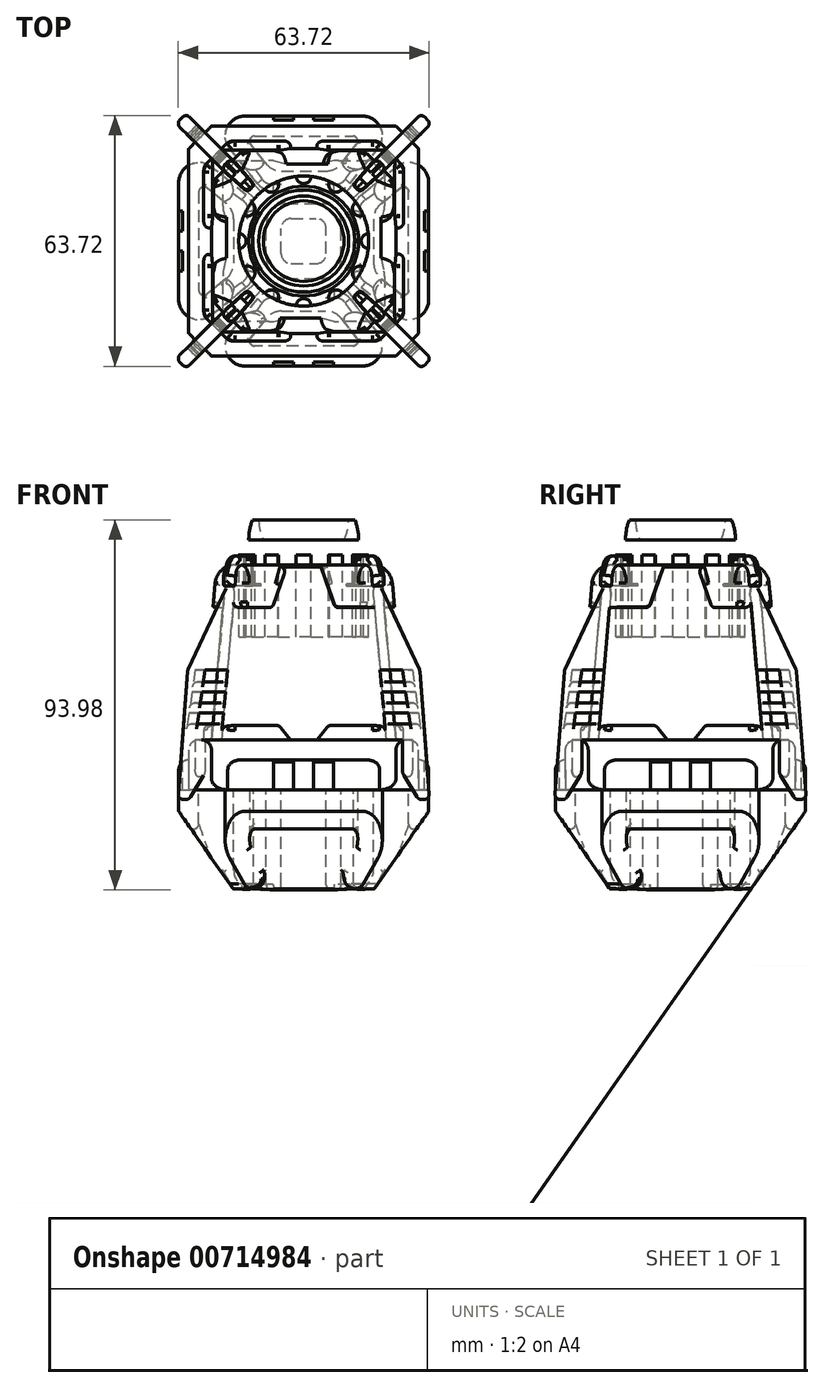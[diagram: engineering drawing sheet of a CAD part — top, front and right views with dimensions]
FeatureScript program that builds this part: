
annotation { "Feature Type Name" : "Feature", "Feature Type Description" : "" }
export const myFeature = defineFeature(function(context is Context, id is Id, definition is map)
    precondition{}
    {
        {
            var Q0;
            Q0=qCreatedBy(makeId("Top.planeOp"),FACE);
            cPlane(context, id + "F0", {"entities" : qUnion([Q0]), "cplaneType" : CPlaneType.OFFSET, "offset" : 44.45 * mm, "width" : 152.4 * mm, "height" : 152.4 * mm});
        }
        {
            var Q0;
            Q0=qCreatedBy(id+"F0.planeOp",FACE);
            var sketch = newSketch(context, id + "F1", { "sketchPlane" : qUnion([Q0])});
            skLineSegment(sketch, "E0.bottom", {"start": v(22.23, -22.22) * mm, "end": v(-22.23, -22.23) * mm});
            skLineSegment(sketch, "E0.top", {"start": v(22.23, 22.23) * mm, "end": v(-22.23, 22.22) * mm});
            skLineSegment(sketch, "E0.left", {"start": v(22.23, -22.22) * mm, "end": v(22.23, 22.23) * mm});
            skLineSegment(sketch, "E0.right", {"start": v(-22.23, -22.23) * mm, "end": v(-22.23, 22.22) * mm});
            skPoint(sketch, "E0.middle", {"position": v(0, 0) * mm});
            skSolve(sketch);
        }
        {
            var Q0;
            Q0=qCreatedBy(makeId("Top.planeOp"),FACE);
            var sketch = newSketch(context, id + "F2", { "sketchPlane" : qUnion([Q0])});
            skLineSegment(sketch, "E1.bottom", {"start": v(-25.4, 25.4) * mm, "end": v(25.4, 25.4) * mm});
            skLineSegment(sketch, "E1.top", {"start": v(-25.4, -25.4) * mm, "end": v(25.4, -25.4) * mm});
            skLineSegment(sketch, "E1.left", {"start": v(-25.4, 25.4) * mm, "end": v(-25.4, -25.4) * mm});
            skLineSegment(sketch, "E1.right", {"start": v(25.4, 25.4) * mm, "end": v(25.4, -25.4) * mm});
            skPoint(sketch, "E1.middle", {"position": v(0, 0) * mm});
            skSolve(sketch);
        }
        {
            var Q0;
            Q0=makeQuery(id+"F2.imprint","IMPRINT",FACE,{"disambiguationData":[TD([[makeQuery(id+"F2.imprint","IMPRINT",EDGE,{"derivedFrom":sQuery(id+"F2.wireOp",EDGE,"E1.bottom")}),-1.0]])]});
            extrude(context, id + "F3", {"entities" : qUnion([Q0]), "depth" : 44.45 * mm, "offsetDistance" : 25.4 * mm});
        }
        {
            var Q0;
            Q0=makeQuery(id+"F3.opExtrude","CAP_EDGE",EDGE,{"disambiguationData":[OSD([sQuery(id+"F2.wireOp",EDGE,"E1.top")])],"isStart":false});
            var Q1;
            Q1=makeQuery(id+"F3.opExtrude","CAP_EDGE",EDGE,{"disambiguationData":[OSD([sQuery(id+"F2.wireOp",EDGE,"E1.left")])],"isStart":false});
            var Q2;
            Q2=makeQuery(id+"F3.opExtrude","CAP_EDGE",EDGE,{"disambiguationData":[OSD([sQuery(id+"F2.wireOp",EDGE,"E1.bottom")])],"isStart":false});
            var Q3;
            Q3=makeQuery(id+"F3.opExtrude","CAP_EDGE",EDGE,{"disambiguationData":[OSD([sQuery(id+"F2.wireOp",EDGE,"E1.right")])],"isStart":false});
            chamfer(context, id + "F4", {"entities" : qUnion([Q0, Q1, Q2, Q3]), "chamferType" : ChamferType.OFFSET_ANGLE, "width" : 3.3 * mm, "oppositeDirection" : false, "angle" : 85 * degree, "tangentPropagation" : true});
        }
        {
            var Q0;
            Q0=makeQuery(id+"F4.opChamfer","BLEND_EDGE",EDGE,{"blendedFrom":[makeQuery(id+"F3.opExtrude","CAP_EDGE",EDGE,{"disambiguationData":[OSD([sQuery(id+"F2.wireOp",EDGE,"E1.bottom")])],"isStart":false}),makeQuery(id+"F3.opExtrude","CAP_EDGE",EDGE,{"disambiguationData":[OSD([sQuery(id+"F2.wireOp",EDGE,"E1.right")])],"isStart":false})],"blendedInto":[]});
            var Q1;
            Q1=makeQuery(id+"F4.opChamfer","BLEND_EDGE",EDGE,{"blendedFrom":[makeQuery(id+"F3.opExtrude","CAP_EDGE",EDGE,{"disambiguationData":[OSD([sQuery(id+"F2.wireOp",EDGE,"E1.bottom")])],"isStart":false}),makeQuery(id+"F3.opExtrude","CAP_EDGE",EDGE,{"disambiguationData":[OSD([sQuery(id+"F2.wireOp",EDGE,"E1.left")])],"isStart":false})],"blendedInto":[]});
            var Q2;
            Q2=makeQuery(id+"F4.opChamfer","BLEND_EDGE",EDGE,{"blendedFrom":[makeQuery(id+"F3.opExtrude","CAP_EDGE",EDGE,{"disambiguationData":[OSD([sQuery(id+"F2.wireOp",EDGE,"E1.top")])],"isStart":false}),makeQuery(id+"F3.opExtrude","CAP_EDGE",EDGE,{"disambiguationData":[OSD([sQuery(id+"F2.wireOp",EDGE,"E1.left")])],"isStart":false})],"blendedInto":[]});
            var Q3;
            Q3=makeQuery(id+"F4.opChamfer","BLEND_EDGE",EDGE,{"blendedFrom":[makeQuery(id+"F3.opExtrude","CAP_EDGE",EDGE,{"disambiguationData":[OSD([sQuery(id+"F2.wireOp",EDGE,"E1.top")])],"isStart":false}),makeQuery(id+"F3.opExtrude","CAP_EDGE",EDGE,{"disambiguationData":[OSD([sQuery(id+"F2.wireOp",EDGE,"E1.right")])],"isStart":false})],"blendedInto":[]});
            chamfer(context, id + "F5", {"entities" : qUnion([Q0, Q1, Q2, Q3]), "width" : 7.62 * mm, "tangentPropagation" : true});
        }
        {
            var Q0;
            Q0=makeQuery(id+"F4.opChamfer","BLEND_FACE",FACE,{"disambiguationData":[OSD([sQuery(id+"F2.wireOp",EDGE,"E1.bottom")])]});
            var sketch = newSketch(context, id + "F6", { "sketchPlane" : qUnion([Q0])});
            skLineSegment(sketch, "E2", {"start": v(23.42, 31.68) * mm, "end": v(-23.11, 31.68) * mm});
            skLineSegment(sketch, "E3.top", {"start": v(7.98, 20.9) * mm, "end": v(-7.96, 20.9) * mm});
            skLineSegment(sketch, "E3.left", {"start": v(7.98, 42.46) * mm, "end": v(7.98, 20.9) * mm});
            skLineSegment(sketch, "E3.right", {"start": v(-7.96, 42.46) * mm, "end": v(-7.96, 20.9) * mm});
            skPoint(sketch, "E3.middle", {"position": v(0.01, 31.68) * mm});
            skLineSegment(sketch, "E4.top", {"start": v(4.3, 20.9) * mm, "end": v(-4.28, 20.9) * mm});
            skLineSegment(sketch, "E4.left", {"start": v(4.3, 42.46) * mm, "end": v(4.3, 20.9) * mm});
            skLineSegment(sketch, "E4.right", {"start": v(-4.28, 42.46) * mm, "end": v(-4.28, 20.9) * mm});
            skLineSegment(sketch, "E5", {"start": v(4.3, 42.46) * mm, "end": v(7.98, 31.68) * mm});
            skLineSegment(sketch, "E6", {"start": v(-4.28, 42.46) * mm, "end": v(-7.96, 31.68) * mm});
            skLineSegment(sketch, "E7", {"start": v(27.08, 1.49) * mm, "end": v(-26.68, 1.49) * mm});
            skLineSegment(sketch, "E8.bottom", {"start": v(3.25, 1.49) * mm, "end": v(-3.23, 1.49) * mm});
            skLineSegment(sketch, "E8.top", {"start": v(3.25, -5.96) * mm, "end": v(-3.23, -5.96) * mm});
            skLineSegment(sketch, "E8.left", {"start": v(3.25, 1.49) * mm, "end": v(3.25, -5.96) * mm});
            skLineSegment(sketch, "E8.right", {"start": v(-3.23, 1.49) * mm, "end": v(-3.23, -5.96) * mm});
            skPoint(sketch, "E8.middle", {"position": v(0.01, -2.24) * mm});
            skLineSegment(sketch, "E9.bottom", {"start": v(6.26, 1.49) * mm, "end": v(-6.23, 1.49) * mm});
            skLineSegment(sketch, "E9.top", {"start": v(6.26, -5.96) * mm, "end": v(-6.23, -5.96) * mm});
            skLineSegment(sketch, "E9.left", {"start": v(6.26, 1.49) * mm, "end": v(6.26, -5.96) * mm});
            skLineSegment(sketch, "E9.right", {"start": v(-6.23, 1.49) * mm, "end": v(-6.23, -5.96) * mm});
            skLineSegment(sketch, "E10", {"start": v(3.25, -2.24) * mm, "end": v(6.26, 1.49) * mm});
            skLineSegment(sketch, "E11", {"start": v(-3.23, -2.24) * mm, "end": v(-6.23, 1.49) * mm});
            skLineSegment(sketch, "E12", {"start": v(0, 42.46) * mm, "end": v(0, -5.44) * mm});
            skPoint(sketch, "E12.startSnap0", {"position": v(0.01, 42.46) * mm});
            skLineSegment(sketch, "E13", {"start": v(-23.11, 31.68) * mm, "end": v(-25.73, 31.68) * mm});
            skLineSegment(sketch, "E14", {"start": v(-26.68, 1.49) * mm, "end": v(-25.73, 31.68) * mm});
            skLineSegment(sketch, "E15", {"start": v(23.42, 31.68) * mm, "end": v(26, 31.68) * mm});
            skLineSegment(sketch, "E16", {"start": v(27.08, 1.49) * mm, "end": v(26, 31.68) * mm});
            skLineSegment(sketch, "E17", {"start": v(-7.96, 31.68) * mm, "end": v(-2.3, 48.28) * mm});
            skLineSegment(sketch, "E18", {"start": v(7.98, 31.68) * mm, "end": v(2.41, 48.03) * mm});
            skLineSegment(sketch, "E19", {"start": v(-2.3, 48.28) * mm, "end": v(2.41, 48.03) * mm});
            skSolve(sketch);
        }
        {
            var Q0;
            {var subQ4=sQuery(id+"F6.wireOp",EDGE,"E19");Q0=makeQuery(id+"F6.imprint","IMPRINT",FACE,{"disambiguationData":[TD([[makeQuery(id+"F6.imprint","IMPRINT",EDGE,{"derivedFrom":subQ4}),-1.0]])]});}
            var Q1;
            {var subQ0=sQuery(id+"F6.wireOp",EDGE,"E12");var subQ1=sQuery(id+"F6.wireOp",EDGE,"E2");var subQ2=makeQuery(id+"F6.imprint","INTERSECT",VERTEX,{"derivedFrom":[subQ1,subQ0]});Q1=makeQuery(id+"F6.imprint","IMPRINT",FACE,{"disambiguationData":[TD([[makeQuery(id+"F6.imprint","IMPRINT",EDGE,{"disambiguationData":[TD([[subQ2,-1.0]])],"derivedFrom":subQ1}),-1.0]])]});}
            var Q2;
            {var subQ0=sQuery(id+"F6.wireOp",EDGE,"E4.left");var subQ1=sQuery(id+"F6.wireOp",EDGE,"E2");var subQ2=makeQuery(id+"F6.imprint","INTERSECT",VERTEX,{"derivedFrom":[subQ1,subQ0]});Q2=makeQuery(id+"F6.imprint","IMPRINT",FACE,{"disambiguationData":[TD([[makeQuery(id+"F6.imprint","IMPRINT",EDGE,{"disambiguationData":[TD([[subQ2,-1.0]])],"derivedFrom":subQ1}),-1.0]])]});}
            var Q3;
            {var subQ1=sQuery(id+"F6.wireOp",EDGE,"E2");var subQ3=sQuery(id+"F6.wireOp",EDGE,"E4.left");var subQ4=makeQuery(id+"F6.imprint","INTERSECT",VERTEX,{"derivedFrom":[subQ1,subQ3]});Q3=makeQuery(id+"F6.imprint","IMPRINT",FACE,{"disambiguationData":[TD([[makeQuery(id+"F6.imprint","IMPRINT",EDGE,{"disambiguationData":[TD([[subQ4,1.0]])],"derivedFrom":subQ1}),-1.0]])]});}
            var Q4;
            {var subQ1=sQuery(id+"F6.wireOp",EDGE,"E2");var subQ3=sQuery(id+"F6.wireOp",EDGE,"E4.right");var subQ4=makeQuery(id+"F6.imprint","INTERSECT",VERTEX,{"derivedFrom":[subQ1,subQ3]});Q4=makeQuery(id+"F6.imprint","IMPRINT",FACE,{"disambiguationData":[TD([[makeQuery(id+"F6.imprint","IMPRINT",EDGE,{"disambiguationData":[TD([[subQ4,-1.0]])],"derivedFrom":subQ1}),-1.0]])]});}
            var Q5;
            {var subQ0=sQuery(id+"F6.wireOp",EDGE,"E3.right");var subQ1=sQuery(id+"F6.wireOp",EDGE,"E3.top");var subQ2=makeQuery(id+"F6.imprint","INTERSECT",VERTEX,{"derivedFrom":[subQ1,subQ0]});Q5=makeQuery(id+"F6.imprint","IMPRINT",FACE,{"disambiguationData":[TD([[makeQuery(id+"F6.imprint","IMPRINT",EDGE,{"disambiguationData":[TD([[subQ2,1.0]])],"derivedFrom":subQ1}),1.0]])]});}
            var Q6;
            {var subQ1=sQuery(id+"F6.wireOp",EDGE,"E2");var subQ3=sQuery(id+"F6.wireOp",EDGE,"E4.right");var subQ4=makeQuery(id+"F6.imprint","INTERSECT",VERTEX,{"derivedFrom":[subQ1,subQ3]});Q6=makeQuery(id+"F6.imprint","IMPRINT",FACE,{"disambiguationData":[TD([[makeQuery(id+"F6.imprint","IMPRINT",EDGE,{"disambiguationData":[TD([[subQ4,-1.0]])],"derivedFrom":subQ1}),1.0]])]});}
            var Q7;
            {var subQ0=sQuery(id+"F6.wireOp",EDGE,"E12");var subQ1=sQuery(id+"F6.wireOp",EDGE,"E2");var subQ2=makeQuery(id+"F6.imprint","INTERSECT",VERTEX,{"derivedFrom":[subQ1,subQ0]});Q7=makeQuery(id+"F6.imprint","IMPRINT",FACE,{"disambiguationData":[TD([[makeQuery(id+"F6.imprint","IMPRINT",EDGE,{"disambiguationData":[TD([[subQ2,-1.0]])],"derivedFrom":subQ1}),1.0]])]});}
            var Q8;
            {var subQ0=sQuery(id+"F6.wireOp",EDGE,"E4.left");var subQ1=sQuery(id+"F6.wireOp",EDGE,"E2");var subQ2=makeQuery(id+"F6.imprint","INTERSECT",VERTEX,{"derivedFrom":[subQ1,subQ0]});Q8=makeQuery(id+"F6.imprint","IMPRINT",FACE,{"disambiguationData":[TD([[makeQuery(id+"F6.imprint","IMPRINT",EDGE,{"disambiguationData":[TD([[subQ2,-1.0]])],"derivedFrom":subQ1}),1.0]])]});}
            var Q9;
            {var subQ1=sQuery(id+"F6.wireOp",EDGE,"E2");var subQ3=sQuery(id+"F6.wireOp",EDGE,"E4.left");var subQ4=makeQuery(id+"F6.imprint","INTERSECT",VERTEX,{"derivedFrom":[subQ1,subQ3]});Q9=makeQuery(id+"F6.imprint","IMPRINT",FACE,{"disambiguationData":[TD([[makeQuery(id+"F6.imprint","IMPRINT",EDGE,{"disambiguationData":[TD([[subQ4,1.0]])],"derivedFrom":subQ1}),1.0]])]});}
            var Q10;
            {var subQ0=sQuery(id+"F6.wireOp",EDGE,"E3.left");var subQ1=sQuery(id+"F6.wireOp",EDGE,"E3.top");var subQ2=makeQuery(id+"F6.imprint","INTERSECT",VERTEX,{"derivedFrom":[subQ1,subQ0]});Q10=makeQuery(id+"F6.imprint","IMPRINT",FACE,{"disambiguationData":[TD([[makeQuery(id+"F6.imprint","IMPRINT",EDGE,{"disambiguationData":[TD([[subQ2,-1.0]])],"derivedFrom":subQ1}),1.0]])]});}
            var Q11;
            {var subQ3=sQuery(id+"F6.wireOp",EDGE,"E11");Q11=makeQuery(id+"F6.imprint","IMPRINT",FACE,{"disambiguationData":[TD([[makeQuery(id+"F6.imprint","IMPRINT",EDGE,{"derivedFrom":subQ3}),-1.0]])]});}
            var Q12;
            {var subQ4=sQuery(id+"F6.wireOp",EDGE,"E9.bottom");var subQ6=sQuery(id+"F6.wireOp",EDGE,"E8.left");var subQ9=makeQuery(id+"F6.imprint","INTERSECT",VERTEX,{"derivedFrom":[subQ6,subQ4]});Q12=makeQuery(id+"F6.imprint","IMPRINT",FACE,{"disambiguationData":[TD([[makeQuery(id+"F6.imprint","IMPRINT",EDGE,{"disambiguationData":[TD([[subQ9,-1.0]])],"derivedFrom":subQ6}),-1.0]])]});}
            var Q13;
            {var subQ3=sQuery(id+"F6.wireOp",EDGE,"E10");Q13=makeQuery(id+"F6.imprint","IMPRINT",FACE,{"disambiguationData":[TD([[makeQuery(id+"F6.imprint","IMPRINT",EDGE,{"derivedFrom":subQ3}),1.0]])]});}
            var Q14;
            {var subQ7=sQuery(id+"F6.wireOp",EDGE,"E15");Q14=makeQuery(id+"F6.imprint","IMPRINT",FACE,{"disambiguationData":[TD([[makeQuery(id+"F6.imprint","IMPRINT",EDGE,{"derivedFrom":subQ7}),-1.0]])]});}
            var Q15;
            {var subQ7=sQuery(id+"F6.wireOp",EDGE,"E13");Q15=makeQuery(id+"F6.imprint","IMPRINT",FACE,{"disambiguationData":[TD([[makeQuery(id+"F6.imprint","IMPRINT",EDGE,{"derivedFrom":subQ7}),1.0]])]});}
            var Q16;
            {var subQ0=sQuery(id+"F6.wireOp",EDGE,"E17");var subQ1=sQuery(id+"F6.wireOp",EDGE,"E4.right");var subQ2=makeQuery(id+"F6.imprint","INTERSECT",VERTEX,{"derivedFrom":[subQ1,subQ0]});Q16=makeQuery(id+"F6.imprint","IMPRINT",FACE,{"disambiguationData":[TD([[makeQuery(id+"F6.imprint","IMPRINT",EDGE,{"disambiguationData":[TD([[subQ2,-1.0]])],"derivedFrom":subQ1}),-1.0]])]});}
            var Q17;
            {var subQ0=sQuery(id+"F6.wireOp",EDGE,"E18");var subQ1=sQuery(id+"F6.wireOp",EDGE,"E4.left");var subQ2=makeQuery(id+"F6.imprint","INTERSECT",VERTEX,{"derivedFrom":[subQ1,subQ0]});Q17=makeQuery(id+"F6.imprint","IMPRINT",FACE,{"disambiguationData":[TD([[makeQuery(id+"F6.imprint","IMPRINT",EDGE,{"disambiguationData":[TD([[subQ2,-1.0]])],"derivedFrom":subQ1}),1.0]])]});}
            extrude(context, id + "F7", {"entities" : qUnion([Q0, Q1, Q2, Q3, Q4, Q5, Q6, Q7, Q8, Q9, Q10, Q11, Q12, Q13, Q14, Q15, Q16, Q17]), "operationType" : NewBodyOperationType.REMOVE, "oppositeDirection" : true, "depth" : 2.54 * mm, "offsetDistance" : 25.4 * mm});
        }
        {
            var Q0;
            Q0=makeQuery(id+"F4.opChamfer","BLEND_FACE",FACE,{"disambiguationData":[OSD([sQuery(id+"F2.wireOp",EDGE,"E1.left")])]});
            var sketch = newSketch(context, id + "F8", { "sketchPlane" : qUnion([Q0])});
            skLineSegment(sketch, "E20", {"start": v(23.38, 31.67) * mm, "end": v(-23.15, 31.67) * mm});
            skLineSegment(sketch, "E21.top", {"start": v(7.98, 20.88) * mm, "end": v(-7.96, 20.88) * mm});
            skLineSegment(sketch, "E21.left", {"start": v(7.98, 42.45) * mm, "end": v(7.98, 20.88) * mm});
            skLineSegment(sketch, "E21.right", {"start": v(-7.96, 42.45) * mm, "end": v(-7.96, 20.88) * mm});
            skPoint(sketch, "E21.middle", {"position": v(0.01, 31.67) * mm});
            skLineSegment(sketch, "E22.top", {"start": v(4.2, 20.88) * mm, "end": v(-4.18, 20.88) * mm});
            skLineSegment(sketch, "E22.left", {"start": v(4.2, 42.45) * mm, "end": v(4.2, 20.88) * mm});
            skLineSegment(sketch, "E22.right", {"start": v(-4.18, 42.45) * mm, "end": v(-4.18, 20.88) * mm});
            skLineSegment(sketch, "E23", {"start": v(4.2, 42.45) * mm, "end": v(7.98, 31.67) * mm});
            skLineSegment(sketch, "E24", {"start": v(-4.18, 42.45) * mm, "end": v(-7.96, 31.67) * mm});
            skLineSegment(sketch, "E25", {"start": v(27.08, 1.52) * mm, "end": v(-26.68, 1.52) * mm});
            skLineSegment(sketch, "E26.bottom", {"start": v(3.25, 1.52) * mm, "end": v(-3.23, 1.52) * mm});
            skLineSegment(sketch, "E26.top", {"start": v(3.25, -6.02) * mm, "end": v(-3.23, -6.02) * mm});
            skLineSegment(sketch, "E26.left", {"start": v(3.25, 1.52) * mm, "end": v(3.25, -6.02) * mm});
            skLineSegment(sketch, "E26.right", {"start": v(-3.23, 1.52) * mm, "end": v(-3.23, -6.02) * mm});
            skPoint(sketch, "E26.middle", {"position": v(0.01, -2.25) * mm});
            skLineSegment(sketch, "E27.bottom", {"start": v(6.28, 1.52) * mm, "end": v(-6.26, 1.52) * mm});
            skLineSegment(sketch, "E27.top", {"start": v(6.28, -6.02) * mm, "end": v(-6.26, -6.02) * mm});
            skLineSegment(sketch, "E27.left", {"start": v(6.28, 1.52) * mm, "end": v(6.28, -6.02) * mm});
            skLineSegment(sketch, "E27.right", {"start": v(-6.26, 1.52) * mm, "end": v(-6.26, -6.02) * mm});
            skLineSegment(sketch, "E28", {"start": v(3.25, -2.25) * mm, "end": v(6.28, 1.52) * mm});
            skLineSegment(sketch, "E29", {"start": v(-3.23, -2.25) * mm, "end": v(-6.26, 1.52) * mm});
            skLineSegment(sketch, "E30", {"start": v(0, 42.45) * mm, "end": v(0, -2.29) * mm});
            skPoint(sketch, "E30.startSnap0", {"position": v(0.01, 42.45) * mm});
            skLineSegment(sketch, "E31", {"start": v(-23.15, 31.67) * mm, "end": v(-25.73, 31.67) * mm});
            skLineSegment(sketch, "E32", {"start": v(-26.68, 1.52) * mm, "end": v(-25.73, 31.67) * mm});
            skLineSegment(sketch, "E33", {"start": v(23.38, 31.67) * mm, "end": v(26.01, 31.67) * mm});
            skLineSegment(sketch, "E34", {"start": v(27.08, 1.52) * mm, "end": v(26.01, 31.67) * mm});
            skLineSegment(sketch, "E35", {"start": v(-7.96, 31.67) * mm, "end": v(-2.14, 48.27) * mm});
            skLineSegment(sketch, "E36", {"start": v(7.98, 31.67) * mm, "end": v(2.25, 48.02) * mm});
            skLineSegment(sketch, "E37", {"start": v(-2.14, 48.27) * mm, "end": v(2.25, 48.02) * mm});
            skSolve(sketch);
        }
        {
            var Q0;
            {var subQ4=sQuery(id+"F8.wireOp",EDGE,"E37");Q0=makeQuery(id+"F8.imprint","IMPRINT",FACE,{"disambiguationData":[TD([[makeQuery(id+"F8.imprint","IMPRINT",EDGE,{"derivedFrom":subQ4}),-1.0]])]});}
            var Q1;
            {var subQ0=sQuery(id+"F8.wireOp",EDGE,"E30");var subQ1=sQuery(id+"F8.wireOp",EDGE,"E20");var subQ2=makeQuery(id+"F8.imprint","INTERSECT",VERTEX,{"derivedFrom":[subQ1,subQ0]});Q1=makeQuery(id+"F8.imprint","IMPRINT",FACE,{"disambiguationData":[TD([[makeQuery(id+"F8.imprint","IMPRINT",EDGE,{"disambiguationData":[TD([[subQ2,-1.0]])],"derivedFrom":subQ1}),-1.0]])]});}
            var Q2;
            {var subQ0=sQuery(id+"F8.wireOp",EDGE,"E22.left");var subQ1=sQuery(id+"F8.wireOp",EDGE,"E20");var subQ2=makeQuery(id+"F8.imprint","INTERSECT",VERTEX,{"derivedFrom":[subQ1,subQ0]});Q2=makeQuery(id+"F8.imprint","IMPRINT",FACE,{"disambiguationData":[TD([[makeQuery(id+"F8.imprint","IMPRINT",EDGE,{"disambiguationData":[TD([[subQ2,-1.0]])],"derivedFrom":subQ1}),-1.0]])]});}
            var Q3;
            {var subQ1=sQuery(id+"F8.wireOp",EDGE,"E20");var subQ3=sQuery(id+"F8.wireOp",EDGE,"E22.left");var subQ4=makeQuery(id+"F8.imprint","INTERSECT",VERTEX,{"derivedFrom":[subQ1,subQ3]});Q3=makeQuery(id+"F8.imprint","IMPRINT",FACE,{"disambiguationData":[TD([[makeQuery(id+"F8.imprint","IMPRINT",EDGE,{"disambiguationData":[TD([[subQ4,1.0]])],"derivedFrom":subQ1}),-1.0]])]});}
            var Q4;
            {var subQ1=sQuery(id+"F8.wireOp",EDGE,"E20");var subQ3=sQuery(id+"F8.wireOp",EDGE,"E22.right");var subQ4=makeQuery(id+"F8.imprint","INTERSECT",VERTEX,{"derivedFrom":[subQ1,subQ3]});Q4=makeQuery(id+"F8.imprint","IMPRINT",FACE,{"disambiguationData":[TD([[makeQuery(id+"F8.imprint","IMPRINT",EDGE,{"disambiguationData":[TD([[subQ4,-1.0]])],"derivedFrom":subQ1}),-1.0]])]});}
            var Q5;
            {var subQ1=sQuery(id+"F8.wireOp",EDGE,"E20");var subQ3=sQuery(id+"F8.wireOp",EDGE,"E22.right");var subQ4=makeQuery(id+"F8.imprint","INTERSECT",VERTEX,{"derivedFrom":[subQ1,subQ3]});Q5=makeQuery(id+"F8.imprint","IMPRINT",FACE,{"disambiguationData":[TD([[makeQuery(id+"F8.imprint","IMPRINT",EDGE,{"disambiguationData":[TD([[subQ4,-1.0]])],"derivedFrom":subQ1}),1.0]])]});}
            var Q6;
            {var subQ0=sQuery(id+"F8.wireOp",EDGE,"E30");var subQ1=sQuery(id+"F8.wireOp",EDGE,"E20");var subQ2=makeQuery(id+"F8.imprint","INTERSECT",VERTEX,{"derivedFrom":[subQ1,subQ0]});Q6=makeQuery(id+"F8.imprint","IMPRINT",FACE,{"disambiguationData":[TD([[makeQuery(id+"F8.imprint","IMPRINT",EDGE,{"disambiguationData":[TD([[subQ2,-1.0]])],"derivedFrom":subQ1}),1.0]])]});}
            var Q7;
            {var subQ0=sQuery(id+"F8.wireOp",EDGE,"E22.left");var subQ1=sQuery(id+"F8.wireOp",EDGE,"E20");var subQ2=makeQuery(id+"F8.imprint","INTERSECT",VERTEX,{"derivedFrom":[subQ1,subQ0]});Q7=makeQuery(id+"F8.imprint","IMPRINT",FACE,{"disambiguationData":[TD([[makeQuery(id+"F8.imprint","IMPRINT",EDGE,{"disambiguationData":[TD([[subQ2,-1.0]])],"derivedFrom":subQ1}),1.0]])]});}
            var Q8;
            {var subQ1=sQuery(id+"F8.wireOp",EDGE,"E20");var subQ3=sQuery(id+"F8.wireOp",EDGE,"E22.left");var subQ4=makeQuery(id+"F8.imprint","INTERSECT",VERTEX,{"derivedFrom":[subQ1,subQ3]});Q8=makeQuery(id+"F8.imprint","IMPRINT",FACE,{"disambiguationData":[TD([[makeQuery(id+"F8.imprint","IMPRINT",EDGE,{"disambiguationData":[TD([[subQ4,1.0]])],"derivedFrom":subQ1}),1.0]])]});}
            var Q9;
            {var subQ7=sQuery(id+"F8.wireOp",EDGE,"E31");Q9=makeQuery(id+"F8.imprint","IMPRINT",FACE,{"disambiguationData":[TD([[makeQuery(id+"F8.imprint","IMPRINT",EDGE,{"derivedFrom":subQ7}),1.0]])]});}
            var Q10;
            {var subQ0=sQuery(id+"F8.wireOp",EDGE,"E21.right");var subQ1=sQuery(id+"F8.wireOp",EDGE,"E21.top");var subQ2=makeQuery(id+"F8.imprint","INTERSECT",VERTEX,{"derivedFrom":[subQ1,subQ0]});Q10=makeQuery(id+"F8.imprint","IMPRINT",FACE,{"disambiguationData":[TD([[makeQuery(id+"F8.imprint","IMPRINT",EDGE,{"disambiguationData":[TD([[subQ2,1.0]])],"derivedFrom":subQ1}),1.0]])]});}
            var Q11;
            {var subQ0=sQuery(id+"F8.wireOp",EDGE,"E21.left");var subQ1=sQuery(id+"F8.wireOp",EDGE,"E21.top");var subQ2=makeQuery(id+"F8.imprint","INTERSECT",VERTEX,{"derivedFrom":[subQ1,subQ0]});Q11=makeQuery(id+"F8.imprint","IMPRINT",FACE,{"disambiguationData":[TD([[makeQuery(id+"F8.imprint","IMPRINT",EDGE,{"disambiguationData":[TD([[subQ2,-1.0]])],"derivedFrom":subQ1}),1.0]])]});}
            var Q12;
            {var subQ13=sQuery(id+"F8.wireOp",EDGE,"E33");Q12=makeQuery(id+"F8.imprint","IMPRINT",FACE,{"disambiguationData":[TD([[makeQuery(id+"F8.imprint","IMPRINT",EDGE,{"derivedFrom":subQ13}),-1.0]])]});}
            var Q13;
            {var subQ4=sQuery(id+"F8.wireOp",EDGE,"E27.bottom");var subQ6=sQuery(id+"F8.wireOp",EDGE,"E26.left");var subQ9=makeQuery(id+"F8.imprint","INTERSECT",VERTEX,{"derivedFrom":[subQ6,subQ4]});Q13=makeQuery(id+"F8.imprint","IMPRINT",FACE,{"disambiguationData":[TD([[makeQuery(id+"F8.imprint","IMPRINT",EDGE,{"disambiguationData":[TD([[subQ9,-1.0]])],"derivedFrom":subQ6}),-1.0]])]});}
            var Q14;
            {var subQ3=sQuery(id+"F8.wireOp",EDGE,"E29");Q14=makeQuery(id+"F8.imprint","IMPRINT",FACE,{"disambiguationData":[TD([[makeQuery(id+"F8.imprint","IMPRINT",EDGE,{"derivedFrom":subQ3}),-1.0]])]});}
            var Q15;
            {var subQ3=sQuery(id+"F8.wireOp",EDGE,"E28");Q15=makeQuery(id+"F8.imprint","IMPRINT",FACE,{"disambiguationData":[TD([[makeQuery(id+"F8.imprint","IMPRINT",EDGE,{"derivedFrom":subQ3}),1.0]])]});}
            var Q16;
            {var subQ0=sQuery(id+"F8.wireOp",EDGE,"E36");var subQ1=sQuery(id+"F8.wireOp",EDGE,"E22.left");var subQ2=makeQuery(id+"F8.imprint","INTERSECT",VERTEX,{"derivedFrom":[subQ1,subQ0]});Q16=makeQuery(id+"F8.imprint","IMPRINT",FACE,{"disambiguationData":[TD([[makeQuery(id+"F8.imprint","IMPRINT",EDGE,{"disambiguationData":[TD([[subQ2,-1.0]])],"derivedFrom":subQ1}),1.0]])]});}
            var Q17;
            {var subQ0=sQuery(id+"F8.wireOp",EDGE,"E35");var subQ1=sQuery(id+"F8.wireOp",EDGE,"E22.right");var subQ2=makeQuery(id+"F8.imprint","INTERSECT",VERTEX,{"derivedFrom":[subQ1,subQ0]});Q17=makeQuery(id+"F8.imprint","IMPRINT",FACE,{"disambiguationData":[TD([[makeQuery(id+"F8.imprint","IMPRINT",EDGE,{"disambiguationData":[TD([[subQ2,-1.0]])],"derivedFrom":subQ1}),-1.0]])]});}
            extrude(context, id + "F9", {"entities" : qUnion([Q0, Q1, Q2, Q3, Q4, Q5, Q6, Q7, Q8, Q9, Q10, Q11, Q12, Q13, Q14, Q15, Q16, Q17]), "operationType" : NewBodyOperationType.REMOVE, "oppositeDirection" : true, "depth" : 2.54 * mm, "offsetDistance" : 25.4 * mm});
        }
        {
            var Q0;
            Q0=makeQuery(id+"F4.opChamfer","BLEND_FACE",FACE,{"disambiguationData":[OSD([sQuery(id+"F2.wireOp",EDGE,"E1.top")])]});
            var sketch = newSketch(context, id + "F10", { "sketchPlane" : qUnion([Q0])});
            skLineSegment(sketch, "E38", {"start": v(23.34, 31.68) * mm, "end": v(-23.2, 31.68) * mm});
            skLineSegment(sketch, "E39.top", {"start": v(7.99, 20.9) * mm, "end": v(-7.95, 20.9) * mm});
            skLineSegment(sketch, "E39.left", {"start": v(7.99, 42.47) * mm, "end": v(7.99, 20.9) * mm});
            skLineSegment(sketch, "E39.right", {"start": v(-7.95, 42.47) * mm, "end": v(-7.95, 20.9) * mm});
            skPoint(sketch, "E39.middle", {"position": v(0.02, 31.68) * mm});
            skLineSegment(sketch, "E40.top", {"start": v(4.2, 20.9) * mm, "end": v(-4.17, 20.9) * mm});
            skLineSegment(sketch, "E40.left", {"start": v(4.2, 42.47) * mm, "end": v(4.2, 20.9) * mm});
            skLineSegment(sketch, "E40.right", {"start": v(-4.17, 42.47) * mm, "end": v(-4.17, 20.9) * mm});
            skLineSegment(sketch, "E41", {"start": v(4.2, 42.47) * mm, "end": v(7.99, 31.68) * mm});
            skLineSegment(sketch, "E42", {"start": v(-4.17, 42.47) * mm, "end": v(-7.95, 31.68) * mm});
            skLineSegment(sketch, "E43", {"start": v(27.08, 1.54) * mm, "end": v(-26.67, 1.54) * mm});
            skLineSegment(sketch, "E44.bottom", {"start": v(3.26, 1.54) * mm, "end": v(-3.22, 1.54) * mm});
            skLineSegment(sketch, "E44.top", {"start": v(3.26, -6) * mm, "end": v(-3.22, -6) * mm});
            skLineSegment(sketch, "E44.left", {"start": v(3.26, 1.54) * mm, "end": v(3.26, -6) * mm});
            skLineSegment(sketch, "E44.right", {"start": v(-3.22, 1.54) * mm, "end": v(-3.22, -6) * mm});
            skPoint(sketch, "E44.middle", {"position": v(0.02, -2.23) * mm});
            skLineSegment(sketch, "E45.bottom", {"start": v(6.29, 1.54) * mm, "end": v(-6.25, 1.54) * mm});
            skLineSegment(sketch, "E45.top", {"start": v(6.29, -6) * mm, "end": v(-6.25, -6) * mm});
            skLineSegment(sketch, "E45.left", {"start": v(6.29, 1.54) * mm, "end": v(6.29, -6) * mm});
            skLineSegment(sketch, "E45.right", {"start": v(-6.25, 1.54) * mm, "end": v(-6.25, -6) * mm});
            skLineSegment(sketch, "E46", {"start": v(3.26, -2.23) * mm, "end": v(6.29, 1.54) * mm});
            skLineSegment(sketch, "E47", {"start": v(-3.22, -2.23) * mm, "end": v(-6.25, 1.54) * mm});
            skLineSegment(sketch, "E48", {"start": v(0, 42.47) * mm, "end": v(0, 2.2) * mm});
            skPoint(sketch, "E48.startSnap0", {"position": v(0.02, 42.47) * mm});
            skLineSegment(sketch, "E49", {"start": v(-23.2, 31.68) * mm, "end": v(-25.72, 31.68) * mm});
            skLineSegment(sketch, "E50", {"start": v(-26.67, 1.54) * mm, "end": v(-25.72, 31.68) * mm});
            skLineSegment(sketch, "E51", {"start": v(23.34, 31.68) * mm, "end": v(26.02, 31.68) * mm});
            skLineSegment(sketch, "E52", {"start": v(27.08, 1.54) * mm, "end": v(26.02, 31.68) * mm});
            skLineSegment(sketch, "E53", {"start": v(-7.95, 31.68) * mm, "end": v(-2.13, 48.28) * mm});
            skLineSegment(sketch, "E54", {"start": v(7.99, 31.68) * mm, "end": v(2.26, 48.04) * mm});
            skLineSegment(sketch, "E55", {"start": v(-2.13, 48.28) * mm, "end": v(2.26, 48.04) * mm});
            skSolve(sketch);
        }
        {
            var Q0;
            {var subQ3=sQuery(id+"F10.wireOp",EDGE,"E55");Q0=makeQuery(id+"F10.imprint","IMPRINT",FACE,{"disambiguationData":[TD([[makeQuery(id+"F10.imprint","IMPRINT",EDGE,{"derivedFrom":subQ3}),-1.0]])]});}
            var Q1;
            {var subQ0=sQuery(id+"F10.wireOp",EDGE,"E48");var subQ1=sQuery(id+"F10.wireOp",EDGE,"E38");var subQ2=makeQuery(id+"F10.imprint","INTERSECT",VERTEX,{"derivedFrom":[subQ1,subQ0]});Q1=makeQuery(id+"F10.imprint","IMPRINT",FACE,{"disambiguationData":[TD([[makeQuery(id+"F10.imprint","IMPRINT",EDGE,{"disambiguationData":[TD([[subQ2,-1.0]])],"derivedFrom":subQ1}),-1.0]])]});}
            var Q2;
            {var subQ0=sQuery(id+"F10.wireOp",EDGE,"E40.left");var subQ1=sQuery(id+"F10.wireOp",EDGE,"E38");var subQ2=makeQuery(id+"F10.imprint","INTERSECT",VERTEX,{"derivedFrom":[subQ1,subQ0]});Q2=makeQuery(id+"F10.imprint","IMPRINT",FACE,{"disambiguationData":[TD([[makeQuery(id+"F10.imprint","IMPRINT",EDGE,{"disambiguationData":[TD([[subQ2,-1.0]])],"derivedFrom":subQ1}),-1.0]])]});}
            var Q3;
            {var subQ1=sQuery(id+"F10.wireOp",EDGE,"E38");var subQ3=sQuery(id+"F10.wireOp",EDGE,"E40.right");var subQ4=makeQuery(id+"F10.imprint","INTERSECT",VERTEX,{"derivedFrom":[subQ1,subQ3]});Q3=makeQuery(id+"F10.imprint","IMPRINT",FACE,{"disambiguationData":[TD([[makeQuery(id+"F10.imprint","IMPRINT",EDGE,{"disambiguationData":[TD([[subQ4,-1.0]])],"derivedFrom":subQ1}),-1.0]])]});}
            var Q4;
            {var subQ1=sQuery(id+"F10.wireOp",EDGE,"E38");var subQ3=sQuery(id+"F10.wireOp",EDGE,"E40.left");var subQ4=makeQuery(id+"F10.imprint","INTERSECT",VERTEX,{"derivedFrom":[subQ1,subQ3]});Q4=makeQuery(id+"F10.imprint","IMPRINT",FACE,{"disambiguationData":[TD([[makeQuery(id+"F10.imprint","IMPRINT",EDGE,{"disambiguationData":[TD([[subQ4,1.0]])],"derivedFrom":subQ1}),-1.0]])]});}
            var Q5;
            {var subQ0=sQuery(id+"F10.wireOp",EDGE,"E53");var subQ1=sQuery(id+"F10.wireOp",EDGE,"E40.right");var subQ2=makeQuery(id+"F10.imprint","INTERSECT",VERTEX,{"derivedFrom":[subQ1,subQ0]});Q5=makeQuery(id+"F10.imprint","IMPRINT",FACE,{"disambiguationData":[TD([[makeQuery(id+"F10.imprint","IMPRINT",EDGE,{"disambiguationData":[TD([[subQ2,-1.0]])],"derivedFrom":subQ1}),-1.0]])]});}
            var Q6;
            {var subQ0=sQuery(id+"F10.wireOp",EDGE,"E54");var subQ1=sQuery(id+"F10.wireOp",EDGE,"E40.left");var subQ2=makeQuery(id+"F10.imprint","INTERSECT",VERTEX,{"derivedFrom":[subQ1,subQ0]});Q6=makeQuery(id+"F10.imprint","IMPRINT",FACE,{"disambiguationData":[TD([[makeQuery(id+"F10.imprint","IMPRINT",EDGE,{"disambiguationData":[TD([[subQ2,-1.0]])],"derivedFrom":subQ1}),1.0]])]});}
            var Q7;
            {var subQ0=sQuery(id+"F10.wireOp",EDGE,"E39.right");var subQ1=sQuery(id+"F10.wireOp",EDGE,"E39.top");var subQ2=makeQuery(id+"F10.imprint","INTERSECT",VERTEX,{"derivedFrom":[subQ1,subQ0]});Q7=makeQuery(id+"F10.imprint","IMPRINT",FACE,{"disambiguationData":[TD([[makeQuery(id+"F10.imprint","IMPRINT",EDGE,{"disambiguationData":[TD([[subQ2,1.0]])],"derivedFrom":subQ1}),-1.0]])]});}
            var Q8;
            {var subQ0=sQuery(id+"F10.wireOp",EDGE,"E48");var subQ1=sQuery(id+"F10.wireOp",EDGE,"E38");var subQ2=makeQuery(id+"F10.imprint","INTERSECT",VERTEX,{"derivedFrom":[subQ1,subQ0]});Q8=makeQuery(id+"F10.imprint","IMPRINT",FACE,{"disambiguationData":[TD([[makeQuery(id+"F10.imprint","IMPRINT",EDGE,{"disambiguationData":[TD([[subQ2,-1.0]])],"derivedFrom":subQ1}),1.0]])]});}
            var Q9;
            {var subQ0=sQuery(id+"F10.wireOp",EDGE,"E40.left");var subQ1=sQuery(id+"F10.wireOp",EDGE,"E38");var subQ2=makeQuery(id+"F10.imprint","INTERSECT",VERTEX,{"derivedFrom":[subQ1,subQ0]});Q9=makeQuery(id+"F10.imprint","IMPRINT",FACE,{"disambiguationData":[TD([[makeQuery(id+"F10.imprint","IMPRINT",EDGE,{"disambiguationData":[TD([[subQ2,-1.0]])],"derivedFrom":subQ1}),1.0]])]});}
            var Q10;
            {var subQ5=sQuery(id+"F10.wireOp",EDGE,"E39.left");var subQ6=sQuery(id+"F10.wireOp",EDGE,"E39.top");var subQ7=makeQuery(id+"F10.imprint","INTERSECT",VERTEX,{"derivedFrom":[subQ6,subQ5]});Q10=makeQuery(id+"F10.imprint","IMPRINT",FACE,{"disambiguationData":[TD([[makeQuery(id+"F10.imprint","IMPRINT",EDGE,{"disambiguationData":[TD([[subQ7,-1.0]])],"derivedFrom":subQ6}),-1.0]])]});}
            var Q11;
            {var subQ0=sQuery(id+"F10.wireOp",EDGE,"E39.left");var subQ1=sQuery(id+"F10.wireOp",EDGE,"E39.top");var subQ2=makeQuery(id+"F10.imprint","INTERSECT",VERTEX,{"derivedFrom":[subQ1,subQ0]});Q11=makeQuery(id+"F10.imprint","IMPRINT",FACE,{"disambiguationData":[TD([[makeQuery(id+"F10.imprint","IMPRINT",EDGE,{"disambiguationData":[TD([[subQ2,-1.0]])],"derivedFrom":subQ1}),1.0]])]});}
            var Q12;
            {var subQ1=sQuery(id+"F10.wireOp",EDGE,"E49");Q12=makeQuery(id+"F10.imprint","IMPRINT",FACE,{"disambiguationData":[TD([[makeQuery(id+"F10.imprint","IMPRINT",EDGE,{"derivedFrom":subQ1}),1.0]])]});}
            var Q13;
            {var subQ0=sQuery(id+"F10.wireOp",EDGE,"E39.right");var subQ1=sQuery(id+"F10.wireOp",EDGE,"E39.top");var subQ2=makeQuery(id+"F10.imprint","INTERSECT",VERTEX,{"derivedFrom":[subQ1,subQ0]});Q13=makeQuery(id+"F10.imprint","IMPRINT",FACE,{"disambiguationData":[TD([[makeQuery(id+"F10.imprint","IMPRINT",EDGE,{"disambiguationData":[TD([[subQ2,1.0]])],"derivedFrom":subQ1}),1.0]])]});}
            var Q14;
            {var subQ3=sQuery(id+"F10.wireOp",EDGE,"E47");Q14=makeQuery(id+"F10.imprint","IMPRINT",FACE,{"disambiguationData":[TD([[makeQuery(id+"F10.imprint","IMPRINT",EDGE,{"derivedFrom":subQ3}),-1.0]])]});}
            var Q15;
            {var subQ4=sQuery(id+"F10.wireOp",EDGE,"E45.bottom");var subQ6=sQuery(id+"F10.wireOp",EDGE,"E44.left");var subQ9=makeQuery(id+"F10.imprint","INTERSECT",VERTEX,{"derivedFrom":[subQ6,subQ4]});Q15=makeQuery(id+"F10.imprint","IMPRINT",FACE,{"disambiguationData":[TD([[makeQuery(id+"F10.imprint","IMPRINT",EDGE,{"disambiguationData":[TD([[subQ9,-1.0]])],"derivedFrom":subQ6}),-1.0]])]});}
            var Q16;
            {var subQ3=sQuery(id+"F10.wireOp",EDGE,"E46");Q16=makeQuery(id+"F10.imprint","IMPRINT",FACE,{"disambiguationData":[TD([[makeQuery(id+"F10.imprint","IMPRINT",EDGE,{"derivedFrom":subQ3}),1.0]])]});}
            extrude(context, id + "F11", {"entities" : qUnion([Q0, Q1, Q2, Q3, Q4, Q5, Q6, Q7, Q8, Q9, Q10, Q11, Q12, Q13, Q14, Q15, Q16]), "operationType" : NewBodyOperationType.REMOVE, "oppositeDirection" : true, "depth" : 2.54 * mm, "offsetDistance" : 25.4 * mm});
        }
        {
            var Q0;
            Q0=makeQuery(id+"F4.opChamfer","BLEND_FACE",FACE,{"disambiguationData":[OSD([sQuery(id+"F2.wireOp",EDGE,"E1.right")])]});
            var sketch = newSketch(context, id + "F12", { "sketchPlane" : qUnion([Q0])});
            skLineSegment(sketch, "E56", {"start": v(23.34, 31.68) * mm, "end": v(-23.2, 31.68) * mm});
            skLineSegment(sketch, "E57.top", {"start": v(7.98, 25.04) * mm, "end": v(-7.96, 25.04) * mm});
            skLineSegment(sketch, "E57.left", {"start": v(7.98, 38.32) * mm, "end": v(7.98, 25.04) * mm});
            skLineSegment(sketch, "E57.right", {"start": v(-7.96, 38.32) * mm, "end": v(-7.96, 25.04) * mm});
            skPoint(sketch, "E57.middle", {"position": v(0, 31.68) * mm});
            skLineSegment(sketch, "E58.top", {"start": v(6.23, 26.7) * mm, "end": v(-6.21, 26.7) * mm});
            skLineSegment(sketch, "E58.left", {"start": v(6.23, 36.67) * mm, "end": v(6.23, 26.7) * mm});
            skLineSegment(sketch, "E58.right", {"start": v(-6.21, 36.67) * mm, "end": v(-6.21, 26.7) * mm});
            skLineSegment(sketch, "E59", {"start": v(6.23, 36.67) * mm, "end": v(7.98, 31.68) * mm});
            skLineSegment(sketch, "E60", {"start": v(-6.21, 36.67) * mm, "end": v(-7.96, 31.68) * mm});
            skLineSegment(sketch, "E61", {"start": v(27.07, 1.54) * mm, "end": v(-26.68, 1.54) * mm});
            skLineSegment(sketch, "E62.bottom", {"start": v(3.25, 1.54) * mm, "end": v(-3.23, 1.54) * mm});
            skLineSegment(sketch, "E62.top", {"start": v(3.25, -6) * mm, "end": v(-3.23, -6) * mm});
            skLineSegment(sketch, "E62.left", {"start": v(3.25, 1.54) * mm, "end": v(3.25, -6) * mm});
            skLineSegment(sketch, "E62.right", {"start": v(-3.23, 1.54) * mm, "end": v(-3.23, -6) * mm});
            skPoint(sketch, "E62.middle", {"position": v(0, -2.23) * mm});
            skLineSegment(sketch, "E63.bottom", {"start": v(6.28, 1.54) * mm, "end": v(-6.26, 1.54) * mm});
            skLineSegment(sketch, "E63.top", {"start": v(6.28, -6) * mm, "end": v(-6.26, -6) * mm});
            skLineSegment(sketch, "E63.left", {"start": v(6.28, 1.54) * mm, "end": v(6.28, -6) * mm});
            skLineSegment(sketch, "E63.right", {"start": v(-6.26, 1.54) * mm, "end": v(-6.26, -6) * mm});
            skLineSegment(sketch, "E64", {"start": v(3.25, -2.23) * mm, "end": v(6.28, 1.54) * mm});
            skLineSegment(sketch, "E65", {"start": v(-3.23, -2.23) * mm, "end": v(-6.26, 1.54) * mm});
            skLineSegment(sketch, "E66", {"start": v(0, 42.47) * mm, "end": v(0, 2.2) * mm});
            skPoint(sketch, "E66.startSnap0", {"position": v(0, 42.47) * mm});
            skLineSegment(sketch, "E67", {"start": v(-23.2, 31.68) * mm, "end": v(-25.73, 31.68) * mm});
            skLineSegment(sketch, "E68", {"start": v(-26.68, 1.54) * mm, "end": v(-25.73, 31.68) * mm});
            skLineSegment(sketch, "E69", {"start": v(23.34, 31.68) * mm, "end": v(26, 31.68) * mm});
            skLineSegment(sketch, "E70", {"start": v(27.07, 1.54) * mm, "end": v(26, 31.68) * mm});
            skLineSegment(sketch, "E71", {"start": v(-7.96, 31.68) * mm, "end": v(-2.14, 48.28) * mm});
            skLineSegment(sketch, "E72", {"start": v(7.98, 31.68) * mm, "end": v(2.25, 48.04) * mm});
            skLineSegment(sketch, "E73", {"start": v(-2.14, 48.28) * mm, "end": v(2.25, 48.04) * mm});
            skSolve(sketch);
        }
        {
            var Q0;
            {var subQ0=sQuery(id+"F12.wireOp",EDGE,"E72");var subQ3=sQuery(id+"F12.wireOp",EDGE,"E58.left");var subQ5=makeQuery(id+"F12.imprint","INTERSECT",VERTEX,{"derivedFrom":[subQ3,subQ0]});Q0=makeQuery(id+"F12.imprint","IMPRINT",FACE,{"disambiguationData":[TD([[makeQuery(id+"F12.imprint","IMPRINT",EDGE,{"disambiguationData":[TD([[subQ5,-1.0]])],"derivedFrom":subQ3}),1.0]])]});}
            var Q1;
            {var subQ0=sQuery(id+"F12.wireOp",EDGE,"E71");var subQ3=sQuery(id+"F12.wireOp",EDGE,"E58.right");var subQ5=makeQuery(id+"F12.imprint","INTERSECT",VERTEX,{"derivedFrom":[subQ3,subQ0]});Q1=makeQuery(id+"F12.imprint","IMPRINT",FACE,{"disambiguationData":[TD([[makeQuery(id+"F12.imprint","IMPRINT",EDGE,{"disambiguationData":[TD([[subQ5,-1.0]])],"derivedFrom":subQ3}),-1.0]])]});}
            var Q2;
            {var subQ3=sQuery(id+"F12.wireOp",EDGE,"E64");Q2=makeQuery(id+"F12.imprint","IMPRINT",FACE,{"disambiguationData":[TD([[makeQuery(id+"F12.imprint","IMPRINT",EDGE,{"derivedFrom":subQ3}),1.0]])]});}
            var Q3;
            {var subQ3=sQuery(id+"F12.wireOp",EDGE,"E65");Q3=makeQuery(id+"F12.imprint","IMPRINT",FACE,{"disambiguationData":[TD([[makeQuery(id+"F12.imprint","IMPRINT",EDGE,{"derivedFrom":subQ3}),-1.0]])]});}
            var Q4;
            {var subQ0=sQuery(id+"F12.wireOp",EDGE,"E57.left");var subQ1=sQuery(id+"F12.wireOp",EDGE,"E57.top");var subQ2=makeQuery(id+"F12.imprint","INTERSECT",VERTEX,{"derivedFrom":[subQ1,subQ0]});Q4=makeQuery(id+"F12.imprint","IMPRINT",FACE,{"disambiguationData":[TD([[makeQuery(id+"F12.imprint","IMPRINT",EDGE,{"disambiguationData":[TD([[subQ2,-1.0]])],"derivedFrom":subQ1}),-1.0]])]});}
            var Q5;
            {var subQ5=sQuery(id+"F12.wireOp",EDGE,"E57.right");var subQ6=sQuery(id+"F12.wireOp",EDGE,"E57.top");var subQ7=makeQuery(id+"F12.imprint","INTERSECT",VERTEX,{"derivedFrom":[subQ6,subQ5]});Q5=makeQuery(id+"F12.imprint","IMPRINT",FACE,{"disambiguationData":[TD([[makeQuery(id+"F12.imprint","IMPRINT",EDGE,{"disambiguationData":[TD([[subQ7,1.0]])],"derivedFrom":subQ6}),-1.0]])]});}
            var Q6;
            {var subQ4=sQuery(id+"F12.wireOp",EDGE,"E63.bottom");var subQ6=sQuery(id+"F12.wireOp",EDGE,"E62.left");var subQ9=makeQuery(id+"F12.imprint","INTERSECT",VERTEX,{"derivedFrom":[subQ6,subQ4]});Q6=makeQuery(id+"F12.imprint","IMPRINT",FACE,{"disambiguationData":[TD([[makeQuery(id+"F12.imprint","IMPRINT",EDGE,{"disambiguationData":[TD([[subQ9,-1.0]])],"derivedFrom":subQ6}),-1.0]])]});}
            var Q7;
            {var subQ1=sQuery(id+"F12.wireOp",EDGE,"E58.left");var subQ7=sQuery(id+"F12.wireOp",EDGE,"E56");var subQ10=makeQuery(id+"F12.imprint","INTERSECT",VERTEX,{"derivedFrom":[subQ7,subQ1]});Q7=makeQuery(id+"F12.imprint","IMPRINT",FACE,{"disambiguationData":[TD([[makeQuery(id+"F12.imprint","IMPRINT",EDGE,{"disambiguationData":[TD([[subQ10,-1.0]])],"derivedFrom":subQ7}),-1.0]])]});}
            var Q8;
            {var subQ6=sQuery(id+"F12.wireOp",EDGE,"E56");var subQ8=sQuery(id+"F12.wireOp",EDGE,"E66");var subQ9=makeQuery(id+"F12.imprint","INTERSECT",VERTEX,{"derivedFrom":[subQ6,subQ8]});Q8=makeQuery(id+"F12.imprint","IMPRINT",FACE,{"disambiguationData":[TD([[makeQuery(id+"F12.imprint","IMPRINT",EDGE,{"disambiguationData":[TD([[subQ9,-1.0]])],"derivedFrom":subQ6}),-1.0]])]});}
            var Q9;
            {var subQ0=sQuery(id+"F12.wireOp",EDGE,"E73");Q9=makeQuery(id+"F12.imprint","IMPRINT",FACE,{"disambiguationData":[TD([[makeQuery(id+"F12.imprint","IMPRINT",EDGE,{"derivedFrom":subQ0}),-1.0]])]});}
            var Q10;
            {var subQ1=sQuery(id+"F12.wireOp",EDGE,"E57.top");var subQ7=sQuery(id+"F12.wireOp",EDGE,"E57.left");var subQ8=makeQuery(id+"F12.imprint","INTERSECT",VERTEX,{"derivedFrom":[subQ1,subQ7]});Q10=makeQuery(id+"F12.imprint","IMPRINT",FACE,{"disambiguationData":[TD([[makeQuery(id+"F12.imprint","IMPRINT",EDGE,{"disambiguationData":[TD([[subQ8,-1.0]])],"derivedFrom":subQ1}),1.0]])]});}
            var Q11;
            {var subQ1=sQuery(id+"F12.wireOp",EDGE,"E57.top");var subQ7=sQuery(id+"F12.wireOp",EDGE,"E57.right");var subQ8=makeQuery(id+"F12.imprint","INTERSECT",VERTEX,{"derivedFrom":[subQ1,subQ7]});Q11=makeQuery(id+"F12.imprint","IMPRINT",FACE,{"disambiguationData":[TD([[makeQuery(id+"F12.imprint","IMPRINT",EDGE,{"disambiguationData":[TD([[subQ8,1.0]])],"derivedFrom":subQ1}),1.0]])]});}
            var Q12;
            {var subQ1=sQuery(id+"F12.wireOp",EDGE,"E67");Q12=makeQuery(id+"F12.imprint","IMPRINT",FACE,{"disambiguationData":[TD([[makeQuery(id+"F12.imprint","IMPRINT",EDGE,{"derivedFrom":subQ1}),1.0]])]});}
            var Q13;
            {var subQ0=sQuery(id+"F12.wireOp",EDGE,"E66");var subQ1=sQuery(id+"F12.wireOp",EDGE,"E56");var subQ2=makeQuery(id+"F12.imprint","INTERSECT",VERTEX,{"derivedFrom":[subQ1,subQ0]});Q13=makeQuery(id+"F12.imprint","IMPRINT",FACE,{"disambiguationData":[TD([[makeQuery(id+"F12.imprint","IMPRINT",EDGE,{"disambiguationData":[TD([[subQ2,-1.0]])],"derivedFrom":subQ1}),1.0]])]});}
            var Q14;
            {var subQ0=sQuery(id+"F12.wireOp",EDGE,"E58.left");var subQ1=sQuery(id+"F12.wireOp",EDGE,"E56");var subQ2=makeQuery(id+"F12.imprint","INTERSECT",VERTEX,{"derivedFrom":[subQ1,subQ0]});Q14=makeQuery(id+"F12.imprint","IMPRINT",FACE,{"disambiguationData":[TD([[makeQuery(id+"F12.imprint","IMPRINT",EDGE,{"disambiguationData":[TD([[subQ2,-1.0]])],"derivedFrom":subQ1}),1.0]])]});}
            extrude(context, id + "F13", {"entities" : qUnion([Q0, Q1, Q2, Q3, Q4, Q5, Q6, Q7, Q8, Q9, Q10, Q11, Q12, Q13, Q14]), "operationType" : NewBodyOperationType.REMOVE, "oppositeDirection" : true, "depth" : 2.54 * mm, "offsetDistance" : 25.4 * mm});
        }
        {
            var Q0;
            Q0=makeQuery(id+"F3.opExtrude","CAP_FACE",FACE,{"disambiguationData":[OSD([sQuery(id+"F2.wireOp",EDGE,"E1.bottom"),sQuery(id+"F2.wireOp",EDGE,"E1.top"),sQuery(id+"F2.wireOp",EDGE,"E1.left"),sQuery(id+"F2.wireOp",EDGE,"E1.right")])],"isStart":true});
            var sketch = newSketch(context, id + "F14", { "sketchPlane" : qUnion([Q0])});
            skLineSegment(sketch, "E74.bottom", {"start": v(-9.52, 9.53) * mm, "end": v(9.53, 9.53) * mm});
            skLineSegment(sketch, "E74.top", {"start": v(-9.53, -9.53) * mm, "end": v(9.52, -9.53) * mm});
            skLineSegment(sketch, "E74.left", {"start": v(-9.52, 9.53) * mm, "end": v(-9.53, -9.53) * mm});
            skLineSegment(sketch, "E74.right", {"start": v(9.53, 9.53) * mm, "end": v(9.52, -9.53) * mm});
            skPoint(sketch, "E74.middle", {"position": v(0, 0) * mm});
            skLineSegment(sketch, "E75.bottom", {"start": v(-25.4, 22.16) * mm, "end": v(25.4, 22.16) * mm});
            skLineSegment(sketch, "E75.top", {"start": v(-25.4, -22.16) * mm, "end": v(25.4, -22.16) * mm});
            skLineSegment(sketch, "E75.left", {"start": v(-25.4, 22.16) * mm, "end": v(-25.4, -22.16) * mm});
            skLineSegment(sketch, "E75.right", {"start": v(25.4, 22.16) * mm, "end": v(25.4, -22.16) * mm});
            skPoint(sketch, "E75.cornerSnap0", {"position": v(-22.16, 22.16) * mm});
            skLineSegment(sketch, "E76.bottom", {"start": v(-22.16, 25.4) * mm, "end": v(22.16, 25.4) * mm});
            skLineSegment(sketch, "E76.top", {"start": v(-22.16, -25.4) * mm, "end": v(22.16, -25.4) * mm});
            skLineSegment(sketch, "E76.left", {"start": v(-22.16, 25.4) * mm, "end": v(-22.16, -25.4) * mm});
            skLineSegment(sketch, "E76.right", {"start": v(22.16, 25.4) * mm, "end": v(22.16, -25.4) * mm});
            skLineSegment(sketch, "E77", {"start": v(0, 0) * mm, "end": v(-25.4, 22.16) * mm});
            skLineSegment(sketch, "E78", {"start": v(0, 0) * mm, "end": v(-22.16, 25.4) * mm});
            skLineSegment(sketch, "E79", {"start": v(0, 0) * mm, "end": v(-25.4, -22.16) * mm});
            skLineSegment(sketch, "E80", {"start": v(0, 0) * mm, "end": v(-22.16, -25.4) * mm});
            skLineSegment(sketch, "E81", {"start": v(0, 0) * mm, "end": v(22.16, 25.4) * mm});
            skLineSegment(sketch, "E82", {"start": v(0, 0) * mm, "end": v(25.4, 22.16) * mm});
            skLineSegment(sketch, "E83", {"start": v(0, 0) * mm, "end": v(25.4, -22.16) * mm});
            skLineSegment(sketch, "E84", {"start": v(0, 0) * mm, "end": v(22.16, -25.4) * mm});
            skSolve(sketch);
        }
        {
            var Q0;
            {var subQ0=sQuery(id+"F14.wireOp",EDGE,"E80");var subQ1=sQuery(id+"F14.wireOp",EDGE,"E74.top");var subQ2=makeQuery(id+"F14.imprint","INTERSECT",VERTEX,{"derivedFrom":[subQ1,subQ0]});Q0=makeQuery(id+"F14.imprint","IMPRINT",FACE,{"disambiguationData":[TD([[makeQuery(id+"F14.imprint","IMPRINT",EDGE,{"disambiguationData":[TD([[subQ2,-1.0]])],"derivedFrom":subQ1}),-1.0]])]});}
            var sketch = newSketch(context, id + "F15", { "sketchPlane" : qUnion([Q0])});
            skLineSegment(sketch, "E85.bottom", {"start": v(-31.75, 31.75) * mm, "end": v(31.75, 31.75) * mm});
            skLineSegment(sketch, "E85.top", {"start": v(-31.75, -31.75) * mm, "end": v(31.75, -31.75) * mm});
            skLineSegment(sketch, "E85.left", {"start": v(-31.75, 31.75) * mm, "end": v(-31.75, -31.75) * mm});
            skLineSegment(sketch, "E85.right", {"start": v(31.75, 31.75) * mm, "end": v(31.75, -31.75) * mm});
            skPoint(sketch, "E85.middle", {"position": v(0, 0) * mm});
            skSolve(sketch);
        }
        {
            var Q0;
            Q0 = qSketchRegion(id + "F15", true);
            extrude(context, id + "F16", {"entities" : qUnion([Q0]), "operationType" : NewBodyOperationType.ADD, "depth" : 12.7 * mm, "offsetDistance" : 25.4 * mm});
        }
        {
            var Q0;
            Q0=makeQuery(id+"F16.opExtrude","CAP_FACE",FACE,{"disambiguationData":[OSD([sQuery(id+"F15.wireOp",EDGE,"E85.bottom"),sQuery(id+"F15.wireOp",EDGE,"E85.top"),sQuery(id+"F15.wireOp",EDGE,"E85.left"),sQuery(id+"F15.wireOp",EDGE,"E85.right")])],"isStart":false});
            var sketch = newSketch(context, id + "F17", { "sketchPlane" : qUnion([Q0])});
            skLineSegment(sketch, "E86.bottom", {"start": v(-12.7, 12.7) * mm, "end": v(12.7, 12.7) * mm});
            skLineSegment(sketch, "E86.top", {"start": v(-12.7, -12.7) * mm, "end": v(12.7, -12.7) * mm});
            skLineSegment(sketch, "E86.left", {"start": v(-12.7, 12.7) * mm, "end": v(-12.7, -12.7) * mm});
            skLineSegment(sketch, "E86.right", {"start": v(12.7, 12.7) * mm, "end": v(12.7, -12.7) * mm});
            skPoint(sketch, "E86.middle", {"position": v(0, 0) * mm});
            skLineSegment(sketch, "E87.bottom", {"start": v(-25.48, 31.75) * mm, "end": v(25.48, 31.75) * mm});
            skLineSegment(sketch, "E87.top", {"start": v(-25.48, -31.75) * mm, "end": v(25.48, -31.75) * mm});
            skLineSegment(sketch, "E87.left", {"start": v(-25.48, 31.75) * mm, "end": v(-25.48, -31.75) * mm});
            skLineSegment(sketch, "E87.right", {"start": v(25.48, 31.75) * mm, "end": v(25.48, -31.75) * mm});
            skPoint(sketch, "E87.cornerSnap0", {"position": v(-31.75, 31.75) * mm});
            skLineSegment(sketch, "E88.bottom", {"start": v(-31.75, 25.48) * mm, "end": v(31.75, 25.48) * mm});
            skLineSegment(sketch, "E88.top", {"start": v(-31.75, -25.48) * mm, "end": v(31.75, -25.48) * mm});
            skLineSegment(sketch, "E88.left", {"start": v(-31.75, 25.48) * mm, "end": v(-31.75, -25.48) * mm});
            skLineSegment(sketch, "E88.right", {"start": v(31.75, 25.48) * mm, "end": v(31.75, -25.48) * mm});
            skLineSegment(sketch, "E89", {"start": v(0, 0) * mm, "end": v(-25.48, 31.75) * mm});
            skLineSegment(sketch, "E90", {"start": v(0, 0) * mm, "end": v(-31.75, 25.48) * mm});
            skLineSegment(sketch, "E91", {"start": v(0, 0) * mm, "end": v(-25.48, -31.75) * mm});
            skLineSegment(sketch, "E92", {"start": v(0, 0) * mm, "end": v(-31.75, -25.48) * mm});
            skLineSegment(sketch, "E93", {"start": v(0, 0) * mm, "end": v(31.75, 25.48) * mm});
            skLineSegment(sketch, "E94", {"start": v(0, 0) * mm, "end": v(25.48, 31.75) * mm});
            skLineSegment(sketch, "E95", {"start": v(0, 0) * mm, "end": v(25.48, -31.75) * mm});
            skLineSegment(sketch, "E96", {"start": v(0, 0) * mm, "end": v(31.75, -25.48) * mm});
            skLineSegment(sketch, "E97.bottom", {"start": v(-17.78, -17.78) * mm, "end": v(17.78, -17.78) * mm});
            skLineSegment(sketch, "E97.top", {"start": v(-17.78, 17.78) * mm, "end": v(17.78, 17.78) * mm});
            skLineSegment(sketch, "E97.left", {"start": v(-17.78, -17.78) * mm, "end": v(-17.78, 17.78) * mm});
            skLineSegment(sketch, "E97.right", {"start": v(17.78, -17.78) * mm, "end": v(17.78, 17.78) * mm});
            skLineSegment(sketch, "E98.bottom", {"start": v(-26.67, -26.67) * mm, "end": v(26.67, -26.67) * mm});
            skLineSegment(sketch, "E98.top", {"start": v(-26.67, 26.67) * mm, "end": v(26.67, 26.67) * mm});
            skLineSegment(sketch, "E98.left", {"start": v(-26.67, -26.67) * mm, "end": v(-26.67, 26.67) * mm});
            skLineSegment(sketch, "E98.right", {"start": v(26.67, -26.67) * mm, "end": v(26.67, 26.67) * mm});
            skLineSegment(sketch, "E99", {"start": v(0, 0) * mm, "end": v(-7.62, 0) * mm});
            skLineSegment(sketch, "E100", {"start": v(-31.75, 25.48) * mm, "end": v(-31.75, 19.13) * mm});
            skLineSegment(sketch, "E101", {"start": v(-7.62, 0) * mm, "end": v(-31.75, 19.13) * mm});
            skLineSegment(sketch, "E102", {"start": v(-31.75, -25.48) * mm, "end": v(-31.75, -19.13) * mm});
            skLineSegment(sketch, "E103", {"start": v(-25.48, -31.75) * mm, "end": v(-19.13, -31.75) * mm});
            skLineSegment(sketch, "E104", {"start": v(25.48, -31.75) * mm, "end": v(19.13, -31.75) * mm});
            skLineSegment(sketch, "E105", {"start": v(31.75, -25.48) * mm, "end": v(31.75, -19.13) * mm});
            skLineSegment(sketch, "E106", {"start": v(31.75, 25.48) * mm, "end": v(31.75, 19.13) * mm});
            skLineSegment(sketch, "E107", {"start": v(25.48, 31.75) * mm, "end": v(19.13, 31.75) * mm});
            skLineSegment(sketch, "E108", {"start": v(-25.48, 31.75) * mm, "end": v(-19.13, 31.75) * mm});
            skLineSegment(sketch, "E109", {"start": v(0, 0) * mm, "end": v(0, 7.62) * mm});
            skLineSegment(sketch, "E110", {"start": v(0, 0) * mm, "end": v(7.62, 0) * mm});
            skLineSegment(sketch, "E111", {"start": v(0, 0) * mm, "end": v(0, -7.62) * mm});
            skLineSegment(sketch, "E112", {"start": v(-7.62, 0) * mm, "end": v(-31.75, -19.13) * mm});
            skLineSegment(sketch, "E113", {"start": v(0, 7.62) * mm, "end": v(-19.13, 31.75) * mm});
            skLineSegment(sketch, "E114", {"start": v(0, 7.62) * mm, "end": v(19.13, 31.75) * mm});
            skLineSegment(sketch, "E115", {"start": v(0, -7.62) * mm, "end": v(-19.13, -31.75) * mm});
            skLineSegment(sketch, "E116", {"start": v(0, -7.62) * mm, "end": v(19.13, -31.75) * mm});
            skLineSegment(sketch, "E117", {"start": v(7.62, 0) * mm, "end": v(31.75, 19.13) * mm});
            skLineSegment(sketch, "E118", {"start": v(7.62, 0) * mm, "end": v(31.75, -19.13) * mm});
            skSolve(sketch);
        }
        {
            var Q0;
            {var subQ0=sQuery(id+"F17.wireOp",EDGE,"E87.bottom");Q0=makeQuery(id+"F17.imprint","IMPRINT",FACE,{"disambiguationData":[TD([[makeQuery(id+"F17.imprint","IMPRINT",EDGE,{"derivedFrom":subQ0}),-1.0]])]});}
            var Q1;
            {var subQ0=sQuery(id+"F17.wireOp",EDGE,"E108");Q1=makeQuery(id+"F17.imprint","IMPRINT",FACE,{"disambiguationData":[TD([[makeQuery(id+"F17.imprint","IMPRINT",EDGE,{"derivedFrom":subQ0}),-1.0]])]});}
            var Q2;
            {var subQ0=sQuery(id+"F17.wireOp",EDGE,"E89");var subQ1=sQuery(id+"F17.wireOp",EDGE,"E88.bottom");var subQ2=makeQuery(id+"F17.imprint","INTERSECT",VERTEX,{"derivedFrom":[subQ1,subQ0]});Q2=makeQuery(id+"F17.imprint","IMPRINT",FACE,{"disambiguationData":[TD([[makeQuery(id+"F17.imprint","IMPRINT",EDGE,{"disambiguationData":[TD([[subQ2,-1.0]])],"derivedFrom":subQ1}),1.0]])]});}
            var Q3;
            {var subQ0=sQuery(id+"F17.wireOp",EDGE,"E89");var subQ1=sQuery(id+"F17.wireOp",EDGE,"E88.bottom");var subQ2=makeQuery(id+"F17.imprint","INTERSECT",VERTEX,{"derivedFrom":[subQ1,subQ0]});Q3=makeQuery(id+"F17.imprint","IMPRINT",FACE,{"disambiguationData":[TD([[makeQuery(id+"F17.imprint","IMPRINT",EDGE,{"disambiguationData":[TD([[subQ2,-1.0]])],"derivedFrom":subQ1}),-1.0]])]});}
            var Q4;
            {var subQ0=sQuery(id+"F17.wireOp",EDGE,"E89");var subQ1=sQuery(id+"F17.wireOp",EDGE,"E86.bottom");var subQ2=makeQuery(id+"F17.imprint","INTERSECT",VERTEX,{"derivedFrom":[subQ1,subQ0]});Q4=makeQuery(id+"F17.imprint","IMPRINT",FACE,{"disambiguationData":[TD([[makeQuery(id+"F17.imprint","IMPRINT",EDGE,{"disambiguationData":[TD([[subQ2,-1.0]])],"derivedFrom":subQ1}),1.0]])]});}
            var Q5;
            {var subQ0=sQuery(id+"F17.wireOp",EDGE,"E113");var subQ1=sQuery(id+"F17.wireOp",EDGE,"E86.bottom");var subQ2=makeQuery(id+"F17.imprint","INTERSECT",VERTEX,{"derivedFrom":[subQ1,subQ0]});Q5=makeQuery(id+"F17.imprint","IMPRINT",FACE,{"disambiguationData":[TD([[makeQuery(id+"F17.imprint","IMPRINT",EDGE,{"disambiguationData":[TD([[subQ2,-1.0]])],"derivedFrom":subQ1}),1.0]])]});}
            var Q6;
            {var subQ0=sQuery(id+"F17.wireOp",EDGE,"E114");var subQ1=sQuery(id+"F17.wireOp",EDGE,"E86.bottom");var subQ2=makeQuery(id+"F17.imprint","INTERSECT",VERTEX,{"derivedFrom":[subQ1,subQ0]});Q6=makeQuery(id+"F17.imprint","IMPRINT",FACE,{"disambiguationData":[TD([[makeQuery(id+"F17.imprint","IMPRINT",EDGE,{"disambiguationData":[TD([[subQ2,-1.0]])],"derivedFrom":subQ1}),1.0]])]});}
            var Q7;
            {var subQ0=sQuery(id+"F17.wireOp",EDGE,"E114");var subQ1=sQuery(id+"F17.wireOp",EDGE,"E88.bottom");var subQ2=makeQuery(id+"F17.imprint","INTERSECT",VERTEX,{"derivedFrom":[subQ1,subQ0]});Q7=makeQuery(id+"F17.imprint","IMPRINT",FACE,{"disambiguationData":[TD([[makeQuery(id+"F17.imprint","IMPRINT",EDGE,{"disambiguationData":[TD([[subQ2,-1.0]])],"derivedFrom":subQ1}),-1.0]])]});}
            var Q8;
            {var subQ0=sQuery(id+"F17.wireOp",EDGE,"E114");var subQ1=sQuery(id+"F17.wireOp",EDGE,"E88.bottom");var subQ2=makeQuery(id+"F17.imprint","INTERSECT",VERTEX,{"derivedFrom":[subQ1,subQ0]});Q8=makeQuery(id+"F17.imprint","IMPRINT",FACE,{"disambiguationData":[TD([[makeQuery(id+"F17.imprint","IMPRINT",EDGE,{"disambiguationData":[TD([[subQ2,-1.0]])],"derivedFrom":subQ1}),1.0]])]});}
            var Q9;
            {var subQ0=sQuery(id+"F17.wireOp",EDGE,"E107");Q9=makeQuery(id+"F17.imprint","IMPRINT",FACE,{"disambiguationData":[TD([[makeQuery(id+"F17.imprint","IMPRINT",EDGE,{"derivedFrom":subQ0}),-1.0]])]});}
            var Q10;
            {var subQ0=sQuery(id+"F17.wireOp",EDGE,"E90");var subQ1=sQuery(id+"F17.wireOp",EDGE,"E86.left");var subQ2=makeQuery(id+"F17.imprint","INTERSECT",VERTEX,{"derivedFrom":[subQ1,subQ0]});Q10=makeQuery(id+"F17.imprint","IMPRINT",FACE,{"disambiguationData":[TD([[makeQuery(id+"F17.imprint","IMPRINT",EDGE,{"disambiguationData":[TD([[subQ2,-1.0]])],"derivedFrom":subQ1}),-1.0]])]});}
            var Q11;
            {var subQ0=sQuery(id+"F17.wireOp",EDGE,"E90");var subQ1=sQuery(id+"F17.wireOp",EDGE,"E87.left");var subQ2=makeQuery(id+"F17.imprint","INTERSECT",VERTEX,{"derivedFrom":[subQ1,subQ0]});Q11=makeQuery(id+"F17.imprint","IMPRINT",FACE,{"disambiguationData":[TD([[makeQuery(id+"F17.imprint","IMPRINT",EDGE,{"disambiguationData":[TD([[subQ2,-1.0]])],"derivedFrom":subQ1}),1.0]])]});}
            var Q12;
            {var subQ0=sQuery(id+"F17.wireOp",EDGE,"E90");var subQ1=sQuery(id+"F17.wireOp",EDGE,"E87.left");var subQ2=makeQuery(id+"F17.imprint","INTERSECT",VERTEX,{"derivedFrom":[subQ1,subQ0]});Q12=makeQuery(id+"F17.imprint","IMPRINT",FACE,{"disambiguationData":[TD([[makeQuery(id+"F17.imprint","IMPRINT",EDGE,{"disambiguationData":[TD([[subQ2,-1.0]])],"derivedFrom":subQ1}),-1.0]])]});}
            var Q13;
            {var subQ0=sQuery(id+"F17.wireOp",EDGE,"E100");Q13=makeQuery(id+"F17.imprint","IMPRINT",FACE,{"disambiguationData":[TD([[makeQuery(id+"F17.imprint","IMPRINT",EDGE,{"derivedFrom":subQ0}),1.0]])]});}
            var Q14;
            {var subQ0=sQuery(id+"F17.wireOp",EDGE,"E88.left");Q14=makeQuery(id+"F17.imprint","IMPRINT",FACE,{"disambiguationData":[TD([[makeQuery(id+"F17.imprint","IMPRINT",EDGE,{"derivedFrom":subQ0}),1.0]])]});}
            var Q15;
            {var subQ0=sQuery(id+"F17.wireOp",EDGE,"E101");var subQ1=sQuery(id+"F17.wireOp",EDGE,"E86.left");var subQ2=makeQuery(id+"F17.imprint","INTERSECT",VERTEX,{"derivedFrom":[subQ1,subQ0]});Q15=makeQuery(id+"F17.imprint","IMPRINT",FACE,{"disambiguationData":[TD([[makeQuery(id+"F17.imprint","IMPRINT",EDGE,{"disambiguationData":[TD([[subQ2,-1.0]])],"derivedFrom":subQ1}),-1.0]])]});}
            var Q16;
            {var subQ0=sQuery(id+"F17.wireOp",EDGE,"E112");var subQ1=sQuery(id+"F17.wireOp",EDGE,"E87.left");var subQ2=makeQuery(id+"F17.imprint","INTERSECT",VERTEX,{"derivedFrom":[subQ1,subQ0]});Q16=makeQuery(id+"F17.imprint","IMPRINT",FACE,{"disambiguationData":[TD([[makeQuery(id+"F17.imprint","IMPRINT",EDGE,{"disambiguationData":[TD([[subQ2,-1.0]])],"derivedFrom":subQ1}),1.0]])]});}
            var Q17;
            {var subQ0=sQuery(id+"F17.wireOp",EDGE,"E112");var subQ1=sQuery(id+"F17.wireOp",EDGE,"E86.left");var subQ2=makeQuery(id+"F17.imprint","INTERSECT",VERTEX,{"derivedFrom":[subQ1,subQ0]});Q17=makeQuery(id+"F17.imprint","IMPRINT",FACE,{"disambiguationData":[TD([[makeQuery(id+"F17.imprint","IMPRINT",EDGE,{"disambiguationData":[TD([[subQ2,-1.0]])],"derivedFrom":subQ1}),-1.0]])]});}
            var Q18;
            {var subQ0=sQuery(id+"F17.wireOp",EDGE,"E102");Q18=makeQuery(id+"F17.imprint","IMPRINT",FACE,{"disambiguationData":[TD([[makeQuery(id+"F17.imprint","IMPRINT",EDGE,{"derivedFrom":subQ0}),1.0]])]});}
            var Q19;
            {var subQ0=sQuery(id+"F17.wireOp",EDGE,"E112");var subQ1=sQuery(id+"F17.wireOp",EDGE,"E87.left");var subQ2=makeQuery(id+"F17.imprint","INTERSECT",VERTEX,{"derivedFrom":[subQ1,subQ0]});Q19=makeQuery(id+"F17.imprint","IMPRINT",FACE,{"disambiguationData":[TD([[makeQuery(id+"F17.imprint","IMPRINT",EDGE,{"disambiguationData":[TD([[subQ2,-1.0]])],"derivedFrom":subQ1}),-1.0]])]});}
            var Q20;
            {var subQ0=sQuery(id+"F17.wireOp",EDGE,"E103");Q20=makeQuery(id+"F17.imprint","IMPRINT",FACE,{"disambiguationData":[TD([[makeQuery(id+"F17.imprint","IMPRINT",EDGE,{"derivedFrom":subQ0}),1.0]])]});}
            var Q21;
            {var subQ0=sQuery(id+"F17.wireOp",EDGE,"E91");var subQ1=sQuery(id+"F17.wireOp",EDGE,"E88.top");var subQ2=makeQuery(id+"F17.imprint","INTERSECT",VERTEX,{"derivedFrom":[subQ1,subQ0]});Q21=makeQuery(id+"F17.imprint","IMPRINT",FACE,{"disambiguationData":[TD([[makeQuery(id+"F17.imprint","IMPRINT",EDGE,{"disambiguationData":[TD([[subQ2,-1.0]])],"derivedFrom":subQ1}),-1.0]])]});}
            var Q22;
            {var subQ0=sQuery(id+"F17.wireOp",EDGE,"E91");var subQ1=sQuery(id+"F17.wireOp",EDGE,"E88.top");var subQ2=makeQuery(id+"F17.imprint","INTERSECT",VERTEX,{"derivedFrom":[subQ1,subQ0]});Q22=makeQuery(id+"F17.imprint","IMPRINT",FACE,{"disambiguationData":[TD([[makeQuery(id+"F17.imprint","IMPRINT",EDGE,{"disambiguationData":[TD([[subQ2,-1.0]])],"derivedFrom":subQ1}),1.0]])]});}
            var Q23;
            {var subQ0=sQuery(id+"F17.wireOp",EDGE,"E91");var subQ1=sQuery(id+"F17.wireOp",EDGE,"E86.top");var subQ2=makeQuery(id+"F17.imprint","INTERSECT",VERTEX,{"derivedFrom":[subQ1,subQ0]});Q23=makeQuery(id+"F17.imprint","IMPRINT",FACE,{"disambiguationData":[TD([[makeQuery(id+"F17.imprint","IMPRINT",EDGE,{"disambiguationData":[TD([[subQ2,-1.0]])],"derivedFrom":subQ1}),-1.0]])]});}
            var Q24;
            {var subQ0=sQuery(id+"F17.wireOp",EDGE,"E115");var subQ1=sQuery(id+"F17.wireOp",EDGE,"E86.top");var subQ2=makeQuery(id+"F17.imprint","INTERSECT",VERTEX,{"derivedFrom":[subQ1,subQ0]});Q24=makeQuery(id+"F17.imprint","IMPRINT",FACE,{"disambiguationData":[TD([[makeQuery(id+"F17.imprint","IMPRINT",EDGE,{"disambiguationData":[TD([[subQ2,-1.0]])],"derivedFrom":subQ1}),-1.0]])]});}
            var Q25;
            {var subQ0=sQuery(id+"F17.wireOp",EDGE,"E116");var subQ1=sQuery(id+"F17.wireOp",EDGE,"E86.top");var subQ2=makeQuery(id+"F17.imprint","INTERSECT",VERTEX,{"derivedFrom":[subQ1,subQ0]});Q25=makeQuery(id+"F17.imprint","IMPRINT",FACE,{"disambiguationData":[TD([[makeQuery(id+"F17.imprint","IMPRINT",EDGE,{"disambiguationData":[TD([[subQ2,-1.0]])],"derivedFrom":subQ1}),-1.0]])]});}
            var Q26;
            {var subQ0=sQuery(id+"F17.wireOp",EDGE,"E116");var subQ1=sQuery(id+"F17.wireOp",EDGE,"E88.top");var subQ2=makeQuery(id+"F17.imprint","INTERSECT",VERTEX,{"derivedFrom":[subQ1,subQ0]});Q26=makeQuery(id+"F17.imprint","IMPRINT",FACE,{"disambiguationData":[TD([[makeQuery(id+"F17.imprint","IMPRINT",EDGE,{"disambiguationData":[TD([[subQ2,-1.0]])],"derivedFrom":subQ1}),1.0]])]});}
            var Q27;
            {var subQ0=sQuery(id+"F17.wireOp",EDGE,"E116");var subQ1=sQuery(id+"F17.wireOp",EDGE,"E88.top");var subQ2=makeQuery(id+"F17.imprint","INTERSECT",VERTEX,{"derivedFrom":[subQ1,subQ0]});Q27=makeQuery(id+"F17.imprint","IMPRINT",FACE,{"disambiguationData":[TD([[makeQuery(id+"F17.imprint","IMPRINT",EDGE,{"disambiguationData":[TD([[subQ2,-1.0]])],"derivedFrom":subQ1}),-1.0]])]});}
            var Q28;
            {var subQ0=sQuery(id+"F17.wireOp",EDGE,"E104");Q28=makeQuery(id+"F17.imprint","IMPRINT",FACE,{"disambiguationData":[TD([[makeQuery(id+"F17.imprint","IMPRINT",EDGE,{"derivedFrom":subQ0}),1.0]])]});}
            var Q29;
            {var subQ0=sQuery(id+"F17.wireOp",EDGE,"E87.top");Q29=makeQuery(id+"F17.imprint","IMPRINT",FACE,{"disambiguationData":[TD([[makeQuery(id+"F17.imprint","IMPRINT",EDGE,{"derivedFrom":subQ0}),1.0]])]});}
            var Q30;
            {var subQ0=sQuery(id+"F17.wireOp",EDGE,"E105");Q30=makeQuery(id+"F17.imprint","IMPRINT",FACE,{"disambiguationData":[TD([[makeQuery(id+"F17.imprint","IMPRINT",EDGE,{"derivedFrom":subQ0}),-1.0]])]});}
            var Q31;
            {var subQ0=sQuery(id+"F17.wireOp",EDGE,"E118");var subQ1=sQuery(id+"F17.wireOp",EDGE,"E87.right");var subQ2=makeQuery(id+"F17.imprint","INTERSECT",VERTEX,{"derivedFrom":[subQ1,subQ0]});Q31=makeQuery(id+"F17.imprint","IMPRINT",FACE,{"disambiguationData":[TD([[makeQuery(id+"F17.imprint","IMPRINT",EDGE,{"disambiguationData":[TD([[subQ2,-1.0]])],"derivedFrom":subQ1}),1.0]])]});}
            var Q32;
            {var subQ0=sQuery(id+"F17.wireOp",EDGE,"E118");var subQ1=sQuery(id+"F17.wireOp",EDGE,"E87.right");var subQ2=makeQuery(id+"F17.imprint","INTERSECT",VERTEX,{"derivedFrom":[subQ1,subQ0]});Q32=makeQuery(id+"F17.imprint","IMPRINT",FACE,{"disambiguationData":[TD([[makeQuery(id+"F17.imprint","IMPRINT",EDGE,{"disambiguationData":[TD([[subQ2,-1.0]])],"derivedFrom":subQ1}),-1.0]])]});}
            var Q33;
            {var subQ0=sQuery(id+"F17.wireOp",EDGE,"E118");var subQ1=sQuery(id+"F17.wireOp",EDGE,"E86.right");var subQ2=makeQuery(id+"F17.imprint","INTERSECT",VERTEX,{"derivedFrom":[subQ1,subQ0]});Q33=makeQuery(id+"F17.imprint","IMPRINT",FACE,{"disambiguationData":[TD([[makeQuery(id+"F17.imprint","IMPRINT",EDGE,{"disambiguationData":[TD([[subQ2,-1.0]])],"derivedFrom":subQ1}),1.0]])]});}
            var Q34;
            {var subQ0=sQuery(id+"F17.wireOp",EDGE,"E117");var subQ1=sQuery(id+"F17.wireOp",EDGE,"E86.right");var subQ2=makeQuery(id+"F17.imprint","INTERSECT",VERTEX,{"derivedFrom":[subQ1,subQ0]});Q34=makeQuery(id+"F17.imprint","IMPRINT",FACE,{"disambiguationData":[TD([[makeQuery(id+"F17.imprint","IMPRINT",EDGE,{"disambiguationData":[TD([[subQ2,-1.0]])],"derivedFrom":subQ1}),1.0]])]});}
            var Q35;
            {var subQ0=sQuery(id+"F17.wireOp",EDGE,"E93");var subQ1=sQuery(id+"F17.wireOp",EDGE,"E86.right");var subQ2=makeQuery(id+"F17.imprint","INTERSECT",VERTEX,{"derivedFrom":[subQ1,subQ0]});Q35=makeQuery(id+"F17.imprint","IMPRINT",FACE,{"disambiguationData":[TD([[makeQuery(id+"F17.imprint","IMPRINT",EDGE,{"disambiguationData":[TD([[subQ2,-1.0]])],"derivedFrom":subQ1}),1.0]])]});}
            var Q36;
            {var subQ0=sQuery(id+"F17.wireOp",EDGE,"E93");var subQ1=sQuery(id+"F17.wireOp",EDGE,"E87.right");var subQ2=makeQuery(id+"F17.imprint","INTERSECT",VERTEX,{"derivedFrom":[subQ1,subQ0]});Q36=makeQuery(id+"F17.imprint","IMPRINT",FACE,{"disambiguationData":[TD([[makeQuery(id+"F17.imprint","IMPRINT",EDGE,{"disambiguationData":[TD([[subQ2,-1.0]])],"derivedFrom":subQ1}),-1.0]])]});}
            var Q37;
            {var subQ0=sQuery(id+"F17.wireOp",EDGE,"E106");Q37=makeQuery(id+"F17.imprint","IMPRINT",FACE,{"disambiguationData":[TD([[makeQuery(id+"F17.imprint","IMPRINT",EDGE,{"derivedFrom":subQ0}),-1.0]])]});}
            var Q38;
            {var subQ0=sQuery(id+"F17.wireOp",EDGE,"E93");var subQ1=sQuery(id+"F17.wireOp",EDGE,"E87.right");var subQ2=makeQuery(id+"F17.imprint","INTERSECT",VERTEX,{"derivedFrom":[subQ1,subQ0]});Q38=makeQuery(id+"F17.imprint","IMPRINT",FACE,{"disambiguationData":[TD([[makeQuery(id+"F17.imprint","IMPRINT",EDGE,{"disambiguationData":[TD([[subQ2,-1.0]])],"derivedFrom":subQ1}),1.0]])]});}
            var Q39;
            {var subQ0=sQuery(id+"F17.wireOp",EDGE,"E88.right");Q39=makeQuery(id+"F17.imprint","IMPRINT",FACE,{"disambiguationData":[TD([[makeQuery(id+"F17.imprint","IMPRINT",EDGE,{"derivedFrom":subQ0}),-1.0]])]});}
            extrude(context, id + "F18", {"entities" : qUnion([Q0, Q1, Q2, Q3, Q4, Q5, Q6, Q7, Q8, Q9, Q10, Q11, Q12, Q13, Q14, Q15, Q16, Q17, Q18, Q19, Q20, Q21, Q22, Q23, Q24, Q25, Q26, Q27, Q28, Q29, Q30, Q31, Q32, Q33, Q34, Q35, Q36, Q37, Q38, Q39]), "depth" : 25.4 * mm, "offsetDistance" : 25.4 * mm});
        }
        {
            var Q0;
            Q0=makeQuery(id+"F18.opExtrude","CAP_EDGE",EDGE,{"disambiguationData":[OSD([sQuery(id+"F17.wireOp",EDGE,"E88.left"),sQuery(id+"F17.wireOp",EDGE,"E100"),sQuery(id+"F17.wireOp",EDGE,"E102")])],"isStart":false});
            chamfer(context, id + "F19", {"entities" : qUnion([Q0]), "chamferType" : ChamferType.OFFSET_ANGLE, "width" : 13.97 * mm, "oppositeDirection" : false, "angle" : 55 * degree, "tangentPropagation" : true});
        }
        {
            var Q0;
            Q0=makeQuery(id+"F18.opExtrude","CAP_EDGE",EDGE,{"disambiguationData":[OSD([sQuery(id+"F17.wireOp",EDGE,"E87.top"),sQuery(id+"F17.wireOp",EDGE,"E103"),sQuery(id+"F17.wireOp",EDGE,"E104")])],"isStart":false});
            chamfer(context, id + "F20", {"entities" : qUnion([Q0]), "chamferType" : ChamferType.OFFSET_ANGLE, "width" : 13.97 * mm, "oppositeDirection" : false, "angle" : 55 * degree, "tangentPropagation" : true});
        }
        {
            var Q0;
            Q0=makeQuery(id+"F18.opExtrude","CAP_EDGE",EDGE,{"disambiguationData":[OSD([sQuery(id+"F17.wireOp",EDGE,"E87.bottom"),sQuery(id+"F17.wireOp",EDGE,"E107"),sQuery(id+"F17.wireOp",EDGE,"E108")])],"isStart":false});
            chamfer(context, id + "F21", {"entities" : qUnion([Q0]), "chamferType" : ChamferType.OFFSET_ANGLE, "width" : 13.97 * mm, "oppositeDirection" : true, "angle" : 55 * degree, "tangentPropagation" : true});
        }
        {
            var Q0;
            Q0=makeQuery(id+"F18.opExtrude","CAP_EDGE",EDGE,{"disambiguationData":[OSD([sQuery(id+"F17.wireOp",EDGE,"E88.right"),sQuery(id+"F17.wireOp",EDGE,"E105"),sQuery(id+"F17.wireOp",EDGE,"E106")])],"isStart":false});
            chamfer(context, id + "F22", {"entities" : qUnion([Q0]), "chamferType" : ChamferType.OFFSET_ANGLE, "width" : 13.97 * mm, "oppositeDirection" : true, "angle" : 55 * degree, "tangentPropagation" : true});
        }
        {
            var Q0;
            {var subQ0=sQuery(id+"F15.wireOp",EDGE,"E85.top");var subQ1=sQuery(id+"F15.wireOp",EDGE,"E85.bottom");var subQ2=sQuery(id+"F15.wireOp",EDGE,"E85.right");var subQ3=sQuery(id+"F15.wireOp",EDGE,"E85.left");Q0=makeQuery(id+"F18.boolean.opBoolean","SPLIT",FACE,{"disambiguationData":[TD([makeQuery(id+"F16.opExtrude","SWEPT_FACE",FACE,{"disambiguationData":[OSD([subQ1])]})])],"derivedFrom":makeQuery(id+"F16.opExtrude","CAP_FACE",FACE,{"disambiguationData":[OSD([subQ1,subQ0,subQ3,subQ2])],"isStart":false})});}
            var sketch = newSketch(context, id + "F23", { "sketchPlane" : qUnion([Q0])});
            skLineSegment(sketch, "E119.bottom", {"start": v(-31.75, 31.75) * mm, "end": v(31.75, 31.75) * mm});
            skLineSegment(sketch, "E119.top", {"start": v(-31.75, -31.75) * mm, "end": v(31.75, -31.75) * mm});
            skLineSegment(sketch, "E119.left", {"start": v(-31.75, 31.75) * mm, "end": v(-31.75, -31.75) * mm});
            skLineSegment(sketch, "E119.right", {"start": v(31.75, 31.75) * mm, "end": v(31.75, -31.75) * mm});
            skPoint(sketch, "E119.middle", {"position": v(0, 0) * mm});
            skLineSegment(sketch, "E120.bottom", {"start": v(-29.2, 29.21) * mm, "end": v(29.21, 29.21) * mm});
            skLineSegment(sketch, "E120.top", {"start": v(-29.21, -29.21) * mm, "end": v(29.2, -29.21) * mm});
            skLineSegment(sketch, "E120.left", {"start": v(-29.2, 29.21) * mm, "end": v(-29.21, -29.21) * mm});
            skLineSegment(sketch, "E120.right", {"start": v(29.21, 29.21) * mm, "end": v(29.2, -29.21) * mm});
            skSolve(sketch);
        }
        {
            var Q0;
            Q0 = qSketchRegion(id + "F23", true);
            extrude(context, id + "F24", {"entities" : qUnion([Q0]), "operationType" : NewBodyOperationType.REMOVE, "oppositeDirection" : true, "depth" : 25.4 * mm, "offsetDistance" : 25.4 * mm});
        }
        {
            var Q0;
            Q0=makeQuery(id+"F24.boolean.opBoolean","COPY",EDGE,{"derivedFrom":makeQuery(id+"F24.opExtrude","SWEPT_EDGE",EDGE,{"disambiguationData":[OSD([sQuery(id+"F23.wireOp",EDGE,"E120.bottom"),sQuery(id+"F23.wireOp",EDGE,"E120.left")])]})});
            var Q1;
            Q1=makeQuery(id+"F24.boolean.opBoolean","COPY",EDGE,{"derivedFrom":makeQuery(id+"F24.opExtrude","SWEPT_EDGE",EDGE,{"disambiguationData":[OSD([sQuery(id+"F23.wireOp",EDGE,"E120.bottom"),sQuery(id+"F23.wireOp",EDGE,"E120.right")])]})});
            var Q2;
            Q2=makeQuery(id+"F24.boolean.opBoolean","COPY",EDGE,{"derivedFrom":makeQuery(id+"F24.opExtrude","SWEPT_EDGE",EDGE,{"disambiguationData":[OSD([sQuery(id+"F23.wireOp",EDGE,"E120.top"),sQuery(id+"F23.wireOp",EDGE,"E120.left")])]})});
            var Q3;
            Q3=makeQuery(id+"F24.boolean.opBoolean","COPY",EDGE,{"derivedFrom":makeQuery(id+"F24.opExtrude","SWEPT_EDGE",EDGE,{"disambiguationData":[OSD([sQuery(id+"F23.wireOp",EDGE,"E120.top"),sQuery(id+"F23.wireOp",EDGE,"E120.right")])]})});
            chamfer(context, id + "F25", {"entities" : qUnion([Q0, Q1, Q2, Q3]), "width" : 5.77 * mm, "tangentPropagation" : true});
        }
        {
            var Q0;
            Q0=makeQuery(id+"F24.boolean.opBoolean","COPY",EDGE,{"derivedFrom":makeQuery(id+"F24.opExtrude","CAP_EDGE",EDGE,{"disambiguationData":[OSD([sQuery(id+"F23.wireOp",EDGE,"E119.left")])],"isStart":true})});
            var Q1;
            Q1=makeQuery(id+"F18.opExtrude","SWEPT_EDGE",EDGE,{"disambiguationData":[OSD([sQuery(id+"F15.wireOp",EDGE,"E85.left"),sQuery(id+"F17.wireOp",EDGE,"E88.bottom"),sQuery(id+"F17.wireOp",EDGE,"E90"),sQuery(id+"F17.wireOp",EDGE,"E100")])]});
            var Q2;
            Q2=makeQuery(id+"F18.opExtrude","SWEPT_EDGE",EDGE,{"disambiguationData":[OSD([sQuery(id+"F15.wireOp",EDGE,"E85.left"),sQuery(id+"F17.wireOp",EDGE,"E88.top"),sQuery(id+"F17.wireOp",EDGE,"E92"),sQuery(id+"F17.wireOp",EDGE,"E102")])]});
            var Q3;
            Q3=makeQuery(id+"F18.opExtrude","SWEPT_EDGE",EDGE,{"disambiguationData":[OSD([sQuery(id+"F15.wireOp",EDGE,"E85.bottom"),sQuery(id+"F17.wireOp",EDGE,"E87.left"),sQuery(id+"F17.wireOp",EDGE,"E89"),sQuery(id+"F17.wireOp",EDGE,"E108")])]});
            var Q4;
            Q4=makeQuery(id+"F24.boolean.opBoolean","COPY",EDGE,{"derivedFrom":makeQuery(id+"F24.opExtrude","CAP_EDGE",EDGE,{"disambiguationData":[OSD([sQuery(id+"F23.wireOp",EDGE,"E119.bottom")])],"isStart":true})});
            var Q5;
            Q5=makeQuery(id+"F18.opExtrude","SWEPT_EDGE",EDGE,{"disambiguationData":[OSD([sQuery(id+"F15.wireOp",EDGE,"E85.bottom"),sQuery(id+"F17.wireOp",EDGE,"E87.right"),sQuery(id+"F17.wireOp",EDGE,"E94"),sQuery(id+"F17.wireOp",EDGE,"E107")])]});
            var Q6;
            Q6=makeQuery(id+"F18.opExtrude","SWEPT_EDGE",EDGE,{"disambiguationData":[OSD([sQuery(id+"F15.wireOp",EDGE,"E85.right"),sQuery(id+"F17.wireOp",EDGE,"E88.bottom"),sQuery(id+"F17.wireOp",EDGE,"E93"),sQuery(id+"F17.wireOp",EDGE,"E106")])]});
            var Q7;
            Q7=makeQuery(id+"F24.boolean.opBoolean","COPY",EDGE,{"derivedFrom":makeQuery(id+"F24.opExtrude","CAP_EDGE",EDGE,{"disambiguationData":[OSD([sQuery(id+"F23.wireOp",EDGE,"E119.right")])],"isStart":true})});
            var Q8;
            Q8=makeQuery(id+"F18.opExtrude","SWEPT_EDGE",EDGE,{"disambiguationData":[OSD([sQuery(id+"F15.wireOp",EDGE,"E85.right"),sQuery(id+"F17.wireOp",EDGE,"E88.top"),sQuery(id+"F17.wireOp",EDGE,"E96"),sQuery(id+"F17.wireOp",EDGE,"E105")])]});
            var Q9;
            Q9=makeQuery(id+"F18.opExtrude","SWEPT_EDGE",EDGE,{"disambiguationData":[OSD([sQuery(id+"F15.wireOp",EDGE,"E85.top"),sQuery(id+"F17.wireOp",EDGE,"E87.right"),sQuery(id+"F17.wireOp",EDGE,"E95"),sQuery(id+"F17.wireOp",EDGE,"E104")])]});
            var Q10;
            Q10=makeQuery(id+"F24.boolean.opBoolean","COPY",EDGE,{"derivedFrom":makeQuery(id+"F24.opExtrude","CAP_EDGE",EDGE,{"disambiguationData":[OSD([sQuery(id+"F23.wireOp",EDGE,"E119.top")])],"isStart":true})});
            var Q11;
            Q11=makeQuery(id+"F18.opExtrude","SWEPT_EDGE",EDGE,{"disambiguationData":[OSD([sQuery(id+"F15.wireOp",EDGE,"E85.top"),sQuery(id+"F17.wireOp",EDGE,"E87.left"),sQuery(id+"F17.wireOp",EDGE,"E91"),sQuery(id+"F17.wireOp",EDGE,"E103")])]});
            fillet(context, id + "F26", {"entities" : qUnion([Q0, Q1, Q2, Q3, Q4, Q5, Q6, Q7, Q8, Q9, Q10, Q11]), "radius" : 5.08 * mm, "tangentPropagation" : true, "allowEdgeOverflow" : false});
        }
        {
            var Q0;
            Q0=makeQuery(id+"F18.opExtrude","SWEPT_EDGE",EDGE,{"disambiguationData":[OSD([sQuery(id+"F17.wireOp",EDGE,"E86.top"),sQuery(id+"F17.wireOp",EDGE,"E95")])]});
            var Q1;
            Q1=makeQuery(id+"F18.opExtrude","SWEPT_EDGE",EDGE,{"disambiguationData":[OSD([sQuery(id+"F17.wireOp",EDGE,"E86.top"),sQuery(id+"F17.wireOp",EDGE,"E91")])]});
            var Q2;
            Q2=makeQuery(id+"F18.opExtrude","SWEPT_EDGE",EDGE,{"disambiguationData":[OSD([sQuery(id+"F17.wireOp",EDGE,"E86.left"),sQuery(id+"F17.wireOp",EDGE,"E92")])]});
            var Q3;
            Q3=makeQuery(id+"F18.opExtrude","SWEPT_EDGE",EDGE,{"disambiguationData":[OSD([sQuery(id+"F17.wireOp",EDGE,"E97.bottom"),sQuery(id+"F17.wireOp",EDGE,"E115")])]});
            var Q4;
            Q4=makeQuery(id+"F18.opExtrude","SWEPT_EDGE",EDGE,{"disambiguationData":[OSD([sQuery(id+"F17.wireOp",EDGE,"E97.bottom"),sQuery(id+"F17.wireOp",EDGE,"E116")])]});
            var Q5;
            Q5=makeQuery(id+"F18.opExtrude","SWEPT_EDGE",EDGE,{"disambiguationData":[OSD([sQuery(id+"F17.wireOp",EDGE,"E97.left"),sQuery(id+"F17.wireOp",EDGE,"E112")])]});
            var Q6;
            Q6=makeQuery(id+"F18.opExtrude","SWEPT_EDGE",EDGE,{"disambiguationData":[OSD([sQuery(id+"F17.wireOp",EDGE,"E86.left"),sQuery(id+"F17.wireOp",EDGE,"E90")])]});
            var Q7;
            Q7=makeQuery(id+"F18.opExtrude","SWEPT_EDGE",EDGE,{"disambiguationData":[OSD([sQuery(id+"F17.wireOp",EDGE,"E97.top"),sQuery(id+"F17.wireOp",EDGE,"E113")])]});
            var Q8;
            Q8=makeQuery(id+"F18.opExtrude","SWEPT_EDGE",EDGE,{"disambiguationData":[OSD([sQuery(id+"F17.wireOp",EDGE,"E97.top"),sQuery(id+"F17.wireOp",EDGE,"E114")])]});
            var Q9;
            Q9=makeQuery(id+"F18.opExtrude","SWEPT_EDGE",EDGE,{"disambiguationData":[OSD([sQuery(id+"F17.wireOp",EDGE,"E86.right"),sQuery(id+"F17.wireOp",EDGE,"E93")])]});
            var Q10;
            Q10=makeQuery(id+"F18.opExtrude","SWEPT_EDGE",EDGE,{"disambiguationData":[OSD([sQuery(id+"F17.wireOp",EDGE,"E86.bottom"),sQuery(id+"F17.wireOp",EDGE,"E94")])]});
            var Q11;
            Q11=makeQuery(id+"F18.opExtrude","SWEPT_EDGE",EDGE,{"disambiguationData":[OSD([sQuery(id+"F17.wireOp",EDGE,"E97.right"),sQuery(id+"F17.wireOp",EDGE,"E117")])]});
            var Q12;
            Q12=makeQuery(id+"F18.opExtrude","SWEPT_EDGE",EDGE,{"disambiguationData":[OSD([sQuery(id+"F17.wireOp",EDGE,"E97.right"),sQuery(id+"F17.wireOp",EDGE,"E118")])]});
            var Q13;
            Q13=makeQuery(id+"F18.opExtrude","SWEPT_EDGE",EDGE,{"disambiguationData":[OSD([sQuery(id+"F17.wireOp",EDGE,"E86.right"),sQuery(id+"F17.wireOp",EDGE,"E96")])]});
            var Q14;
            Q14=makeQuery(id+"F18.opExtrude","SWEPT_EDGE",EDGE,{"disambiguationData":[OSD([sQuery(id+"F17.wireOp",EDGE,"E97.left"),sQuery(id+"F17.wireOp",EDGE,"E101")])]});
            var Q15;
            Q15=makeQuery(id+"F18.opExtrude","SWEPT_EDGE",EDGE,{"disambiguationData":[OSD([sQuery(id+"F17.wireOp",EDGE,"E86.bottom"),sQuery(id+"F17.wireOp",EDGE,"E89")])]});
            fillet(context, id + "F27", {"entities" : qUnion([Q0, Q1, Q2, Q3, Q4, Q5, Q6, Q7, Q8, Q9, Q10, Q11, Q12, Q13, Q14, Q15]), "radius" : 5.08 * mm, "tangentPropagation" : true, "allowEdgeOverflow" : false});
        }
        {
            var Q0;
            Q0=makeQuery(id+"F18.opExtrude","SWEPT_EDGE",EDGE,{"disambiguationData":[OSD([sQuery(id+"F17.wireOp",EDGE,"E98.bottom"),sQuery(id+"F17.wireOp",EDGE,"E116")])]});
            var Q1;
            Q1=makeQuery(id+"F18.opExtrude","SWEPT_EDGE",EDGE,{"disambiguationData":[OSD([sQuery(id+"F17.wireOp",EDGE,"E98.bottom"),sQuery(id+"F17.wireOp",EDGE,"E115")])]});
            var Q2;
            Q2=makeQuery(id+"F18.opExtrude","SWEPT_EDGE",EDGE,{"disambiguationData":[OSD([sQuery(id+"F17.wireOp",EDGE,"E98.left"),sQuery(id+"F17.wireOp",EDGE,"E112")])]});
            var Q3;
            Q3=makeQuery(id+"F18.opExtrude","SWEPT_EDGE",EDGE,{"disambiguationData":[OSD([sQuery(id+"F17.wireOp",EDGE,"E98.right"),sQuery(id+"F17.wireOp",EDGE,"E118")])]});
            var Q4;
            Q4=makeQuery(id+"F18.opExtrude","SWEPT_EDGE",EDGE,{"disambiguationData":[OSD([sQuery(id+"F17.wireOp",EDGE,"E98.left"),sQuery(id+"F17.wireOp",EDGE,"E101")])]});
            var Q5;
            Q5=makeQuery(id+"F18.opExtrude","SWEPT_EDGE",EDGE,{"disambiguationData":[OSD([sQuery(id+"F17.wireOp",EDGE,"E98.right"),sQuery(id+"F17.wireOp",EDGE,"E117")])]});
            var Q6;
            Q6=makeQuery(id+"F18.opExtrude","SWEPT_EDGE",EDGE,{"disambiguationData":[OSD([sQuery(id+"F17.wireOp",EDGE,"E98.top"),sQuery(id+"F17.wireOp",EDGE,"E114")])]});
            var Q7;
            Q7=makeQuery(id+"F18.opExtrude","SWEPT_EDGE",EDGE,{"disambiguationData":[OSD([sQuery(id+"F17.wireOp",EDGE,"E98.top"),sQuery(id+"F17.wireOp",EDGE,"E113")])]});
            fillet(context, id + "F28", {"entities" : qUnion([Q0, Q1, Q2, Q3, Q4, Q5, Q6, Q7]), "radius" : 1.27 * mm, "tangentPropagation" : true, "allowEdgeOverflow" : false});
        }
        {
            var Q0;
            {var subQ0=sQuery(id+"F17.wireOp",EDGE,"E104");var subQ1=sQuery(id+"F17.wireOp",EDGE,"E103");var subQ2=sQuery(id+"F17.wireOp",EDGE,"E87.top");Q0=makeQuery(id+"F20.opChamfer","BLEND_EDGE",EDGE,{"disambiguationData":[OD(1.0)],"blendedFrom":[makeQuery(id+"F18.opExtrude","CAP_EDGE",EDGE,{"disambiguationData":[OSD([subQ2,subQ1,subQ0])],"isStart":false}),makeQuery(id+"F18.opExtrude","CAP_FACE",FACE,{"disambiguationData":[OSD([sQuery(id+"F17.wireOp",EDGE,"E86.top"),subQ2,sQuery(id+"F17.wireOp",EDGE,"E91"),sQuery(id+"F17.wireOp",EDGE,"E95"),sQuery(id+"F17.wireOp",EDGE,"E97.bottom"),sQuery(id+"F17.wireOp",EDGE,"E98.bottom"),subQ1,subQ0,sQuery(id+"F17.wireOp",EDGE,"E115"),sQuery(id+"F17.wireOp",EDGE,"E116")])],"isStart":false})],"blendedInto":[makeQuery(id+"F18.opExtrude","CAP_FACE",FACE,{"disambiguationData":[OSD([sQuery(id+"F17.wireOp",EDGE,"E86.top"),subQ2,sQuery(id+"F17.wireOp",EDGE,"E91"),sQuery(id+"F17.wireOp",EDGE,"E95"),sQuery(id+"F17.wireOp",EDGE,"E97.bottom"),sQuery(id+"F17.wireOp",EDGE,"E98.bottom"),subQ1,subQ0,sQuery(id+"F17.wireOp",EDGE,"E115"),sQuery(id+"F17.wireOp",EDGE,"E116")])],"isStart":false})]});}
            var Q1;
            {var subQ0=sQuery(id+"F17.wireOp",EDGE,"E106");var subQ1=sQuery(id+"F17.wireOp",EDGE,"E105");var subQ2=sQuery(id+"F17.wireOp",EDGE,"E88.right");Q1=makeQuery(id+"F22.opChamfer","BLEND_EDGE",EDGE,{"disambiguationData":[OD(0.0)],"blendedFrom":[makeQuery(id+"F18.opExtrude","CAP_EDGE",EDGE,{"disambiguationData":[OSD([subQ2,subQ1,subQ0])],"isStart":false}),makeQuery(id+"F18.opExtrude","CAP_FACE",FACE,{"disambiguationData":[OSD([sQuery(id+"F17.wireOp",EDGE,"E86.right"),subQ2,sQuery(id+"F17.wireOp",EDGE,"E93"),sQuery(id+"F17.wireOp",EDGE,"E96"),sQuery(id+"F17.wireOp",EDGE,"E97.right"),sQuery(id+"F17.wireOp",EDGE,"E98.right"),subQ1,subQ0,sQuery(id+"F17.wireOp",EDGE,"E117"),sQuery(id+"F17.wireOp",EDGE,"E118")])],"isStart":false})],"blendedInto":[makeQuery(id+"F18.opExtrude","CAP_FACE",FACE,{"disambiguationData":[OSD([sQuery(id+"F17.wireOp",EDGE,"E86.right"),subQ2,sQuery(id+"F17.wireOp",EDGE,"E93"),sQuery(id+"F17.wireOp",EDGE,"E96"),sQuery(id+"F17.wireOp",EDGE,"E97.right"),sQuery(id+"F17.wireOp",EDGE,"E98.right"),subQ1,subQ0,sQuery(id+"F17.wireOp",EDGE,"E117"),sQuery(id+"F17.wireOp",EDGE,"E118")])],"isStart":false})]});}
            var Q2;
            {var subQ0=sQuery(id+"F17.wireOp",EDGE,"E108");var subQ1=sQuery(id+"F17.wireOp",EDGE,"E107");var subQ2=sQuery(id+"F17.wireOp",EDGE,"E87.bottom");Q2=makeQuery(id+"F21.opChamfer","BLEND_EDGE",EDGE,{"disambiguationData":[OD(0.0)],"blendedFrom":[makeQuery(id+"F18.opExtrude","CAP_EDGE",EDGE,{"disambiguationData":[OSD([subQ2,subQ1,subQ0])],"isStart":false}),makeQuery(id+"F18.opExtrude","CAP_FACE",FACE,{"disambiguationData":[OSD([sQuery(id+"F17.wireOp",EDGE,"E86.bottom"),subQ2,sQuery(id+"F17.wireOp",EDGE,"E89"),sQuery(id+"F17.wireOp",EDGE,"E94"),sQuery(id+"F17.wireOp",EDGE,"E97.top"),sQuery(id+"F17.wireOp",EDGE,"E98.top"),subQ1,subQ0,sQuery(id+"F17.wireOp",EDGE,"E113"),sQuery(id+"F17.wireOp",EDGE,"E114")])],"isStart":false})],"blendedInto":[makeQuery(id+"F18.opExtrude","CAP_FACE",FACE,{"disambiguationData":[OSD([sQuery(id+"F17.wireOp",EDGE,"E86.bottom"),subQ2,sQuery(id+"F17.wireOp",EDGE,"E89"),sQuery(id+"F17.wireOp",EDGE,"E94"),sQuery(id+"F17.wireOp",EDGE,"E97.top"),sQuery(id+"F17.wireOp",EDGE,"E98.top"),subQ1,subQ0,sQuery(id+"F17.wireOp",EDGE,"E113"),sQuery(id+"F17.wireOp",EDGE,"E114")])],"isStart":false})]});}
            var Q3;
            {var subQ0=sQuery(id+"F17.wireOp",EDGE,"E102");var subQ1=sQuery(id+"F17.wireOp",EDGE,"E100");var subQ2=sQuery(id+"F17.wireOp",EDGE,"E88.left");Q3=makeQuery(id+"F19.opChamfer","BLEND_EDGE",EDGE,{"disambiguationData":[OD(0.0)],"blendedFrom":[makeQuery(id+"F18.opExtrude","CAP_EDGE",EDGE,{"disambiguationData":[OSD([subQ2,subQ1,subQ0])],"isStart":false}),makeQuery(id+"F18.opExtrude","CAP_FACE",FACE,{"disambiguationData":[OSD([sQuery(id+"F17.wireOp",EDGE,"E86.left"),subQ2,sQuery(id+"F17.wireOp",EDGE,"E90"),sQuery(id+"F17.wireOp",EDGE,"E92"),sQuery(id+"F17.wireOp",EDGE,"E97.left"),sQuery(id+"F17.wireOp",EDGE,"E98.left"),subQ1,sQuery(id+"F17.wireOp",EDGE,"E101"),subQ0,sQuery(id+"F17.wireOp",EDGE,"E112")])],"isStart":false})],"blendedInto":[makeQuery(id+"F18.opExtrude","CAP_FACE",FACE,{"disambiguationData":[OSD([sQuery(id+"F17.wireOp",EDGE,"E86.left"),subQ2,sQuery(id+"F17.wireOp",EDGE,"E90"),sQuery(id+"F17.wireOp",EDGE,"E92"),sQuery(id+"F17.wireOp",EDGE,"E97.left"),sQuery(id+"F17.wireOp",EDGE,"E98.left"),subQ1,sQuery(id+"F17.wireOp",EDGE,"E101"),subQ0,sQuery(id+"F17.wireOp",EDGE,"E112")])],"isStart":false})]});}
            fillet(context, id + "F29", {"entities" : qUnion([Q0, Q1, Q2, Q3]), "radius" : 5.08 * mm, "tangentPropagation" : true, "allowEdgeOverflow" : false});
        }
        {
            var Q0;
            Q0=makeQuery(id+"F18.opExtrude","CAP_EDGE",EDGE,{"disambiguationData":[OSD([sQuery(id+"F17.wireOp",EDGE,"E86.top")])],"isStart":false});
            var Q1;
            Q1=makeQuery(id+"F18.opExtrude","CAP_EDGE",EDGE,{"disambiguationData":[OSD([sQuery(id+"F17.wireOp",EDGE,"E86.left")])],"isStart":false});
            var Q2;
            Q2=makeQuery(id+"F18.opExtrude","CAP_EDGE",EDGE,{"disambiguationData":[OSD([sQuery(id+"F17.wireOp",EDGE,"E86.bottom")])],"isStart":false});
            var Q3;
            Q3=makeQuery(id+"F18.opExtrude","CAP_EDGE",EDGE,{"disambiguationData":[OSD([sQuery(id+"F17.wireOp",EDGE,"E86.right")])],"isStart":false});
            var Q4;
            Q4=makeQuery(id+"F22.opChamfer","BLEND_EDGE",EDGE,{"blendedFrom":[makeQuery(id+"F18.opExtrude","CAP_EDGE",EDGE,{"disambiguationData":[OSD([sQuery(id+"F17.wireOp",EDGE,"E88.right"),sQuery(id+"F17.wireOp",EDGE,"E105"),sQuery(id+"F17.wireOp",EDGE,"E106")])],"isStart":false}),makeQuery(id+"F18.opExtrude","SWEPT_FACE",FACE,{"disambiguationData":[OSD([sQuery(id+"F17.wireOp",EDGE,"E98.right")])]})],"blendedInto":[makeQuery(id+"F18.opExtrude","SWEPT_FACE",FACE,{"disambiguationData":[OSD([sQuery(id+"F17.wireOp",EDGE,"E98.right")])]})]});
            var Q5;
            Q5=makeQuery(id+"F20.opChamfer","BLEND_EDGE",EDGE,{"blendedFrom":[makeQuery(id+"F18.opExtrude","CAP_EDGE",EDGE,{"disambiguationData":[OSD([sQuery(id+"F17.wireOp",EDGE,"E87.top"),sQuery(id+"F17.wireOp",EDGE,"E103"),sQuery(id+"F17.wireOp",EDGE,"E104")])],"isStart":false}),makeQuery(id+"F18.opExtrude","SWEPT_FACE",FACE,{"disambiguationData":[OSD([sQuery(id+"F17.wireOp",EDGE,"E98.bottom")])]})],"blendedInto":[makeQuery(id+"F18.opExtrude","SWEPT_FACE",FACE,{"disambiguationData":[OSD([sQuery(id+"F17.wireOp",EDGE,"E98.bottom")])]})]});
            var Q6;
            Q6=makeQuery(id+"F19.opChamfer","BLEND_EDGE",EDGE,{"blendedFrom":[makeQuery(id+"F18.opExtrude","CAP_EDGE",EDGE,{"disambiguationData":[OSD([sQuery(id+"F17.wireOp",EDGE,"E88.left"),sQuery(id+"F17.wireOp",EDGE,"E100"),sQuery(id+"F17.wireOp",EDGE,"E102")])],"isStart":false}),makeQuery(id+"F18.opExtrude","SWEPT_FACE",FACE,{"disambiguationData":[OSD([sQuery(id+"F17.wireOp",EDGE,"E98.left")])]})],"blendedInto":[makeQuery(id+"F18.opExtrude","SWEPT_FACE",FACE,{"disambiguationData":[OSD([sQuery(id+"F17.wireOp",EDGE,"E98.left")])]})]});
            var Q7;
            Q7=makeQuery(id+"F21.opChamfer","BLEND_EDGE",EDGE,{"blendedFrom":[makeQuery(id+"F18.opExtrude","CAP_EDGE",EDGE,{"disambiguationData":[OSD([sQuery(id+"F17.wireOp",EDGE,"E87.bottom"),sQuery(id+"F17.wireOp",EDGE,"E107"),sQuery(id+"F17.wireOp",EDGE,"E108")])],"isStart":false}),makeQuery(id+"F18.opExtrude","SWEPT_FACE",FACE,{"disambiguationData":[OSD([sQuery(id+"F17.wireOp",EDGE,"E98.top")])]})],"blendedInto":[makeQuery(id+"F18.opExtrude","SWEPT_FACE",FACE,{"disambiguationData":[OSD([sQuery(id+"F17.wireOp",EDGE,"E98.top")])]})]});
            fillet(context, id + "F30", {"entities" : qUnion([Q0, Q1, Q2, Q3, Q4, Q5, Q6, Q7]), "radius" : 1.27 * mm, "tangentPropagation" : true, "allowEdgeOverflow" : false});
        }
        {
            var Q0;
            {var subQ0=sQuery(id+"F15.wireOp",EDGE,"E85.top");var subQ1=sQuery(id+"F15.wireOp",EDGE,"E85.bottom");var subQ2=sQuery(id+"F15.wireOp",EDGE,"E85.right");var subQ3=sQuery(id+"F15.wireOp",EDGE,"E85.left");Q0=makeQuery(id+"F18.boolean.opBoolean","SPLIT",FACE,{"disambiguationData":[TD([makeQuery(id+"F16.opExtrude","SWEPT_FACE",FACE,{"disambiguationData":[OSD([subQ1])]})])],"derivedFrom":makeQuery(id+"F16.opExtrude","CAP_FACE",FACE,{"disambiguationData":[OSD([subQ1,subQ0,subQ3,subQ2])],"isStart":false})});}
            var sketch = newSketch(context, id + "F31", { "sketchPlane" : qUnion([Q0])});
            skLineSegment(sketch, "E121.bottom", {"start": v(-9.52, 9.53) * mm, "end": v(9.53, 9.53) * mm});
            skLineSegment(sketch, "E121.top", {"start": v(-9.53, -9.53) * mm, "end": v(9.52, -9.53) * mm});
            skLineSegment(sketch, "E121.left", {"start": v(-9.52, 9.53) * mm, "end": v(-9.53, -9.53) * mm});
            skLineSegment(sketch, "E121.right", {"start": v(9.53, 9.53) * mm, "end": v(9.52, -9.53) * mm});
            skPoint(sketch, "E121.middle", {"position": v(0, 0) * mm});
            skLineSegment(sketch, "E122.bottom", {"start": v(-5.71, 5.72) * mm, "end": v(5.72, 5.72) * mm});
            skLineSegment(sketch, "E122.top", {"start": v(-5.72, -5.72) * mm, "end": v(5.71, -5.72) * mm});
            skLineSegment(sketch, "E122.left", {"start": v(-5.71, 5.72) * mm, "end": v(-5.72, -5.72) * mm});
            skLineSegment(sketch, "E122.right", {"start": v(5.72, 5.72) * mm, "end": v(5.71, -5.72) * mm});
            skSolve(sketch);
        }
        {
            var Q0;
            Q0 = qSketchRegion(id + "F31", true);
            extrude(context, id + "F32", {"entities" : qUnion([Q0]), "depth" : 25.4 * mm, "offsetDistance" : 25.4 * mm});
        }
        {
            var Q0;
            Q0=makeQuery(id+"F32.opExtrude","SWEPT_EDGE",EDGE,{"disambiguationData":[OSD([sQuery(id+"F31.wireOp",EDGE,"E121.top"),sQuery(id+"F31.wireOp",EDGE,"E121.right")])]});
            var Q1;
            Q1=makeQuery(id+"F32.opExtrude","SWEPT_EDGE",EDGE,{"disambiguationData":[OSD([sQuery(id+"F31.wireOp",EDGE,"E121.top"),sQuery(id+"F31.wireOp",EDGE,"E121.left")])]});
            var Q2;
            Q2=makeQuery(id+"F32.opExtrude","SWEPT_EDGE",EDGE,{"disambiguationData":[OSD([sQuery(id+"F31.wireOp",EDGE,"E121.bottom"),sQuery(id+"F31.wireOp",EDGE,"E121.left")])]});
            var Q3;
            Q3=makeQuery(id+"F32.opExtrude","SWEPT_EDGE",EDGE,{"disambiguationData":[OSD([sQuery(id+"F31.wireOp",EDGE,"E121.bottom"),sQuery(id+"F31.wireOp",EDGE,"E121.right")])]});
            fillet(context, id + "F33", {"entities" : qUnion([Q0, Q1, Q2, Q3]), "radius" : 5.08 * mm, "tangentPropagation" : true, "allowEdgeOverflow" : false});
        }
        {
            var Q0;
            Q0=makeQuery(id+"F32.opExtrude","SWEPT_EDGE",EDGE,{"disambiguationData":[OSD([sQuery(id+"F31.wireOp",EDGE,"E122.top"),sQuery(id+"F31.wireOp",EDGE,"E122.left")])]});
            var Q1;
            Q1=makeQuery(id+"F32.opExtrude","SWEPT_EDGE",EDGE,{"disambiguationData":[OSD([sQuery(id+"F31.wireOp",EDGE,"E122.top"),sQuery(id+"F31.wireOp",EDGE,"E122.right")])]});
            var Q2;
            Q2=makeQuery(id+"F32.opExtrude","SWEPT_EDGE",EDGE,{"disambiguationData":[OSD([sQuery(id+"F31.wireOp",EDGE,"E122.bottom"),sQuery(id+"F31.wireOp",EDGE,"E122.left")])]});
            var Q3;
            Q3=makeQuery(id+"F32.opExtrude","SWEPT_EDGE",EDGE,{"disambiguationData":[OSD([sQuery(id+"F31.wireOp",EDGE,"E122.bottom"),sQuery(id+"F31.wireOp",EDGE,"E122.right")])]});
            fillet(context, id + "F34", {"entities" : qUnion([Q0, Q1, Q2, Q3]), "radius" : 2.54 * mm, "tangentPropagation" : true, "allowEdgeOverflow" : false});
        }
        {
            var Q0;
            Q0=makeQuery(id+"F32.opExtrude","CAP_FACE",FACE,{"disambiguationData":[OSD([sQuery(id+"F31.wireOp",EDGE,"E121.bottom"),sQuery(id+"F31.wireOp",EDGE,"E121.top"),sQuery(id+"F31.wireOp",EDGE,"E121.left"),sQuery(id+"F31.wireOp",EDGE,"E121.right"),sQuery(id+"F31.wireOp",EDGE,"E122.bottom"),sQuery(id+"F31.wireOp",EDGE,"E122.top"),sQuery(id+"F31.wireOp",EDGE,"E122.left"),sQuery(id+"F31.wireOp",EDGE,"E122.right")])],"isStart":false});
            fillet(context, id + "F35", {"entities" : qUnion([Q0]), "radius" : 1.27 * mm, "tangentPropagation" : true, "allowEdgeOverflow" : false});
        }
        {
            var Q0;
            Q0=makeQuery(id+"F18.opExtrude","CAP_FACE",FACE,{"disambiguationData":[OSD([sQuery(id+"F17.wireOp",EDGE,"E86.top"),sQuery(id+"F17.wireOp",EDGE,"E87.top"),sQuery(id+"F17.wireOp",EDGE,"E91"),sQuery(id+"F17.wireOp",EDGE,"E95"),sQuery(id+"F17.wireOp",EDGE,"E97.bottom"),sQuery(id+"F17.wireOp",EDGE,"E98.bottom"),sQuery(id+"F17.wireOp",EDGE,"E103"),sQuery(id+"F17.wireOp",EDGE,"E104"),sQuery(id+"F17.wireOp",EDGE,"E115"),sQuery(id+"F17.wireOp",EDGE,"E116")])],"isStart":true});
            var sketch = newSketch(context, id + "F36", { "sketchPlane" : qUnion([Q0])});
            skLineSegment(sketch, "E123.bottom", {"start": v(-29.2, 29.21) * mm, "end": v(29.21, 29.21) * mm});
            skLineSegment(sketch, "E123.top", {"start": v(-29.21, -29.21) * mm, "end": v(29.2, -29.21) * mm});
            skLineSegment(sketch, "E123.left", {"start": v(-29.2, 29.21) * mm, "end": v(-29.21, -29.21) * mm});
            skLineSegment(sketch, "E123.right", {"start": v(29.21, 29.21) * mm, "end": v(29.2, -29.21) * mm});
            skPoint(sketch, "E123.middle", {"position": v(0, 0) * mm});
            skSolve(sketch);
        }
        {
            var Q0;
            {var subQ1=sQuery(id+"F17.wireOp",EDGE,"E104");var subQ2=sQuery(id+"F17.wireOp",EDGE,"E103");var subQ5=sQuery(id+"F17.wireOp",EDGE,"E87.top");var subQ12=makeQuery(id+"F18.opExtrude","CAP_EDGE",EDGE,{"disambiguationData":[OSD([subQ5,subQ2,subQ1])],"isStart":true});Q0=makeQuery(id+"F36.imprint","IMPRINT",FACE,{"disambiguationData":[TD([[makeQuery(id+"F36.imprint","IMPRINT",EDGE,{"derivedFrom":subQ12}),-1.0]])]});}
            extrude(context, id + "F37", {"entities" : qUnion([Q0]), "depth" : 7.62 * mm, "offsetDistance" : 25.4 * mm});
        }
        {
            var Q0;
            Q0=makeQuery(id+"F18.opExtrude","CAP_FACE",FACE,{"disambiguationData":[OSD([sQuery(id+"F17.wireOp",EDGE,"E86.right"),sQuery(id+"F17.wireOp",EDGE,"E88.right"),sQuery(id+"F17.wireOp",EDGE,"E93"),sQuery(id+"F17.wireOp",EDGE,"E96"),sQuery(id+"F17.wireOp",EDGE,"E97.right"),sQuery(id+"F17.wireOp",EDGE,"E98.right"),sQuery(id+"F17.wireOp",EDGE,"E105"),sQuery(id+"F17.wireOp",EDGE,"E106"),sQuery(id+"F17.wireOp",EDGE,"E117"),sQuery(id+"F17.wireOp",EDGE,"E118")])],"isStart":true});
            var sketch = newSketch(context, id + "F38", { "sketchPlane" : qUnion([Q0])});
            skLineSegment(sketch, "E124.bottom", {"start": v(29.2, -29.2) * mm, "end": v(-29.21, -29.21) * mm});
            skLineSegment(sketch, "E124.top", {"start": v(29.21, 29.21) * mm, "end": v(-29.2, 29.2) * mm});
            skLineSegment(sketch, "E124.left", {"start": v(29.2, -29.2) * mm, "end": v(29.21, 29.21) * mm});
            skLineSegment(sketch, "E124.right", {"start": v(-29.21, -29.21) * mm, "end": v(-29.2, 29.2) * mm});
            skPoint(sketch, "E124.middle", {"position": v(0, 0) * mm});
            skSolve(sketch);
        }
        {
            var Q0;
            {var subQ1=sQuery(id+"F17.wireOp",EDGE,"E106");var subQ2=sQuery(id+"F17.wireOp",EDGE,"E105");var subQ5=sQuery(id+"F17.wireOp",EDGE,"E88.right");var subQ12=makeQuery(id+"F18.opExtrude","CAP_EDGE",EDGE,{"disambiguationData":[OSD([subQ5,subQ2,subQ1])],"isStart":true});Q0=makeQuery(id+"F38.imprint","IMPRINT",FACE,{"disambiguationData":[TD([[makeQuery(id+"F38.imprint","IMPRINT",EDGE,{"derivedFrom":subQ12}),1.0]])]});}
            extrude(context, id + "F39", {"entities" : qUnion([Q0]), "depth" : 7.62 * mm, "offsetDistance" : 25.4 * mm});
        }
        {
            var Q0;
            Q0=makeQuery(id+"F18.opExtrude","CAP_FACE",FACE,{"disambiguationData":[OSD([sQuery(id+"F17.wireOp",EDGE,"E86.bottom"),sQuery(id+"F17.wireOp",EDGE,"E87.bottom"),sQuery(id+"F17.wireOp",EDGE,"E89"),sQuery(id+"F17.wireOp",EDGE,"E94"),sQuery(id+"F17.wireOp",EDGE,"E97.top"),sQuery(id+"F17.wireOp",EDGE,"E98.top"),sQuery(id+"F17.wireOp",EDGE,"E107"),sQuery(id+"F17.wireOp",EDGE,"E108"),sQuery(id+"F17.wireOp",EDGE,"E113"),sQuery(id+"F17.wireOp",EDGE,"E114")])],"isStart":true});
            var sketch = newSketch(context, id + "F40", { "sketchPlane" : qUnion([Q0])});
            skLineSegment(sketch, "E125.bottom", {"start": v(29.21, -29.2) * mm, "end": v(-29.21, -29.21) * mm});
            skLineSegment(sketch, "E125.top", {"start": v(29.21, 29.21) * mm, "end": v(-29.21, 29.21) * mm});
            skLineSegment(sketch, "E125.left", {"start": v(29.21, -29.2) * mm, "end": v(29.21, 29.21) * mm});
            skLineSegment(sketch, "E125.right", {"start": v(-29.21, -29.21) * mm, "end": v(-29.2, 29.21) * mm});
            skPoint(sketch, "E125.middle", {"position": v(0, 0) * mm});
            skSolve(sketch);
        }
        {
            var Q0;
            {var subQ1=sQuery(id+"F17.wireOp",EDGE,"E108");var subQ2=sQuery(id+"F17.wireOp",EDGE,"E107");var subQ5=sQuery(id+"F17.wireOp",EDGE,"E87.bottom");var subQ12=makeQuery(id+"F18.opExtrude","CAP_EDGE",EDGE,{"disambiguationData":[OSD([subQ5,subQ2,subQ1])],"isStart":true});Q0=makeQuery(id+"F40.imprint","IMPRINT",FACE,{"disambiguationData":[TD([[makeQuery(id+"F40.imprint","IMPRINT",EDGE,{"derivedFrom":subQ12}),1.0]])]});}
            extrude(context, id + "F41", {"entities" : qUnion([Q0]), "depth" : 7.62 * mm, "offsetDistance" : 25.4 * mm});
        }
        {
            var Q0;
            Q0=makeQuery(id+"F18.opExtrude","CAP_FACE",FACE,{"disambiguationData":[OSD([sQuery(id+"F17.wireOp",EDGE,"E86.left"),sQuery(id+"F17.wireOp",EDGE,"E88.left"),sQuery(id+"F17.wireOp",EDGE,"E90"),sQuery(id+"F17.wireOp",EDGE,"E92"),sQuery(id+"F17.wireOp",EDGE,"E97.left"),sQuery(id+"F17.wireOp",EDGE,"E98.left"),sQuery(id+"F17.wireOp",EDGE,"E100"),sQuery(id+"F17.wireOp",EDGE,"E101"),sQuery(id+"F17.wireOp",EDGE,"E102"),sQuery(id+"F17.wireOp",EDGE,"E112")])],"isStart":true});
            var sketch = newSketch(context, id + "F42", { "sketchPlane" : qUnion([Q0])});
            skLineSegment(sketch, "E126.bottom", {"start": v(-29.21, -29.21) * mm, "end": v(29.2, -29.21) * mm});
            skLineSegment(sketch, "E126.top", {"start": v(-29.21, 29.21) * mm, "end": v(29.2, 29.21) * mm});
            skLineSegment(sketch, "E126.left", {"start": v(-29.21, -29.21) * mm, "end": v(-29.21, 29.21) * mm});
            skLineSegment(sketch, "E126.right", {"start": v(29.2, -29.21) * mm, "end": v(29.2, 29.21) * mm});
            skPoint(sketch, "E126.middle", {"position": v(0, 0) * mm});
            skSolve(sketch);
        }
        {
            var Q0;
            {var subQ1=sQuery(id+"F17.wireOp",EDGE,"E102");var subQ2=sQuery(id+"F17.wireOp",EDGE,"E100");var subQ5=sQuery(id+"F17.wireOp",EDGE,"E88.left");var subQ12=makeQuery(id+"F18.opExtrude","CAP_EDGE",EDGE,{"disambiguationData":[OSD([subQ5,subQ2,subQ1])],"isStart":true});Q0=makeQuery(id+"F42.imprint","IMPRINT",FACE,{"disambiguationData":[TD([[makeQuery(id+"F42.imprint","IMPRINT",EDGE,{"derivedFrom":subQ12}),-1.0]])]});}
            extrude(context, id + "F43", {"entities" : qUnion([Q0]), "depth" : 7.62 * mm, "offsetDistance" : 25.4 * mm});
        }
        {
            var Q0;
            Q0=makeQuery(id+"F41.opExtrude","CAP_EDGE",EDGE,{"disambiguationData":[OSD([sQuery(id+"F17.wireOp",EDGE,"E87.bottom"),sQuery(id+"F17.wireOp",EDGE,"E107"),sQuery(id+"F17.wireOp",EDGE,"E108")])],"isStart":false});
            var Q1;
            Q1=makeQuery(id+"F43.opExtrude","CAP_EDGE",EDGE,{"disambiguationData":[OSD([sQuery(id+"F17.wireOp",EDGE,"E88.left"),sQuery(id+"F17.wireOp",EDGE,"E100"),sQuery(id+"F17.wireOp",EDGE,"E102")])],"isStart":false});
            var Q2;
            Q2=makeQuery(id+"F39.opExtrude","CAP_EDGE",EDGE,{"disambiguationData":[OSD([sQuery(id+"F17.wireOp",EDGE,"E88.right"),sQuery(id+"F17.wireOp",EDGE,"E105"),sQuery(id+"F17.wireOp",EDGE,"E106")])],"isStart":false});
            var Q3;
            Q3=makeQuery(id+"F37.opExtrude","CAP_EDGE",EDGE,{"disambiguationData":[OSD([sQuery(id+"F17.wireOp",EDGE,"E87.top"),sQuery(id+"F17.wireOp",EDGE,"E103"),sQuery(id+"F17.wireOp",EDGE,"E104")])],"isStart":false});
            fillet(context, id + "F44", {"entities" : qUnion([Q0, Q1, Q2, Q3]), "radius" : 2.54 * mm, "tangentPropagation" : true, "allowEdgeOverflow" : false});
        }
        {
            var Q0;
            Q0=qCreatedBy(makeId("Right.planeOp"),FACE);
            var Q1;
            Q1=qCreatedBy(makeId("Front.planeOp"),FACE);
            cPlane(context, id + "F45", {"entities" : qUnion([Q0, Q1]), "cplaneType" : CPlaneType.MID_PLANE, "offset" : 25.4 * mm, "width" : 152.4 * mm, "height" : 152.4 * mm});
        }
        {
            var Q0;
            Q0=qCreatedBy(makeId("Front.planeOp"),FACE);
            var Q1;
            Q1=qCreatedBy(makeId("Right.planeOp"),FACE);
            cPlane(context, id + "F46", {"entities" : qUnion([Q0, Q1]), "cplaneType" : CPlaneType.MID_PLANE, "offset" : 25.4 * mm, "flipAlignment" : true, "width" : 152.4 * mm, "height" : 152.4 * mm});
        }
        {
            var Q0;
            Q0=qCreatedBy(id+"F45.planeOp",FACE);
            var sketch = newSketch(context, id + "F47", { "sketchPlane" : qUnion([Q0])});
            skLineSegment(sketch, "E127.bottom", {"start": v(26.5, 39.1) * mm, "end": v(-26.5, 39.1) * mm});
            skLineSegment(sketch, "E127.top", {"start": v(26.5, -39.1) * mm, "end": v(-26.5, -39.1) * mm});
            skLineSegment(sketch, "E127.left", {"start": v(26.5, 39.1) * mm, "end": v(26.5, -39.1) * mm});
            skLineSegment(sketch, "E127.right", {"start": v(-26.5, 39.1) * mm, "end": v(-26.5, -39.1) * mm});
            skPoint(sketch, "E127.middle", {"position": v(0, 0) * mm});
            skLineSegment(sketch, "E128", {"start": v(26.5, 0) * mm, "end": v(31.34, 0) * mm});
            skLineSegment(sketch, "E129", {"start": v(-26.5, 0) * mm, "end": v(-31.33, 0) * mm});
            skLineSegment(sketch, "E130", {"start": v(-26.5, 39.1) * mm, "end": v(-31.33, 0) * mm});
            skLineSegment(sketch, "E131", {"start": v(-31.33, 0) * mm, "end": v(-37.23, 0) * mm});
            skLineSegment(sketch, "E132", {"start": v(31.34, 0) * mm, "end": v(37.24, 0) * mm});
            skLineSegment(sketch, "E133", {"start": v(-37.23, 0) * mm, "end": v(-37.23, -9.4) * mm});
            skLineSegment(sketch, "E134", {"start": v(37.24, 0) * mm, "end": v(37.24, -9.4) * mm});
            skLineSegment(sketch, "E135.bottom", {"start": v(-44.45, -17.78) * mm, "end": v(44.45, -17.78) * mm});
            skLineSegment(sketch, "E135.top", {"start": v(-44.45, 17.78) * mm, "end": v(44.45, 17.78) * mm});
            skLineSegment(sketch, "E135.left", {"start": v(-44.45, -17.78) * mm, "end": v(-44.45, 17.78) * mm});
            skLineSegment(sketch, "E135.right", {"start": v(44.45, -17.78) * mm, "end": v(44.45, 17.78) * mm});
            skLineSegment(sketch, "E136", {"start": v(-37.23, -9.4) * mm, "end": v(-44.45, -17.78) * mm});
            skLineSegment(sketch, "E137", {"start": v(0, 17.78) * mm, "end": v(-40.64, 17.78) * mm});
            skLineSegment(sketch, "E138", {"start": v(-44.45, -17.78) * mm, "end": v(-40.64, 17.78) * mm});
            skLineSegment(sketch, "E139", {"start": v(-40.64, 17.78) * mm, "end": v(-26.5, 39.1) * mm});
            skLineSegment(sketch, "E140", {"start": v(37.24, -9.4) * mm, "end": v(44.45, -17.78) * mm});
            skLineSegment(sketch, "E141", {"start": v(0, 17.78) * mm, "end": v(40.64, 17.78) * mm});
            skLineSegment(sketch, "E142", {"start": v(44.45, -17.78) * mm, "end": v(40.64, 17.78) * mm});
            skLineSegment(sketch, "E143", {"start": v(40.64, 17.78) * mm, "end": v(26.5, 39.1) * mm});
            skLineSegment(sketch, "E144.bottom", {"start": v(-44.45, 14.75) * mm, "end": v(44.45, 14.75) * mm});
            skLineSegment(sketch, "E144.top", {"start": v(-44.45, 12.21) * mm, "end": v(44.45, 12.21) * mm});
            skLineSegment(sketch, "E144.left", {"start": v(-44.45, 14.75) * mm, "end": v(-44.45, 12.21) * mm});
            skLineSegment(sketch, "E144.right", {"start": v(44.45, 14.75) * mm, "end": v(44.45, 12.21) * mm});
            skPoint(sketch, "E144.middle", {"position": v(0, 13.48) * mm});
            skLineSegment(sketch, "E145.bottom", {"start": v(-44.45, 9.35) * mm, "end": v(44.45, 9.35) * mm});
            skLineSegment(sketch, "E145.top", {"start": v(-44.45, 6.81) * mm, "end": v(44.45, 6.81) * mm});
            skLineSegment(sketch, "E145.left", {"start": v(-44.45, 9.35) * mm, "end": v(-44.45, 6.81) * mm});
            skLineSegment(sketch, "E145.right", {"start": v(44.45, 9.35) * mm, "end": v(44.45, 6.81) * mm});
            skPoint(sketch, "E145.middle", {"position": v(0, 8.08) * mm});
            skLineSegment(sketch, "E146.bottom", {"start": v(-44.45, 4.09) * mm, "end": v(44.45, 4.09) * mm});
            skLineSegment(sketch, "E146.top", {"start": v(-44.45, 1.55) * mm, "end": v(44.45, 1.55) * mm});
            skLineSegment(sketch, "E146.left", {"start": v(-44.45, 4.09) * mm, "end": v(-44.45, 1.55) * mm});
            skLineSegment(sketch, "E146.right", {"start": v(44.45, 4.09) * mm, "end": v(44.45, 1.55) * mm});
            skPoint(sketch, "E146.middle", {"position": v(0, 2.82) * mm});
            skLineSegment(sketch, "E147", {"start": v(-37.23, 17.78) * mm, "end": v(-44.45, -17.78) * mm});
            skLineSegment(sketch, "E148", {"start": v(37.24, 17.78) * mm, "end": v(44.45, -17.78) * mm});
            skLineSegment(sketch, "E149", {"start": v(26.5, 39.1) * mm, "end": v(31.34, 0) * mm});
            skSolve(sketch);
        }
        {
            var Q0;
            {var subQ0=sQuery(id+"F47.wireOp",EDGE,"E139");Q0=makeQuery(id+"F47.imprint","IMPRINT",FACE,{"disambiguationData":[TD([[makeQuery(id+"F47.imprint","IMPRINT",EDGE,{"derivedFrom":subQ0}),-1.0]])]});}
            var Q1;
            {var subQ0=sQuery(id+"F47.wireOp",EDGE,"E138");var subQ5=sQuery(id+"F47.wireOp",EDGE,"E144.bottom");var subQ6=makeQuery(id+"F47.imprint","INTERSECT",VERTEX,{"derivedFrom":[subQ0,subQ5]});Q1=makeQuery(id+"F47.imprint","IMPRINT",FACE,{"disambiguationData":[TD([[makeQuery(id+"F47.imprint","IMPRINT",EDGE,{"disambiguationData":[TD([[subQ6,-1.0]])],"derivedFrom":subQ5}),1.0]])]});}
            var Q2;
            {var subQ0=sQuery(id+"F47.wireOp",EDGE,"E144.bottom");var subQ1=sQuery(id+"F47.wireOp",EDGE,"E130");var subQ2=makeQuery(id+"F47.imprint","INTERSECT",VERTEX,{"derivedFrom":[subQ1,subQ0]});Q2=makeQuery(id+"F47.imprint","IMPRINT",FACE,{"disambiguationData":[TD([[makeQuery(id+"F47.imprint","IMPRINT",EDGE,{"disambiguationData":[TD([[subQ2,-1.0]])],"derivedFrom":subQ1}),-1.0]])]});}
            var Q3;
            {var subQ0=sQuery(id+"F47.wireOp",EDGE,"E145.bottom");var subQ1=sQuery(id+"F47.wireOp",EDGE,"E130");var subQ2=makeQuery(id+"F47.imprint","INTERSECT",VERTEX,{"derivedFrom":[subQ1,subQ0]});Q3=makeQuery(id+"F47.imprint","IMPRINT",FACE,{"disambiguationData":[TD([[makeQuery(id+"F47.imprint","IMPRINT",EDGE,{"disambiguationData":[TD([[subQ2,-1.0]])],"derivedFrom":subQ1}),-1.0]])]});}
            var Q4;
            {var subQ0=sQuery(id+"F47.wireOp",EDGE,"E146.bottom");var subQ1=sQuery(id+"F47.wireOp",EDGE,"E130");var subQ2=makeQuery(id+"F47.imprint","INTERSECT",VERTEX,{"derivedFrom":[subQ1,subQ0]});Q4=makeQuery(id+"F47.imprint","IMPRINT",FACE,{"disambiguationData":[TD([[makeQuery(id+"F47.imprint","IMPRINT",EDGE,{"disambiguationData":[TD([[subQ2,-1.0]])],"derivedFrom":subQ1}),-1.0]])]});}
            var Q5;
            {var subQ0=sQuery(id+"F47.wireOp",EDGE,"E145.bottom");var subQ1=sQuery(id+"F47.wireOp",EDGE,"E138");var subQ2=makeQuery(id+"F47.imprint","INTERSECT",VERTEX,{"derivedFrom":[subQ1,subQ0]});Q5=makeQuery(id+"F47.imprint","IMPRINT",FACE,{"disambiguationData":[TD([[makeQuery(id+"F47.imprint","IMPRINT",EDGE,{"disambiguationData":[TD([[subQ2,-1.0]])],"derivedFrom":subQ1}),-1.0]])]});}
            var Q6;
            {var subQ0=sQuery(id+"F47.wireOp",EDGE,"E146.bottom");var subQ1=sQuery(id+"F47.wireOp",EDGE,"E138");var subQ2=makeQuery(id+"F47.imprint","INTERSECT",VERTEX,{"derivedFrom":[subQ1,subQ0]});Q6=makeQuery(id+"F47.imprint","IMPRINT",FACE,{"disambiguationData":[TD([[makeQuery(id+"F47.imprint","IMPRINT",EDGE,{"disambiguationData":[TD([[subQ2,-1.0]])],"derivedFrom":subQ1}),-1.0]])]});}
            var Q7;
            {var subQ6=sQuery(id+"F47.wireOp",EDGE,"E131");Q7=makeQuery(id+"F47.imprint","IMPRINT",FACE,{"disambiguationData":[TD([[makeQuery(id+"F47.imprint","IMPRINT",EDGE,{"derivedFrom":subQ6}),-1.0]])]});}
            var Q8;
            {var subQ1=sQuery(id+"F47.wireOp",EDGE,"E138");var subQ3=sQuery(id+"F47.wireOp",EDGE,"E146.top");var subQ4=makeQuery(id+"F47.imprint","INTERSECT",VERTEX,{"derivedFrom":[subQ1,subQ3]});Q8=makeQuery(id+"F47.imprint","IMPRINT",FACE,{"disambiguationData":[TD([[makeQuery(id+"F47.imprint","IMPRINT",EDGE,{"disambiguationData":[TD([[subQ4,-1.0]])],"derivedFrom":subQ3}),-1.0]])]});}
            var Q9;
            {var subQ4=sQuery(id+"F47.wireOp",EDGE,"E143");Q9=makeQuery(id+"F47.imprint","IMPRINT",FACE,{"disambiguationData":[TD([[makeQuery(id+"F47.imprint","IMPRINT",EDGE,{"derivedFrom":subQ4}),1.0]])]});}
            var Q10;
            {var subQ0=sQuery(id+"F47.wireOp",EDGE,"E142");var subQ5=sQuery(id+"F47.wireOp",EDGE,"E144.bottom");var subQ6=makeQuery(id+"F47.imprint","INTERSECT",VERTEX,{"derivedFrom":[subQ0,subQ5]});Q10=makeQuery(id+"F47.imprint","IMPRINT",FACE,{"disambiguationData":[TD([[makeQuery(id+"F47.imprint","IMPRINT",EDGE,{"disambiguationData":[TD([[subQ6,1.0]])],"derivedFrom":subQ5}),1.0]])]});}
            var Q11;
            {var subQ0=sQuery(id+"F47.wireOp",EDGE,"E144.top");var subQ1=sQuery(id+"F47.wireOp",EDGE,"E142");var subQ2=makeQuery(id+"F47.imprint","INTERSECT",VERTEX,{"derivedFrom":[subQ1,subQ0]});Q11=makeQuery(id+"F47.imprint","IMPRINT",FACE,{"disambiguationData":[TD([[makeQuery(id+"F47.imprint","IMPRINT",EDGE,{"disambiguationData":[TD([[subQ2,-1.0]])],"derivedFrom":subQ1}),1.0]])]});}
            var Q12;
            {var subQ0=sQuery(id+"F47.wireOp",EDGE,"E149");var subQ1=sQuery(id+"F47.wireOp",EDGE,"E144.bottom");var subQ2=makeQuery(id+"F47.imprint","INTERSECT",VERTEX,{"derivedFrom":[subQ1,subQ0]});Q12=makeQuery(id+"F47.imprint","IMPRINT",FACE,{"disambiguationData":[TD([[makeQuery(id+"F47.imprint","IMPRINT",EDGE,{"disambiguationData":[TD([[subQ2,-1.0]])],"derivedFrom":subQ1}),-1.0]])]});}
            var Q13;
            {var subQ0=sQuery(id+"F47.wireOp",EDGE,"E149");var subQ1=sQuery(id+"F47.wireOp",EDGE,"E145.bottom");var subQ2=makeQuery(id+"F47.imprint","INTERSECT",VERTEX,{"derivedFrom":[subQ1,subQ0]});Q13=makeQuery(id+"F47.imprint","IMPRINT",FACE,{"disambiguationData":[TD([[makeQuery(id+"F47.imprint","IMPRINT",EDGE,{"disambiguationData":[TD([[subQ2,-1.0]])],"derivedFrom":subQ1}),-1.0]])]});}
            var Q14;
            {var subQ0=sQuery(id+"F47.wireOp",EDGE,"E145.top");var subQ1=sQuery(id+"F47.wireOp",EDGE,"E142");var subQ2=makeQuery(id+"F47.imprint","INTERSECT",VERTEX,{"derivedFrom":[subQ1,subQ0]});Q14=makeQuery(id+"F47.imprint","IMPRINT",FACE,{"disambiguationData":[TD([[makeQuery(id+"F47.imprint","IMPRINT",EDGE,{"disambiguationData":[TD([[subQ2,-1.0]])],"derivedFrom":subQ1}),1.0]])]});}
            var Q15;
            {var subQ0=sQuery(id+"F47.wireOp",EDGE,"E146.bottom");var subQ1=sQuery(id+"F47.wireOp",EDGE,"E142");var subQ2=makeQuery(id+"F47.imprint","INTERSECT",VERTEX,{"derivedFrom":[subQ1,subQ0]});Q15=makeQuery(id+"F47.imprint","IMPRINT",FACE,{"disambiguationData":[TD([[makeQuery(id+"F47.imprint","IMPRINT",EDGE,{"disambiguationData":[TD([[subQ2,-1.0]])],"derivedFrom":subQ1}),1.0]])]});}
            var Q16;
            {var subQ0=sQuery(id+"F47.wireOp",EDGE,"E149");var subQ1=sQuery(id+"F47.wireOp",EDGE,"E146.bottom");var subQ2=makeQuery(id+"F47.imprint","INTERSECT",VERTEX,{"derivedFrom":[subQ1,subQ0]});Q16=makeQuery(id+"F47.imprint","IMPRINT",FACE,{"disambiguationData":[TD([[makeQuery(id+"F47.imprint","IMPRINT",EDGE,{"disambiguationData":[TD([[subQ2,-1.0]])],"derivedFrom":subQ1}),-1.0]])]});}
            var Q17;
            {var subQ0=sQuery(id+"F47.wireOp",EDGE,"E145.bottom");var subQ1=sQuery(id+"F47.wireOp",EDGE,"E142");var subQ2=makeQuery(id+"F47.imprint","INTERSECT",VERTEX,{"derivedFrom":[subQ1,subQ0]});Q17=makeQuery(id+"F47.imprint","IMPRINT",FACE,{"disambiguationData":[TD([[makeQuery(id+"F47.imprint","IMPRINT",EDGE,{"disambiguationData":[TD([[subQ2,-1.0]])],"derivedFrom":subQ1}),1.0]])]});}
            var Q18;
            {var subQ0=sQuery(id+"F47.wireOp",EDGE,"E146.top");var subQ1=sQuery(id+"F47.wireOp",EDGE,"E142");var subQ2=makeQuery(id+"F47.imprint","INTERSECT",VERTEX,{"derivedFrom":[subQ1,subQ0]});Q18=makeQuery(id+"F47.imprint","IMPRINT",FACE,{"disambiguationData":[TD([[makeQuery(id+"F47.imprint","IMPRINT",EDGE,{"disambiguationData":[TD([[subQ2,-1.0]])],"derivedFrom":subQ1}),1.0]])]});}
            var Q19;
            {var subQ6=sQuery(id+"F47.wireOp",EDGE,"E132");Q19=makeQuery(id+"F47.imprint","IMPRINT",FACE,{"disambiguationData":[TD([[makeQuery(id+"F47.imprint","IMPRINT",EDGE,{"derivedFrom":subQ6}),1.0]])]});}
            var Q20;
            {var subQ1=sQuery(id+"F47.wireOp",EDGE,"E142");var subQ3=sQuery(id+"F47.wireOp",EDGE,"E146.top");var subQ4=makeQuery(id+"F47.imprint","INTERSECT",VERTEX,{"derivedFrom":[subQ1,subQ3]});Q20=makeQuery(id+"F47.imprint","IMPRINT",FACE,{"disambiguationData":[TD([[makeQuery(id+"F47.imprint","IMPRINT",EDGE,{"disambiguationData":[TD([[subQ4,1.0]])],"derivedFrom":subQ3}),-1.0]])]});}
            var Q21;
            {var subQ0=sQuery(id+"F47.wireOp",EDGE,"E144.top");var subQ1=sQuery(id+"F47.wireOp",EDGE,"E138");var subQ2=makeQuery(id+"F47.imprint","INTERSECT",VERTEX,{"derivedFrom":[subQ1,subQ0]});Q21=makeQuery(id+"F47.imprint","IMPRINT",FACE,{"disambiguationData":[TD([[makeQuery(id+"F47.imprint","IMPRINT",EDGE,{"disambiguationData":[TD([[subQ2,-1.0]])],"derivedFrom":subQ1}),-1.0]])]});}
            var Q22;
            {var subQ0=sQuery(id+"F47.wireOp",EDGE,"E145.top");var subQ1=sQuery(id+"F47.wireOp",EDGE,"E138");var subQ2=makeQuery(id+"F47.imprint","INTERSECT",VERTEX,{"derivedFrom":[subQ1,subQ0]});Q22=makeQuery(id+"F47.imprint","IMPRINT",FACE,{"disambiguationData":[TD([[makeQuery(id+"F47.imprint","IMPRINT",EDGE,{"disambiguationData":[TD([[subQ2,-1.0]])],"derivedFrom":subQ1}),-1.0]])]});}
            var Q23;
            {var subQ0=sQuery(id+"F47.wireOp",EDGE,"E146.top");var subQ1=sQuery(id+"F47.wireOp",EDGE,"E138");var subQ2=makeQuery(id+"F47.imprint","INTERSECT",VERTEX,{"derivedFrom":[subQ1,subQ0]});Q23=makeQuery(id+"F47.imprint","IMPRINT",FACE,{"disambiguationData":[TD([[makeQuery(id+"F47.imprint","IMPRINT",EDGE,{"disambiguationData":[TD([[subQ2,-1.0]])],"derivedFrom":subQ1}),-1.0]])]});}
            extrude(context, id + "F48", {"entities" : qUnion([Q0, Q1, Q2, Q3, Q4, Q5, Q6, Q7, Q8, Q9, Q10, Q11, Q12, Q13, Q14, Q15, Q16, Q17, Q18, Q19, Q20, Q21, Q22, Q23]), "depth" : 1.78 * mm, "offsetDistance" : 25.4 * mm, "hasSecondDirection" : true, "secondDirectionOppositeDirection" : true, "secondDirectionDepth" : 1.78 * mm});
        }
        {
            var Q0;
            Q0=qCreatedBy(id+"F46.planeOp",FACE);
            var sketch = newSketch(context, id + "F49", { "sketchPlane" : qUnion([Q0])});
            skLineSegment(sketch, "E150.bottom", {"start": v(26.5, 39.1) * mm, "end": v(-26.5, 39.1) * mm});
            skLineSegment(sketch, "E150.top", {"start": v(26.5, -39.09) * mm, "end": v(-26.5, -39.09) * mm});
            skLineSegment(sketch, "E150.left", {"start": v(26.5, 39.1) * mm, "end": v(26.5, -39.09) * mm});
            skLineSegment(sketch, "E150.right", {"start": v(-26.5, 39.1) * mm, "end": v(-26.5, -39.09) * mm});
            skPoint(sketch, "E150.middle", {"position": v(0, 0) * mm});
            skLineSegment(sketch, "E151", {"start": v(26.5, 0) * mm, "end": v(31.34, 0) * mm});
            skLineSegment(sketch, "E152", {"start": v(-26.5, 0) * mm, "end": v(-31.33, 0) * mm});
            skLineSegment(sketch, "E153", {"start": v(-26.5, 39.1) * mm, "end": v(-31.33, 0) * mm});
            skLineSegment(sketch, "E154", {"start": v(-31.33, 0) * mm, "end": v(-37.23, 0) * mm});
            skLineSegment(sketch, "E155", {"start": v(31.34, 0) * mm, "end": v(37.24, 0) * mm});
            skLineSegment(sketch, "E156", {"start": v(-37.23, 0) * mm, "end": v(-37.23, -9.4) * mm});
            skLineSegment(sketch, "E157", {"start": v(37.24, 0) * mm, "end": v(37.24, -9.4) * mm});
            skLineSegment(sketch, "E158.bottom", {"start": v(-44.45, -17.78) * mm, "end": v(44.45, -17.78) * mm});
            skLineSegment(sketch, "E158.top", {"start": v(-44.45, 17.78) * mm, "end": v(44.45, 17.78) * mm});
            skLineSegment(sketch, "E158.left", {"start": v(-44.45, -17.78) * mm, "end": v(-44.45, 17.78) * mm});
            skLineSegment(sketch, "E158.right", {"start": v(44.45, -17.78) * mm, "end": v(44.45, 17.78) * mm});
            skLineSegment(sketch, "E159", {"start": v(-37.23, -9.4) * mm, "end": v(-44.45, -17.78) * mm});
            skLineSegment(sketch, "E160", {"start": v(0, 17.78) * mm, "end": v(-40.64, 17.78) * mm});
            skLineSegment(sketch, "E161", {"start": v(-44.45, -17.78) * mm, "end": v(-40.64, 17.78) * mm});
            skLineSegment(sketch, "E162", {"start": v(-40.64, 17.78) * mm, "end": v(-26.5, 39.1) * mm});
            skLineSegment(sketch, "E163", {"start": v(37.24, -9.4) * mm, "end": v(44.45, -17.78) * mm});
            skLineSegment(sketch, "E164", {"start": v(0, 17.78) * mm, "end": v(40.64, 17.78) * mm});
            skLineSegment(sketch, "E165", {"start": v(44.45, -17.78) * mm, "end": v(40.64, 17.78) * mm});
            skLineSegment(sketch, "E166", {"start": v(40.64, 17.78) * mm, "end": v(26.5, 39.1) * mm});
            skLineSegment(sketch, "E167.bottom", {"start": v(-44.45, 14.76) * mm, "end": v(44.45, 14.76) * mm});
            skLineSegment(sketch, "E167.top", {"start": v(-44.45, 12.22) * mm, "end": v(44.45, 12.22) * mm});
            skLineSegment(sketch, "E167.left", {"start": v(-44.45, 14.76) * mm, "end": v(-44.45, 12.22) * mm});
            skLineSegment(sketch, "E167.right", {"start": v(44.45, 14.76) * mm, "end": v(44.45, 12.22) * mm});
            skPoint(sketch, "E167.middle", {"position": v(0, 13.49) * mm});
            skLineSegment(sketch, "E168.bottom", {"start": v(-44.45, 9.36) * mm, "end": v(44.45, 9.36) * mm});
            skLineSegment(sketch, "E168.top", {"start": v(-44.45, 6.82) * mm, "end": v(44.45, 6.82) * mm});
            skLineSegment(sketch, "E168.left", {"start": v(-44.45, 9.36) * mm, "end": v(-44.45, 6.82) * mm});
            skLineSegment(sketch, "E168.right", {"start": v(44.45, 9.36) * mm, "end": v(44.45, 6.82) * mm});
            skPoint(sketch, "E168.middle", {"position": v(0, 8.09) * mm});
            skLineSegment(sketch, "E169.bottom", {"start": v(-44.45, 4.1) * mm, "end": v(44.45, 4.1) * mm});
            skLineSegment(sketch, "E169.top", {"start": v(-44.45, 1.55) * mm, "end": v(44.45, 1.55) * mm});
            skLineSegment(sketch, "E169.left", {"start": v(-44.45, 4.1) * mm, "end": v(-44.45, 1.55) * mm});
            skLineSegment(sketch, "E169.right", {"start": v(44.45, 4.1) * mm, "end": v(44.45, 1.55) * mm});
            skPoint(sketch, "E169.middle", {"position": v(0, 2.82) * mm});
            skLineSegment(sketch, "E170", {"start": v(-37.23, 17.78) * mm, "end": v(-44.45, -17.78) * mm});
            skLineSegment(sketch, "E171", {"start": v(37.24, 17.78) * mm, "end": v(44.45, -17.78) * mm});
            skLineSegment(sketch, "E172", {"start": v(26.5, 39.1) * mm, "end": v(31.34, 0) * mm});
            skSolve(sketch);
        }
        {
            var Q0;
            {var subQ0=sQuery(id+"F49.wireOp",EDGE,"E162");Q0=makeQuery(id+"F49.imprint","IMPRINT",FACE,{"disambiguationData":[TD([[makeQuery(id+"F49.imprint","IMPRINT",EDGE,{"derivedFrom":subQ0}),-1.0]])]});}
            var Q1;
            {var subQ0=sQuery(id+"F49.wireOp",EDGE,"E161");var subQ5=sQuery(id+"F49.wireOp",EDGE,"E167.bottom");var subQ6=makeQuery(id+"F49.imprint","INTERSECT",VERTEX,{"derivedFrom":[subQ0,subQ5]});Q1=makeQuery(id+"F49.imprint","IMPRINT",FACE,{"disambiguationData":[TD([[makeQuery(id+"F49.imprint","IMPRINT",EDGE,{"disambiguationData":[TD([[subQ6,-1.0]])],"derivedFrom":subQ5}),1.0]])]});}
            var Q2;
            {var subQ0=sQuery(id+"F49.wireOp",EDGE,"E167.top");var subQ1=sQuery(id+"F49.wireOp",EDGE,"E161");var subQ2=makeQuery(id+"F49.imprint","INTERSECT",VERTEX,{"derivedFrom":[subQ1,subQ0]});Q2=makeQuery(id+"F49.imprint","IMPRINT",FACE,{"disambiguationData":[TD([[makeQuery(id+"F49.imprint","IMPRINT",EDGE,{"disambiguationData":[TD([[subQ2,-1.0]])],"derivedFrom":subQ1}),-1.0]])]});}
            var Q3;
            {var subQ0=sQuery(id+"F49.wireOp",EDGE,"E168.bottom");var subQ1=sQuery(id+"F49.wireOp",EDGE,"E161");var subQ2=makeQuery(id+"F49.imprint","INTERSECT",VERTEX,{"derivedFrom":[subQ1,subQ0]});Q3=makeQuery(id+"F49.imprint","IMPRINT",FACE,{"disambiguationData":[TD([[makeQuery(id+"F49.imprint","IMPRINT",EDGE,{"disambiguationData":[TD([[subQ2,-1.0]])],"derivedFrom":subQ1}),-1.0]])]});}
            var Q4;
            {var subQ0=sQuery(id+"F49.wireOp",EDGE,"E167.bottom");var subQ1=sQuery(id+"F49.wireOp",EDGE,"E153");var subQ2=makeQuery(id+"F49.imprint","INTERSECT",VERTEX,{"derivedFrom":[subQ1,subQ0]});Q4=makeQuery(id+"F49.imprint","IMPRINT",FACE,{"disambiguationData":[TD([[makeQuery(id+"F49.imprint","IMPRINT",EDGE,{"disambiguationData":[TD([[subQ2,-1.0]])],"derivedFrom":subQ1}),-1.0]])]});}
            var Q5;
            {var subQ0=sQuery(id+"F49.wireOp",EDGE,"E168.top");var subQ1=sQuery(id+"F49.wireOp",EDGE,"E161");var subQ2=makeQuery(id+"F49.imprint","INTERSECT",VERTEX,{"derivedFrom":[subQ1,subQ0]});Q5=makeQuery(id+"F49.imprint","IMPRINT",FACE,{"disambiguationData":[TD([[makeQuery(id+"F49.imprint","IMPRINT",EDGE,{"disambiguationData":[TD([[subQ2,-1.0]])],"derivedFrom":subQ1}),-1.0]])]});}
            var Q6;
            {var subQ0=sQuery(id+"F49.wireOp",EDGE,"E169.bottom");var subQ1=sQuery(id+"F49.wireOp",EDGE,"E161");var subQ2=makeQuery(id+"F49.imprint","INTERSECT",VERTEX,{"derivedFrom":[subQ1,subQ0]});Q6=makeQuery(id+"F49.imprint","IMPRINT",FACE,{"disambiguationData":[TD([[makeQuery(id+"F49.imprint","IMPRINT",EDGE,{"disambiguationData":[TD([[subQ2,-1.0]])],"derivedFrom":subQ1}),-1.0]])]});}
            var Q7;
            {var subQ0=sQuery(id+"F49.wireOp",EDGE,"E168.bottom");var subQ1=sQuery(id+"F49.wireOp",EDGE,"E153");var subQ2=makeQuery(id+"F49.imprint","INTERSECT",VERTEX,{"derivedFrom":[subQ1,subQ0]});Q7=makeQuery(id+"F49.imprint","IMPRINT",FACE,{"disambiguationData":[TD([[makeQuery(id+"F49.imprint","IMPRINT",EDGE,{"disambiguationData":[TD([[subQ2,-1.0]])],"derivedFrom":subQ1}),-1.0]])]});}
            var Q8;
            {var subQ0=sQuery(id+"F49.wireOp",EDGE,"E169.top");var subQ1=sQuery(id+"F49.wireOp",EDGE,"E161");var subQ2=makeQuery(id+"F49.imprint","INTERSECT",VERTEX,{"derivedFrom":[subQ1,subQ0]});Q8=makeQuery(id+"F49.imprint","IMPRINT",FACE,{"disambiguationData":[TD([[makeQuery(id+"F49.imprint","IMPRINT",EDGE,{"disambiguationData":[TD([[subQ2,-1.0]])],"derivedFrom":subQ1}),-1.0]])]});}
            var Q9;
            {var subQ0=sQuery(id+"F49.wireOp",EDGE,"E169.bottom");var subQ1=sQuery(id+"F49.wireOp",EDGE,"E153");var subQ2=makeQuery(id+"F49.imprint","INTERSECT",VERTEX,{"derivedFrom":[subQ1,subQ0]});Q9=makeQuery(id+"F49.imprint","IMPRINT",FACE,{"disambiguationData":[TD([[makeQuery(id+"F49.imprint","IMPRINT",EDGE,{"disambiguationData":[TD([[subQ2,-1.0]])],"derivedFrom":subQ1}),-1.0]])]});}
            var Q10;
            {var subQ1=sQuery(id+"F49.wireOp",EDGE,"E161");var subQ3=sQuery(id+"F49.wireOp",EDGE,"E169.top");var subQ4=makeQuery(id+"F49.imprint","INTERSECT",VERTEX,{"derivedFrom":[subQ1,subQ3]});Q10=makeQuery(id+"F49.imprint","IMPRINT",FACE,{"disambiguationData":[TD([[makeQuery(id+"F49.imprint","IMPRINT",EDGE,{"disambiguationData":[TD([[subQ4,-1.0]])],"derivedFrom":subQ3}),-1.0]])]});}
            var Q11;
            {var subQ6=sQuery(id+"F49.wireOp",EDGE,"E154");Q11=makeQuery(id+"F49.imprint","IMPRINT",FACE,{"disambiguationData":[TD([[makeQuery(id+"F49.imprint","IMPRINT",EDGE,{"derivedFrom":subQ6}),-1.0]])]});}
            var Q12;
            {var subQ4=sQuery(id+"F49.wireOp",EDGE,"E166");Q12=makeQuery(id+"F49.imprint","IMPRINT",FACE,{"disambiguationData":[TD([[makeQuery(id+"F49.imprint","IMPRINT",EDGE,{"derivedFrom":subQ4}),1.0]])]});}
            var Q13;
            {var subQ0=sQuery(id+"F49.wireOp",EDGE,"E165");var subQ5=sQuery(id+"F49.wireOp",EDGE,"E167.bottom");var subQ6=makeQuery(id+"F49.imprint","INTERSECT",VERTEX,{"derivedFrom":[subQ0,subQ5]});Q13=makeQuery(id+"F49.imprint","IMPRINT",FACE,{"disambiguationData":[TD([[makeQuery(id+"F49.imprint","IMPRINT",EDGE,{"disambiguationData":[TD([[subQ6,1.0]])],"derivedFrom":subQ5}),1.0]])]});}
            var Q14;
            {var subQ0=sQuery(id+"F49.wireOp",EDGE,"E167.top");var subQ1=sQuery(id+"F49.wireOp",EDGE,"E165");var subQ2=makeQuery(id+"F49.imprint","INTERSECT",VERTEX,{"derivedFrom":[subQ1,subQ0]});Q14=makeQuery(id+"F49.imprint","IMPRINT",FACE,{"disambiguationData":[TD([[makeQuery(id+"F49.imprint","IMPRINT",EDGE,{"disambiguationData":[TD([[subQ2,-1.0]])],"derivedFrom":subQ1}),1.0]])]});}
            var Q15;
            {var subQ0=sQuery(id+"F49.wireOp",EDGE,"E168.bottom");var subQ1=sQuery(id+"F49.wireOp",EDGE,"E165");var subQ2=makeQuery(id+"F49.imprint","INTERSECT",VERTEX,{"derivedFrom":[subQ1,subQ0]});Q15=makeQuery(id+"F49.imprint","IMPRINT",FACE,{"disambiguationData":[TD([[makeQuery(id+"F49.imprint","IMPRINT",EDGE,{"disambiguationData":[TD([[subQ2,-1.0]])],"derivedFrom":subQ1}),1.0]])]});}
            var Q16;
            {var subQ0=sQuery(id+"F49.wireOp",EDGE,"E168.top");var subQ1=sQuery(id+"F49.wireOp",EDGE,"E165");var subQ2=makeQuery(id+"F49.imprint","INTERSECT",VERTEX,{"derivedFrom":[subQ1,subQ0]});Q16=makeQuery(id+"F49.imprint","IMPRINT",FACE,{"disambiguationData":[TD([[makeQuery(id+"F49.imprint","IMPRINT",EDGE,{"disambiguationData":[TD([[subQ2,-1.0]])],"derivedFrom":subQ1}),1.0]])]});}
            var Q17;
            {var subQ0=sQuery(id+"F49.wireOp",EDGE,"E169.bottom");var subQ1=sQuery(id+"F49.wireOp",EDGE,"E165");var subQ2=makeQuery(id+"F49.imprint","INTERSECT",VERTEX,{"derivedFrom":[subQ1,subQ0]});Q17=makeQuery(id+"F49.imprint","IMPRINT",FACE,{"disambiguationData":[TD([[makeQuery(id+"F49.imprint","IMPRINT",EDGE,{"disambiguationData":[TD([[subQ2,-1.0]])],"derivedFrom":subQ1}),1.0]])]});}
            var Q18;
            {var subQ0=sQuery(id+"F49.wireOp",EDGE,"E172");var subQ1=sQuery(id+"F49.wireOp",EDGE,"E167.bottom");var subQ2=makeQuery(id+"F49.imprint","INTERSECT",VERTEX,{"derivedFrom":[subQ1,subQ0]});Q18=makeQuery(id+"F49.imprint","IMPRINT",FACE,{"disambiguationData":[TD([[makeQuery(id+"F49.imprint","IMPRINT",EDGE,{"disambiguationData":[TD([[subQ2,-1.0]])],"derivedFrom":subQ1}),-1.0]])]});}
            var Q19;
            {var subQ0=sQuery(id+"F49.wireOp",EDGE,"E172");var subQ1=sQuery(id+"F49.wireOp",EDGE,"E168.bottom");var subQ2=makeQuery(id+"F49.imprint","INTERSECT",VERTEX,{"derivedFrom":[subQ1,subQ0]});Q19=makeQuery(id+"F49.imprint","IMPRINT",FACE,{"disambiguationData":[TD([[makeQuery(id+"F49.imprint","IMPRINT",EDGE,{"disambiguationData":[TD([[subQ2,-1.0]])],"derivedFrom":subQ1}),-1.0]])]});}
            var Q20;
            {var subQ0=sQuery(id+"F49.wireOp",EDGE,"E169.top");var subQ1=sQuery(id+"F49.wireOp",EDGE,"E165");var subQ2=makeQuery(id+"F49.imprint","INTERSECT",VERTEX,{"derivedFrom":[subQ1,subQ0]});Q20=makeQuery(id+"F49.imprint","IMPRINT",FACE,{"disambiguationData":[TD([[makeQuery(id+"F49.imprint","IMPRINT",EDGE,{"disambiguationData":[TD([[subQ2,-1.0]])],"derivedFrom":subQ1}),1.0]])]});}
            var Q21;
            {var subQ0=sQuery(id+"F49.wireOp",EDGE,"E172");var subQ1=sQuery(id+"F49.wireOp",EDGE,"E169.bottom");var subQ2=makeQuery(id+"F49.imprint","INTERSECT",VERTEX,{"derivedFrom":[subQ1,subQ0]});Q21=makeQuery(id+"F49.imprint","IMPRINT",FACE,{"disambiguationData":[TD([[makeQuery(id+"F49.imprint","IMPRINT",EDGE,{"disambiguationData":[TD([[subQ2,-1.0]])],"derivedFrom":subQ1}),-1.0]])]});}
            var Q22;
            {var subQ6=sQuery(id+"F49.wireOp",EDGE,"E155");Q22=makeQuery(id+"F49.imprint","IMPRINT",FACE,{"disambiguationData":[TD([[makeQuery(id+"F49.imprint","IMPRINT",EDGE,{"derivedFrom":subQ6}),1.0]])]});}
            var Q23;
            {var subQ1=sQuery(id+"F49.wireOp",EDGE,"E165");var subQ3=sQuery(id+"F49.wireOp",EDGE,"E169.top");var subQ4=makeQuery(id+"F49.imprint","INTERSECT",VERTEX,{"derivedFrom":[subQ1,subQ3]});Q23=makeQuery(id+"F49.imprint","IMPRINT",FACE,{"disambiguationData":[TD([[makeQuery(id+"F49.imprint","IMPRINT",EDGE,{"disambiguationData":[TD([[subQ4,1.0]])],"derivedFrom":subQ3}),-1.0]])]});}
            extrude(context, id + "F50", {"entities" : qUnion([Q0, Q1, Q2, Q3, Q4, Q5, Q6, Q7, Q8, Q9, Q10, Q11, Q12, Q13, Q14, Q15, Q16, Q17, Q18, Q19, Q20, Q21, Q22, Q23]), "depth" : 1.78 * mm, "offsetDistance" : 25.4 * mm, "hasSecondDirection" : true, "secondDirectionOppositeDirection" : true, "secondDirectionDepth" : 1.78 * mm});
        }
        {
            var Q0;
            Q0=makeQuery(id+"F50.opExtrude","SWEPT_FACE",FACE,{"disambiguationData":[OSD([sQuery(id+"F49.wireOp",EDGE,"E161")])]});
            var Q1;
            Q1=makeQuery(id+"F50.opExtrude","CAP_EDGE",EDGE,{"disambiguationData":[OSD([sQuery(id+"F49.wireOp",EDGE,"E159")])],"isStart":false});
            var Q2;
            Q2=makeQuery(id+"F50.opExtrude","CAP_EDGE",EDGE,{"disambiguationData":[OSD([sQuery(id+"F49.wireOp",EDGE,"E159")])],"isStart":true});
            var Q3;
            Q3=makeQuery(id+"F50.opExtrude","CAP_EDGE",EDGE,{"disambiguationData":[OSD([sQuery(id+"F49.wireOp",EDGE,"E162")])],"isStart":false});
            var Q4;
            Q4=makeQuery(id+"F50.opExtrude","CAP_EDGE",EDGE,{"disambiguationData":[OSD([sQuery(id+"F49.wireOp",EDGE,"E162")])],"isStart":true});
            var Q5;
            {var subQ0=sQuery(id+"F49.wireOp",EDGE,"E169.bottom");Q5=makeQuery(id+"F50.opExtrude","CAP_EDGE",EDGE,{"disambiguationData":[OSD([subQ0]),TDD([makeQuery(id+"F49.imprint","IMPRINT",EDGE,{"disambiguationData":[TD([[makeQuery(id+"F49.imprint","INTERSECT",VERTEX,{"derivedFrom":[sQuery(id+"F49.wireOp",EDGE,"E153"),subQ0]}),1.0]])],"derivedFrom":subQ0})])],"isStart":false});}
            var Q6;
            {var subQ0=sQuery(id+"F49.wireOp",EDGE,"E168.bottom");Q6=makeQuery(id+"F50.opExtrude","CAP_EDGE",EDGE,{"disambiguationData":[OSD([subQ0]),TDD([makeQuery(id+"F49.imprint","IMPRINT",EDGE,{"disambiguationData":[TD([[makeQuery(id+"F49.imprint","INTERSECT",VERTEX,{"derivedFrom":[sQuery(id+"F49.wireOp",EDGE,"E153"),subQ0]}),1.0]])],"derivedFrom":subQ0})])],"isStart":false});}
            var Q7;
            {var subQ0=sQuery(id+"F49.wireOp",EDGE,"E167.bottom");Q7=makeQuery(id+"F50.opExtrude","CAP_EDGE",EDGE,{"disambiguationData":[OSD([subQ0]),TDD([makeQuery(id+"F49.imprint","IMPRINT",EDGE,{"disambiguationData":[TD([[makeQuery(id+"F49.imprint","INTERSECT",VERTEX,{"derivedFrom":[sQuery(id+"F49.wireOp",EDGE,"E153"),subQ0]}),1.0]])],"derivedFrom":subQ0})])],"isStart":false});}
            var Q8;
            {var subQ0=sQuery(id+"F49.wireOp",EDGE,"E169.bottom");Q8=makeQuery(id+"F50.opExtrude","CAP_EDGE",EDGE,{"disambiguationData":[OSD([subQ0]),TDD([makeQuery(id+"F49.imprint","IMPRINT",EDGE,{"disambiguationData":[TD([[makeQuery(id+"F49.imprint","INTERSECT",VERTEX,{"derivedFrom":[sQuery(id+"F49.wireOp",EDGE,"E153"),subQ0]}),1.0]])],"derivedFrom":subQ0})])],"isStart":true});}
            var Q9;
            {var subQ0=sQuery(id+"F49.wireOp",EDGE,"E168.bottom");Q9=makeQuery(id+"F50.opExtrude","CAP_EDGE",EDGE,{"disambiguationData":[OSD([subQ0]),TDD([makeQuery(id+"F49.imprint","IMPRINT",EDGE,{"disambiguationData":[TD([[makeQuery(id+"F49.imprint","INTERSECT",VERTEX,{"derivedFrom":[sQuery(id+"F49.wireOp",EDGE,"E153"),subQ0]}),1.0]])],"derivedFrom":subQ0})])],"isStart":true});}
            var Q10;
            {var subQ0=sQuery(id+"F49.wireOp",EDGE,"E167.bottom");Q10=makeQuery(id+"F50.opExtrude","CAP_EDGE",EDGE,{"disambiguationData":[OSD([subQ0]),TDD([makeQuery(id+"F49.imprint","IMPRINT",EDGE,{"disambiguationData":[TD([[makeQuery(id+"F49.imprint","INTERSECT",VERTEX,{"derivedFrom":[sQuery(id+"F49.wireOp",EDGE,"E153"),subQ0]}),1.0]])],"derivedFrom":subQ0})])],"isStart":true});}
            var Q11;
            Q11=makeQuery(id+"F48.opExtrude","SWEPT_FACE",FACE,{"disambiguationData":[OSD([sQuery(id+"F47.wireOp",EDGE,"E138")])]});
            var Q12;
            Q12=makeQuery(id+"F48.opExtrude","CAP_EDGE",EDGE,{"disambiguationData":[OSD([sQuery(id+"F47.wireOp",EDGE,"E139")])],"isStart":true});
            var Q13;
            Q13=makeQuery(id+"F48.opExtrude","CAP_EDGE",EDGE,{"disambiguationData":[OSD([sQuery(id+"F47.wireOp",EDGE,"E139")])],"isStart":false});
            var Q14;
            {var subQ0=sQuery(id+"F47.wireOp",EDGE,"E144.bottom");Q14=makeQuery(id+"F48.opExtrude","CAP_EDGE",EDGE,{"disambiguationData":[OSD([subQ0]),TDD([makeQuery(id+"F47.imprint","IMPRINT",EDGE,{"disambiguationData":[TD([[makeQuery(id+"F47.imprint","INTERSECT",VERTEX,{"derivedFrom":[sQuery(id+"F47.wireOp",EDGE,"E130"),subQ0]}),1.0]])],"derivedFrom":subQ0})])],"isStart":true});}
            var Q15;
            {var subQ0=sQuery(id+"F47.wireOp",EDGE,"E145.bottom");Q15=makeQuery(id+"F48.opExtrude","CAP_EDGE",EDGE,{"disambiguationData":[OSD([subQ0]),TDD([makeQuery(id+"F47.imprint","IMPRINT",EDGE,{"disambiguationData":[TD([[makeQuery(id+"F47.imprint","INTERSECT",VERTEX,{"derivedFrom":[sQuery(id+"F47.wireOp",EDGE,"E130"),subQ0]}),1.0]])],"derivedFrom":subQ0})])],"isStart":true});}
            var Q16;
            {var subQ0=sQuery(id+"F47.wireOp",EDGE,"E146.bottom");Q16=makeQuery(id+"F48.opExtrude","CAP_EDGE",EDGE,{"disambiguationData":[OSD([subQ0]),TDD([makeQuery(id+"F47.imprint","IMPRINT",EDGE,{"disambiguationData":[TD([[makeQuery(id+"F47.imprint","INTERSECT",VERTEX,{"derivedFrom":[sQuery(id+"F47.wireOp",EDGE,"E130"),subQ0]}),1.0]])],"derivedFrom":subQ0})])],"isStart":true});}
            var Q17;
            Q17=makeQuery(id+"F48.opExtrude","CAP_EDGE",EDGE,{"disambiguationData":[OSD([sQuery(id+"F47.wireOp",EDGE,"E136")])],"isStart":true});
            var Q18;
            Q18=makeQuery(id+"F48.opExtrude","CAP_EDGE",EDGE,{"disambiguationData":[OSD([sQuery(id+"F47.wireOp",EDGE,"E136")])],"isStart":false});
            var Q19;
            {var subQ0=sQuery(id+"F47.wireOp",EDGE,"E146.bottom");Q19=makeQuery(id+"F48.opExtrude","CAP_EDGE",EDGE,{"disambiguationData":[OSD([subQ0]),TDD([makeQuery(id+"F47.imprint","IMPRINT",EDGE,{"disambiguationData":[TD([[makeQuery(id+"F47.imprint","INTERSECT",VERTEX,{"derivedFrom":[sQuery(id+"F47.wireOp",EDGE,"E130"),subQ0]}),1.0]])],"derivedFrom":subQ0})])],"isStart":false});}
            var Q20;
            {var subQ0=sQuery(id+"F47.wireOp",EDGE,"E144.bottom");Q20=makeQuery(id+"F48.opExtrude","CAP_EDGE",EDGE,{"disambiguationData":[OSD([subQ0]),TDD([makeQuery(id+"F47.imprint","IMPRINT",EDGE,{"disambiguationData":[TD([[makeQuery(id+"F47.imprint","INTERSECT",VERTEX,{"derivedFrom":[sQuery(id+"F47.wireOp",EDGE,"E130"),subQ0]}),1.0]])],"derivedFrom":subQ0})])],"isStart":false});}
            var Q21;
            {var subQ0=sQuery(id+"F47.wireOp",EDGE,"E145.bottom");Q21=makeQuery(id+"F48.opExtrude","CAP_EDGE",EDGE,{"disambiguationData":[OSD([subQ0]),TDD([makeQuery(id+"F47.imprint","IMPRINT",EDGE,{"disambiguationData":[TD([[makeQuery(id+"F47.imprint","INTERSECT",VERTEX,{"derivedFrom":[sQuery(id+"F47.wireOp",EDGE,"E130"),subQ0]}),1.0]])],"derivedFrom":subQ0})])],"isStart":false});}
            var Q22;
            Q22=makeQuery(id+"F50.opExtrude","SWEPT_FACE",FACE,{"disambiguationData":[OSD([sQuery(id+"F49.wireOp",EDGE,"E165")])]});
            var Q23;
            {var subQ0=sQuery(id+"F49.wireOp",EDGE,"E167.bottom");Q23=makeQuery(id+"F50.opExtrude","CAP_EDGE",EDGE,{"disambiguationData":[OSD([subQ0]),TDD([makeQuery(id+"F49.imprint","IMPRINT",EDGE,{"disambiguationData":[TD([[makeQuery(id+"F49.imprint","INTERSECT",VERTEX,{"derivedFrom":[subQ0,sQuery(id+"F49.wireOp",EDGE,"E172")]}),-1.0]])],"derivedFrom":subQ0})])],"isStart":false});}
            var Q24;
            {var subQ0=sQuery(id+"F49.wireOp",EDGE,"E168.bottom");Q24=makeQuery(id+"F50.opExtrude","CAP_EDGE",EDGE,{"disambiguationData":[OSD([subQ0]),TDD([makeQuery(id+"F49.imprint","IMPRINT",EDGE,{"disambiguationData":[TD([[makeQuery(id+"F49.imprint","INTERSECT",VERTEX,{"derivedFrom":[subQ0,sQuery(id+"F49.wireOp",EDGE,"E172")]}),-1.0]])],"derivedFrom":subQ0})])],"isStart":false});}
            var Q25;
            {var subQ0=sQuery(id+"F49.wireOp",EDGE,"E169.bottom");Q25=makeQuery(id+"F50.opExtrude","CAP_EDGE",EDGE,{"disambiguationData":[OSD([subQ0]),TDD([makeQuery(id+"F49.imprint","IMPRINT",EDGE,{"disambiguationData":[TD([[makeQuery(id+"F49.imprint","INTERSECT",VERTEX,{"derivedFrom":[subQ0,sQuery(id+"F49.wireOp",EDGE,"E172")]}),-1.0]])],"derivedFrom":subQ0})])],"isStart":false});}
            var Q26;
            Q26=makeQuery(id+"F50.opExtrude","CAP_EDGE",EDGE,{"disambiguationData":[OSD([sQuery(id+"F49.wireOp",EDGE,"E163")])],"isStart":false});
            var Q27;
            Q27=makeQuery(id+"F50.opExtrude","CAP_EDGE",EDGE,{"disambiguationData":[OSD([sQuery(id+"F49.wireOp",EDGE,"E166")])],"isStart":false});
            var Q28;
            Q28=makeQuery(id+"F50.opExtrude","CAP_EDGE",EDGE,{"disambiguationData":[OSD([sQuery(id+"F49.wireOp",EDGE,"E166")])],"isStart":true});
            var Q29;
            Q29=makeQuery(id+"F50.opExtrude","CAP_EDGE",EDGE,{"disambiguationData":[OSD([sQuery(id+"F49.wireOp",EDGE,"E163")])],"isStart":true});
            var Q30;
            {var subQ0=sQuery(id+"F49.wireOp",EDGE,"E169.bottom");Q30=makeQuery(id+"F50.opExtrude","CAP_EDGE",EDGE,{"disambiguationData":[OSD([subQ0]),TDD([makeQuery(id+"F49.imprint","IMPRINT",EDGE,{"disambiguationData":[TD([[makeQuery(id+"F49.imprint","INTERSECT",VERTEX,{"derivedFrom":[subQ0,sQuery(id+"F49.wireOp",EDGE,"E172")]}),-1.0]])],"derivedFrom":subQ0})])],"isStart":true});}
            var Q31;
            {var subQ0=sQuery(id+"F49.wireOp",EDGE,"E168.bottom");Q31=makeQuery(id+"F50.opExtrude","CAP_EDGE",EDGE,{"disambiguationData":[OSD([subQ0]),TDD([makeQuery(id+"F49.imprint","IMPRINT",EDGE,{"disambiguationData":[TD([[makeQuery(id+"F49.imprint","INTERSECT",VERTEX,{"derivedFrom":[subQ0,sQuery(id+"F49.wireOp",EDGE,"E172")]}),-1.0]])],"derivedFrom":subQ0})])],"isStart":true});}
            var Q32;
            {var subQ0=sQuery(id+"F49.wireOp",EDGE,"E167.bottom");Q32=makeQuery(id+"F50.opExtrude","CAP_EDGE",EDGE,{"disambiguationData":[OSD([subQ0]),TDD([makeQuery(id+"F49.imprint","IMPRINT",EDGE,{"disambiguationData":[TD([[makeQuery(id+"F49.imprint","INTERSECT",VERTEX,{"derivedFrom":[subQ0,sQuery(id+"F49.wireOp",EDGE,"E172")]}),-1.0]])],"derivedFrom":subQ0})])],"isStart":true});}
            var Q33;
            Q33=makeQuery(id+"F48.opExtrude","SWEPT_FACE",FACE,{"disambiguationData":[OSD([sQuery(id+"F47.wireOp",EDGE,"E142")])]});
            var Q34;
            Q34=makeQuery(id+"F48.opExtrude","CAP_EDGE",EDGE,{"disambiguationData":[OSD([sQuery(id+"F47.wireOp",EDGE,"E143")])],"isStart":false});
            var Q35;
            Q35=makeQuery(id+"F48.opExtrude","CAP_EDGE",EDGE,{"disambiguationData":[OSD([sQuery(id+"F47.wireOp",EDGE,"E143")])],"isStart":true});
            var Q36;
            {var subQ0=sQuery(id+"F47.wireOp",EDGE,"E144.bottom");Q36=makeQuery(id+"F48.opExtrude","CAP_EDGE",EDGE,{"disambiguationData":[OSD([subQ0]),TDD([makeQuery(id+"F47.imprint","IMPRINT",EDGE,{"disambiguationData":[TD([[makeQuery(id+"F47.imprint","INTERSECT",VERTEX,{"derivedFrom":[subQ0,sQuery(id+"F47.wireOp",EDGE,"E149")]}),-1.0]])],"derivedFrom":subQ0})])],"isStart":false});}
            var Q37;
            {var subQ0=sQuery(id+"F47.wireOp",EDGE,"E145.bottom");Q37=makeQuery(id+"F48.opExtrude","CAP_EDGE",EDGE,{"disambiguationData":[OSD([subQ0]),TDD([makeQuery(id+"F47.imprint","IMPRINT",EDGE,{"disambiguationData":[TD([[makeQuery(id+"F47.imprint","INTERSECT",VERTEX,{"derivedFrom":[subQ0,sQuery(id+"F47.wireOp",EDGE,"E149")]}),-1.0]])],"derivedFrom":subQ0})])],"isStart":false});}
            var Q38;
            {var subQ0=sQuery(id+"F47.wireOp",EDGE,"E146.bottom");Q38=makeQuery(id+"F48.opExtrude","CAP_EDGE",EDGE,{"disambiguationData":[OSD([subQ0]),TDD([makeQuery(id+"F47.imprint","IMPRINT",EDGE,{"disambiguationData":[TD([[makeQuery(id+"F47.imprint","INTERSECT",VERTEX,{"derivedFrom":[subQ0,sQuery(id+"F47.wireOp",EDGE,"E149")]}),-1.0]])],"derivedFrom":subQ0})])],"isStart":false});}
            var Q39;
            Q39=makeQuery(id+"F48.opExtrude","CAP_EDGE",EDGE,{"disambiguationData":[OSD([sQuery(id+"F47.wireOp",EDGE,"E140")])],"isStart":false});
            var Q40;
            Q40=makeQuery(id+"F48.opExtrude","CAP_EDGE",EDGE,{"disambiguationData":[OSD([sQuery(id+"F47.wireOp",EDGE,"E140")])],"isStart":true});
            var Q41;
            {var subQ0=sQuery(id+"F47.wireOp",EDGE,"E146.bottom");Q41=makeQuery(id+"F48.opExtrude","CAP_EDGE",EDGE,{"disambiguationData":[OSD([subQ0]),TDD([makeQuery(id+"F47.imprint","IMPRINT",EDGE,{"disambiguationData":[TD([[makeQuery(id+"F47.imprint","INTERSECT",VERTEX,{"derivedFrom":[subQ0,sQuery(id+"F47.wireOp",EDGE,"E149")]}),-1.0]])],"derivedFrom":subQ0})])],"isStart":true});}
            var Q42;
            {var subQ0=sQuery(id+"F47.wireOp",EDGE,"E145.bottom");Q42=makeQuery(id+"F48.opExtrude","CAP_EDGE",EDGE,{"disambiguationData":[OSD([subQ0]),TDD([makeQuery(id+"F47.imprint","IMPRINT",EDGE,{"disambiguationData":[TD([[makeQuery(id+"F47.imprint","INTERSECT",VERTEX,{"derivedFrom":[subQ0,sQuery(id+"F47.wireOp",EDGE,"E149")]}),-1.0]])],"derivedFrom":subQ0})])],"isStart":true});}
            var Q43;
            {var subQ0=sQuery(id+"F47.wireOp",EDGE,"E144.bottom");Q43=makeQuery(id+"F48.opExtrude","CAP_EDGE",EDGE,{"disambiguationData":[OSD([subQ0]),TDD([makeQuery(id+"F47.imprint","IMPRINT",EDGE,{"disambiguationData":[TD([[makeQuery(id+"F47.imprint","INTERSECT",VERTEX,{"derivedFrom":[subQ0,sQuery(id+"F47.wireOp",EDGE,"E149")]}),-1.0]])],"derivedFrom":subQ0})])],"isStart":true});}
            fillet(context, id + "F51", {"entities" : qUnion([Q0, Q1, Q2, Q3, Q4, Q5, Q6, Q7, Q8, Q9, Q10, Q11, Q12, Q13, Q14, Q15, Q16, Q17, Q18, Q19, Q20, Q21, Q22, Q23, Q24, Q25, Q26, Q27, Q28, Q29, Q30, Q31, Q32, Q33, Q34, Q35, Q36, Q37, Q38, Q39, Q40, Q41, Q42, Q43]), "radius" : 1.27 * mm, "tangentPropagation" : true, "allowEdgeOverflow" : false});
        }
        {
            var Q0;
            Q0=makeQuery(id+"F1.imprint","IMPRINT",FACE,{"disambiguationData":[TD([[makeQuery(id+"F1.imprint","IMPRINT",EDGE,{"derivedFrom":sQuery(id+"F1.wireOp",EDGE,"E0.bottom")}),-1.0]])]});
            var sketch = newSketch(context, id + "F52", { "sketchPlane" : qUnion([Q0])});
            skCircle(sketch, "E173", {"center": v(0, 0) * mm, "radius": 16.51 * mm});
            skSolve(sketch);
        }
        {
            var Q0;
            Q0 = qSketchRegion(id + "F52", true);
            extrude(context, id + "F53", {"entities" : qUnion([Q0]), "depth" : 6.35 * mm, "offsetDistance" : 25.4 * mm});
        }
        {
            var Q0;
            Q0=makeQuery(id+"F53.opExtrude","CAP_FACE",FACE,{"disambiguationData":[OSD([sQuery(id+"F52.wireOp",EDGE,"E173")])],"isStart":false});
            var sketch = newSketch(context, id + "F54", { "sketchPlane" : qUnion([Q0])});
            skCircle(sketch, "E174", {"center": v(-16.51, 0) * mm, "radius": 1.9 * mm});
            skCircle(sketch, "E175.1.0", {"center": v(-14.3, -8.26) * mm, "radius": 1.9 * mm});
            skCircle(sketch, "E175.2.0", {"center": v(-8.26, -14.3) * mm, "radius": 1.9 * mm});
            skCircle(sketch, "E175.3.0", {"center": v(0, -16.51) * mm, "radius": 1.9 * mm});
            skCircle(sketch, "E175.4.0", {"center": v(8.25, -14.3) * mm, "radius": 1.9 * mm});
            skCircle(sketch, "E175.5.0", {"center": v(14.3, -8.26) * mm, "radius": 1.9 * mm});
            skCircle(sketch, "E175.6.0", {"center": v(16.51, 0) * mm, "radius": 1.9 * mm});
            skCircle(sketch, "E175.7.0", {"center": v(14.3, 8.25) * mm, "radius": 1.9 * mm});
            skCircle(sketch, "E175.8.0", {"center": v(8.26, 14.3) * mm, "radius": 1.9 * mm});
            skCircle(sketch, "E175.9.0", {"center": v(0, 16.51) * mm, "radius": 1.9 * mm});
            skCircle(sketch, "E175.10.0", {"center": v(-8.26, 14.3) * mm, "radius": 1.9 * mm});
            skCircle(sketch, "E175.11.0", {"center": v(-14.3, 8.26) * mm, "radius": 1.9 * mm});
            skPoint(sketch, "E175.center", {"position": v(0, 0) * mm});
            skSolve(sketch);
        }
        {
            var Q0;
            {var subQ0=sQuery(id+"F54.wireOp",EDGE,"E174");var subQ1=makeQuery(id+"F53.opExtrude","CAP_EDGE",EDGE,{"disambiguationData":[OSD([sQuery(id+"F52.wireOp",EDGE,"E173")])],"isStart":false});var subQ2=makeQuery(id+"F54.imprint","INTERSECT",VERTEX,{"disambiguationData":[OD(0.0)],"derivedFrom":[subQ1,subQ0]});Q0=makeQuery(id+"F54.imprint","IMPRINT",FACE,{"disambiguationData":[TD([[makeQuery(id+"F54.imprint","IMPRINT",EDGE,{"disambiguationData":[TD([[subQ2,-1.0]])],"derivedFrom":subQ0}),1.0]])]});}
            var Q1;
            {var subQ0=sQuery(id+"F54.wireOp",EDGE,"E175.11.0");var subQ1=makeQuery(id+"F53.opExtrude","CAP_EDGE",EDGE,{"disambiguationData":[OSD([sQuery(id+"F52.wireOp",EDGE,"E173")])],"isStart":false});var subQ2=makeQuery(id+"F54.imprint","INTERSECT",VERTEX,{"disambiguationData":[OD(0.0)],"derivedFrom":[subQ1,subQ0]});Q1=makeQuery(id+"F54.imprint","IMPRINT",FACE,{"disambiguationData":[TD([[makeQuery(id+"F54.imprint","IMPRINT",EDGE,{"disambiguationData":[TD([[subQ2,-1.0]])],"derivedFrom":subQ0}),1.0]])]});}
            var Q2;
            {var subQ0=sQuery(id+"F54.wireOp",EDGE,"E175.10.0");var subQ1=makeQuery(id+"F53.opExtrude","CAP_EDGE",EDGE,{"disambiguationData":[OSD([sQuery(id+"F52.wireOp",EDGE,"E173")])],"isStart":false});var subQ2=makeQuery(id+"F54.imprint","INTERSECT",VERTEX,{"disambiguationData":[OD(0.0)],"derivedFrom":[subQ1,subQ0]});Q2=makeQuery(id+"F54.imprint","IMPRINT",FACE,{"disambiguationData":[TD([[makeQuery(id+"F54.imprint","IMPRINT",EDGE,{"disambiguationData":[TD([[subQ2,-1.0]])],"derivedFrom":subQ0}),1.0]])]});}
            var Q3;
            {var subQ0=sQuery(id+"F54.wireOp",EDGE,"E175.9.0");var subQ1=makeQuery(id+"F53.opExtrude","CAP_EDGE",EDGE,{"disambiguationData":[OSD([sQuery(id+"F52.wireOp",EDGE,"E173")])],"isStart":false});var subQ2=makeQuery(id+"F54.imprint","INTERSECT",VERTEX,{"disambiguationData":[OD(0.0)],"derivedFrom":[subQ1,subQ0]});Q3=makeQuery(id+"F54.imprint","IMPRINT",FACE,{"disambiguationData":[TD([[makeQuery(id+"F54.imprint","IMPRINT",EDGE,{"disambiguationData":[TD([[subQ2,-1.0]])],"derivedFrom":subQ0}),1.0]])]});}
            var Q4;
            {var subQ0=sQuery(id+"F54.wireOp",EDGE,"E175.8.0");var subQ1=makeQuery(id+"F53.opExtrude","CAP_EDGE",EDGE,{"disambiguationData":[OSD([sQuery(id+"F52.wireOp",EDGE,"E173")])],"isStart":false});var subQ2=makeQuery(id+"F54.imprint","INTERSECT",VERTEX,{"disambiguationData":[OD(0.0)],"derivedFrom":[subQ1,subQ0]});Q4=makeQuery(id+"F54.imprint","IMPRINT",FACE,{"disambiguationData":[TD([[makeQuery(id+"F54.imprint","IMPRINT",EDGE,{"disambiguationData":[TD([[subQ2,-1.0]])],"derivedFrom":subQ0}),1.0]])]});}
            var Q5;
            {var subQ0=sQuery(id+"F54.wireOp",EDGE,"E175.7.0");var subQ1=makeQuery(id+"F53.opExtrude","CAP_EDGE",EDGE,{"disambiguationData":[OSD([sQuery(id+"F52.wireOp",EDGE,"E173")])],"isStart":false});var subQ2=makeQuery(id+"F54.imprint","INTERSECT",VERTEX,{"disambiguationData":[OD(0.0)],"derivedFrom":[subQ1,subQ0]});Q5=makeQuery(id+"F54.imprint","IMPRINT",FACE,{"disambiguationData":[TD([[makeQuery(id+"F54.imprint","IMPRINT",EDGE,{"disambiguationData":[TD([[subQ2,-1.0]])],"derivedFrom":subQ0}),1.0]])]});}
            var Q6;
            {var subQ0=sQuery(id+"F54.wireOp",EDGE,"E175.6.0");var subQ1=makeQuery(id+"F53.opExtrude","CAP_EDGE",EDGE,{"disambiguationData":[OSD([sQuery(id+"F52.wireOp",EDGE,"E173")])],"isStart":false});var subQ2=makeQuery(id+"F54.imprint","INTERSECT",VERTEX,{"disambiguationData":[OD(0.0)],"derivedFrom":[subQ1,subQ0]});Q6=makeQuery(id+"F54.imprint","IMPRINT",FACE,{"disambiguationData":[TD([[makeQuery(id+"F54.imprint","IMPRINT",EDGE,{"disambiguationData":[TD([[subQ2,1.0]])],"derivedFrom":subQ0}),1.0]])]});}
            var Q7;
            {var subQ0=sQuery(id+"F54.wireOp",EDGE,"E175.5.0");var subQ1=makeQuery(id+"F53.opExtrude","CAP_EDGE",EDGE,{"disambiguationData":[OSD([sQuery(id+"F52.wireOp",EDGE,"E173")])],"isStart":false});var subQ2=makeQuery(id+"F54.imprint","INTERSECT",VERTEX,{"disambiguationData":[OD(0.0)],"derivedFrom":[subQ1,subQ0]});Q7=makeQuery(id+"F54.imprint","IMPRINT",FACE,{"disambiguationData":[TD([[makeQuery(id+"F54.imprint","IMPRINT",EDGE,{"disambiguationData":[TD([[subQ2,1.0]])],"derivedFrom":subQ0}),1.0]])]});}
            var Q8;
            {var subQ0=sQuery(id+"F54.wireOp",EDGE,"E175.4.0");var subQ1=makeQuery(id+"F53.opExtrude","CAP_EDGE",EDGE,{"disambiguationData":[OSD([sQuery(id+"F52.wireOp",EDGE,"E173")])],"isStart":false});var subQ2=makeQuery(id+"F54.imprint","INTERSECT",VERTEX,{"disambiguationData":[OD(0.0)],"derivedFrom":[subQ1,subQ0]});Q8=makeQuery(id+"F54.imprint","IMPRINT",FACE,{"disambiguationData":[TD([[makeQuery(id+"F54.imprint","IMPRINT",EDGE,{"disambiguationData":[TD([[subQ2,1.0]])],"derivedFrom":subQ0}),1.0]])]});}
            var Q9;
            {var subQ0=sQuery(id+"F54.wireOp",EDGE,"E175.3.0");var subQ1=makeQuery(id+"F53.opExtrude","CAP_EDGE",EDGE,{"disambiguationData":[OSD([sQuery(id+"F52.wireOp",EDGE,"E173")])],"isStart":false});var subQ2=makeQuery(id+"F54.imprint","INTERSECT",VERTEX,{"disambiguationData":[OD(0.0)],"derivedFrom":[subQ1,subQ0]});Q9=makeQuery(id+"F54.imprint","IMPRINT",FACE,{"disambiguationData":[TD([[makeQuery(id+"F54.imprint","IMPRINT",EDGE,{"disambiguationData":[TD([[subQ2,1.0]])],"derivedFrom":subQ0}),1.0]])]});}
            var Q10;
            {var subQ0=sQuery(id+"F54.wireOp",EDGE,"E175.2.0");var subQ1=makeQuery(id+"F53.opExtrude","CAP_EDGE",EDGE,{"disambiguationData":[OSD([sQuery(id+"F52.wireOp",EDGE,"E173")])],"isStart":false});var subQ2=makeQuery(id+"F54.imprint","INTERSECT",VERTEX,{"disambiguationData":[OD(0.0)],"derivedFrom":[subQ1,subQ0]});Q10=makeQuery(id+"F54.imprint","IMPRINT",FACE,{"disambiguationData":[TD([[makeQuery(id+"F54.imprint","IMPRINT",EDGE,{"disambiguationData":[TD([[subQ2,1.0]])],"derivedFrom":subQ0}),1.0]])]});}
            var Q11;
            {var subQ0=sQuery(id+"F54.wireOp",EDGE,"E175.1.0");var subQ1=makeQuery(id+"F53.opExtrude","CAP_EDGE",EDGE,{"disambiguationData":[OSD([sQuery(id+"F52.wireOp",EDGE,"E173")])],"isStart":false});var subQ2=makeQuery(id+"F54.imprint","INTERSECT",VERTEX,{"disambiguationData":[OD(0.0)],"derivedFrom":[subQ1,subQ0]});Q11=makeQuery(id+"F54.imprint","IMPRINT",FACE,{"disambiguationData":[TD([[makeQuery(id+"F54.imprint","IMPRINT",EDGE,{"disambiguationData":[TD([[subQ2,1.0]])],"derivedFrom":subQ0}),1.0]])]});}
            extrude(context, id + "F55", {"entities" : qUnion([Q0, Q1, Q2, Q3, Q4, Q5, Q6, Q7, Q8, Q9, Q10, Q11]), "operationType" : NewBodyOperationType.REMOVE, "oppositeDirection" : true, "depth" : 3.8 * mm, "offsetDistance" : 25.4 * mm});
        }
        {
            var Q0;
            Q0=qCreatedBy(makeId("Top.planeOp"),FACE);
            var sketch = newSketch(context, id + "F56", { "sketchPlane" : qUnion([Q0])});
            skLineSegment(sketch, "E176.bottom", {"start": v(-29.2, 29.21) * mm, "end": v(29.21, 29.21) * mm});
            skLineSegment(sketch, "E176.top", {"start": v(-29.21, -29.21) * mm, "end": v(29.2, -29.21) * mm});
            skLineSegment(sketch, "E176.left", {"start": v(-29.2, 29.21) * mm, "end": v(-29.21, -29.21) * mm});
            skLineSegment(sketch, "E176.right", {"start": v(29.21, 29.21) * mm, "end": v(29.2, -29.21) * mm});
            skPoint(sketch, "E176.middle", {"position": v(0, 0) * mm});
            skLineSegment(sketch, "E177.bottom", {"start": v(-31.75, 7.62) * mm, "end": v(31.75, 7.62) * mm});
            skLineSegment(sketch, "E177.top", {"start": v(-31.75, -7.62) * mm, "end": v(31.75, -7.62) * mm});
            skLineSegment(sketch, "E177.left", {"start": v(-31.75, 7.62) * mm, "end": v(-31.75, -7.62) * mm});
            skLineSegment(sketch, "E177.right", {"start": v(31.75, 7.62) * mm, "end": v(31.75, -7.62) * mm});
            skLineSegment(sketch, "E178.bottom", {"start": v(-7.62, 31.75) * mm, "end": v(7.62, 31.75) * mm});
            skLineSegment(sketch, "E178.top", {"start": v(-7.62, -31.75) * mm, "end": v(7.62, -31.75) * mm});
            skLineSegment(sketch, "E178.left", {"start": v(-7.62, 31.75) * mm, "end": v(-7.62, -31.75) * mm});
            skLineSegment(sketch, "E178.right", {"start": v(7.62, 31.75) * mm, "end": v(7.62, -31.75) * mm});
            skLineSegment(sketch, "E179.bottom", {"start": v(-30.73, 30.73) * mm, "end": v(30.73, 30.73) * mm});
            skLineSegment(sketch, "E179.top", {"start": v(-30.73, -30.73) * mm, "end": v(30.73, -30.73) * mm});
            skLineSegment(sketch, "E179.left", {"start": v(-30.73, 30.73) * mm, "end": v(-30.73, -30.73) * mm});
            skLineSegment(sketch, "E179.right", {"start": v(30.73, 30.73) * mm, "end": v(30.73, -30.73) * mm});
            skLineSegment(sketch, "E180.bottom", {"start": v(-31.75, 31.75) * mm, "end": v(31.75, 31.75) * mm});
            skLineSegment(sketch, "E180.top", {"start": v(-31.75, -31.75) * mm, "end": v(31.75, -31.75) * mm});
            skLineSegment(sketch, "E180.left", {"start": v(-31.75, 31.75) * mm, "end": v(-31.75, -31.75) * mm});
            skLineSegment(sketch, "E180.right", {"start": v(31.75, 31.75) * mm, "end": v(31.75, -31.75) * mm});
            skLineSegment(sketch, "E181.bottom", {"start": v(-31.75, 2.54) * mm, "end": v(31.75, 2.54) * mm});
            skLineSegment(sketch, "E181.top", {"start": v(-31.75, -2.54) * mm, "end": v(31.75, -2.54) * mm});
            skLineSegment(sketch, "E181.left", {"start": v(-31.75, 2.54) * mm, "end": v(-31.75, -2.54) * mm});
            skLineSegment(sketch, "E181.right", {"start": v(31.75, 2.54) * mm, "end": v(31.75, -2.54) * mm});
            skLineSegment(sketch, "E182.bottom", {"start": v(-2.54, -31.75) * mm, "end": v(2.54, -31.75) * mm});
            skLineSegment(sketch, "E182.top", {"start": v(-2.54, 31.75) * mm, "end": v(2.54, 31.75) * mm});
            skLineSegment(sketch, "E182.left", {"start": v(-2.54, -31.75) * mm, "end": v(-2.54, 31.75) * mm});
            skLineSegment(sketch, "E182.right", {"start": v(2.54, -31.75) * mm, "end": v(2.54, 31.75) * mm});
            skSolve(sketch);
        }
        {
            var Q0;
            {var subQ0=sQuery(id+"F56.wireOp",EDGE,"E180.left");var subQ1=sQuery(id+"F56.wireOp",EDGE,"E177.bottom");var subQ2=makeQuery(id+"F56.imprint","INTERSECT",VERTEX,{"derivedFrom":[subQ1,subQ0]});Q0=makeQuery(id+"F56.imprint","IMPRINT",FACE,{"disambiguationData":[TD([[makeQuery(id+"F56.imprint","IMPRINT",EDGE,{"disambiguationData":[TD([[subQ2,-1.0]])],"derivedFrom":subQ1}),-1.0]])]});}
            var Q1;
            {var subQ0=sQuery(id+"F56.wireOp",EDGE,"E180.bottom");var subQ1=sQuery(id+"F56.wireOp",EDGE,"E178.left");var subQ2=makeQuery(id+"F56.imprint","INTERSECT",VERTEX,{"derivedFrom":[subQ1,subQ0]});Q1=makeQuery(id+"F56.imprint","IMPRINT",FACE,{"disambiguationData":[TD([[makeQuery(id+"F56.imprint","IMPRINT",EDGE,{"disambiguationData":[TD([[subQ2,-1.0]])],"derivedFrom":subQ1}),1.0]])]});}
            var Q2;
            {var subQ0=sQuery(id+"F56.wireOp",EDGE,"E180.right");var subQ1=sQuery(id+"F56.wireOp",EDGE,"E177.bottom");var subQ2=makeQuery(id+"F56.imprint","INTERSECT",VERTEX,{"derivedFrom":[subQ1,subQ0]});Q2=makeQuery(id+"F56.imprint","IMPRINT",FACE,{"disambiguationData":[TD([[makeQuery(id+"F56.imprint","IMPRINT",EDGE,{"disambiguationData":[TD([[subQ2,1.0]])],"derivedFrom":subQ1}),-1.0]])]});}
            var Q3;
            {var subQ0=sQuery(id+"F56.wireOp",EDGE,"E180.top");var subQ1=sQuery(id+"F56.wireOp",EDGE,"E178.left");var subQ2=makeQuery(id+"F56.imprint","INTERSECT",VERTEX,{"derivedFrom":[subQ1,subQ0]});Q3=makeQuery(id+"F56.imprint","IMPRINT",FACE,{"disambiguationData":[TD([[makeQuery(id+"F56.imprint","IMPRINT",EDGE,{"disambiguationData":[TD([[subQ2,1.0]])],"derivedFrom":subQ1}),1.0]])]});}
            var Q4;
            {var subQ0=sQuery(id+"F56.wireOp",EDGE,"E180.right");var subQ1=sQuery(id+"F56.wireOp",EDGE,"E177.top");var subQ2=makeQuery(id+"F56.imprint","INTERSECT",VERTEX,{"derivedFrom":[subQ1,subQ0]});Q4=makeQuery(id+"F56.imprint","IMPRINT",FACE,{"disambiguationData":[TD([[makeQuery(id+"F56.imprint","IMPRINT",EDGE,{"disambiguationData":[TD([[subQ2,1.0]])],"derivedFrom":subQ1}),1.0]])]});}
            var Q5;
            {var subQ0=sQuery(id+"F56.wireOp",EDGE,"E180.top");var subQ1=sQuery(id+"F56.wireOp",EDGE,"E178.right");var subQ2=makeQuery(id+"F56.imprint","INTERSECT",VERTEX,{"derivedFrom":[subQ1,subQ0]});Q5=makeQuery(id+"F56.imprint","IMPRINT",FACE,{"disambiguationData":[TD([[makeQuery(id+"F56.imprint","IMPRINT",EDGE,{"disambiguationData":[TD([[subQ2,1.0]])],"derivedFrom":subQ1}),-1.0]])]});}
            var Q6;
            {var subQ0=sQuery(id+"F56.wireOp",EDGE,"E180.left");var subQ1=sQuery(id+"F56.wireOp",EDGE,"E177.top");var subQ2=makeQuery(id+"F56.imprint","INTERSECT",VERTEX,{"derivedFrom":[subQ1,subQ0]});Q6=makeQuery(id+"F56.imprint","IMPRINT",FACE,{"disambiguationData":[TD([[makeQuery(id+"F56.imprint","IMPRINT",EDGE,{"disambiguationData":[TD([[subQ2,-1.0]])],"derivedFrom":subQ1}),1.0]])]});}
            var Q7;
            {var subQ0=sQuery(id+"F56.wireOp",EDGE,"E180.bottom");var subQ1=sQuery(id+"F56.wireOp",EDGE,"E178.right");var subQ2=makeQuery(id+"F56.imprint","INTERSECT",VERTEX,{"derivedFrom":[subQ1,subQ0]});Q7=makeQuery(id+"F56.imprint","IMPRINT",FACE,{"disambiguationData":[TD([[makeQuery(id+"F56.imprint","IMPRINT",EDGE,{"disambiguationData":[TD([[subQ2,-1.0]])],"derivedFrom":subQ1}),-1.0]])]});}
            extrude(context, id + "F57", {"entities" : qUnion([Q0, Q1, Q2, Q3, Q4, Q5, Q6, Q7]), "operationType" : NewBodyOperationType.REMOVE, "oppositeDirection" : true, "depth" : 12.7 * mm, "offsetDistance" : 25.4 * mm});
        }
        {
            var Q0;
            Q0=makeQuery(id+"F1.imprint","IMPRINT",FACE,{"disambiguationData":[TD([[makeQuery(id+"F1.imprint","IMPRINT",EDGE,{"derivedFrom":sQuery(id+"F1.wireOp",EDGE,"E0.bottom")}),-1.0]])]});
            var sketch = newSketch(context, id + "F58", { "sketchPlane" : qUnion([Q0])});
            skSolve(sketch);
        }
        {
            var Q0;
            Q0 = qSketchRegion(id + "F58", true);
            var Q1;
            {var subQ9=sQuery(id+"F14.wireOp",EDGE,"E74.left");var subQ10=sQuery(id+"F14.wireOp",EDGE,"E74.top");var subQ11=makeQuery(id+"F14.imprint","INTERSECT",VERTEX,{"derivedFrom":[subQ10,subQ9]});Q1=makeQuery(id+"F14.imprint","IMPRINT",FACE,{"disambiguationData":[TD([[makeQuery(id+"F14.imprint","IMPRINT",EDGE,{"disambiguationData":[TD([[subQ11,-1.0]])],"derivedFrom":subQ10}),-1.0]])]});}
            var Q2;
            {var subQ0=sQuery(id+"F14.wireOp",EDGE,"E74.right");var subQ1=sQuery(id+"F14.wireOp",EDGE,"E74.top");var subQ2=makeQuery(id+"F14.imprint","INTERSECT",VERTEX,{"derivedFrom":[subQ1,subQ0]});Q2=makeQuery(id+"F14.imprint","IMPRINT",FACE,{"disambiguationData":[TD([[makeQuery(id+"F14.imprint","IMPRINT",EDGE,{"disambiguationData":[TD([[subQ2,1.0]])],"derivedFrom":subQ1}),-1.0]])]});}
            var Q3;
            {var subQ9=sQuery(id+"F14.wireOp",EDGE,"E74.right");var subQ10=sQuery(id+"F14.wireOp",EDGE,"E74.bottom");var subQ11=makeQuery(id+"F14.imprint","INTERSECT",VERTEX,{"derivedFrom":[subQ10,subQ9]});Q3=makeQuery(id+"F14.imprint","IMPRINT",FACE,{"disambiguationData":[TD([[makeQuery(id+"F14.imprint","IMPRINT",EDGE,{"disambiguationData":[TD([[subQ11,1.0]])],"derivedFrom":subQ10}),1.0]])]});}
            var Q4;
            {var subQ9=sQuery(id+"F14.wireOp",EDGE,"E74.bottom");var subQ11=sQuery(id+"F14.wireOp",EDGE,"E74.left");var subQ12=makeQuery(id+"F14.imprint","INTERSECT",VERTEX,{"derivedFrom":[subQ9,subQ11]});Q4=makeQuery(id+"F14.imprint","IMPRINT",FACE,{"disambiguationData":[TD([[makeQuery(id+"F14.imprint","IMPRINT",EDGE,{"disambiguationData":[TD([[subQ12,-1.0]])],"derivedFrom":subQ9}),1.0]])]});}
            extrude(context, id + "F59", {"entities" : qUnion([Q0, Q1, Q2, Q3, Q4]), "operationType" : NewBodyOperationType.REMOVE, "oppositeDirection" : true, "depth" : 61.2 * mm, "offsetDistance" : 25.4 * mm, "hasSecondDirection" : true, "secondDirectionOppositeDirection" : true, "secondDirectionDepth" : 39.12 * mm});
        }
        {
            var Q0;
            Q0=makeQuery(id+"F58.imprint","IMPRINT",FACE,{"disambiguationData":[TD([[makeQuery(id+"F58.imprint","IMPRINT",EDGE,{"derivedFrom":makeQuery(id+"F1.imprint","IMPRINT",EDGE,{"derivedFrom":sQuery(id+"F1.wireOp",EDGE,"E0.bottom")})}),-1.0]])]});
            var sketch = newSketch(context, id + "F60", { "sketchPlane" : qUnion([Q0])});
            skCircle(sketch, "E183", {"center": v(0, 0) * mm, "radius": 18.92 * mm});
            skSolve(sketch);
        }
        {
            var Q0;
            Q0 = qSketchRegion(id + "F60", true);
            extrude(context, id + "F61", {"entities" : qUnion([Q0]), "operationType" : NewBodyOperationType.ADD, "oppositeDirection" : true, "depth" : 4.83 * mm, "offsetDistance" : 25.4 * mm});
        }
        {
            var Q0;
            Q0=makeQuery(id+"F59.boolean.opBoolean","COPY",FACE,{"derivedFrom":makeQuery(id+"F59.opExtrude","CAP_FACE",FACE,{"disambiguationData":[OSD([sQuery(id+"F14.wireOp",EDGE,"E74.top"),sQuery(id+"F14.wireOp",EDGE,"E74.left"),sQuery(id+"F14.wireOp",EDGE,"E75.top"),sQuery(id+"F14.wireOp",EDGE,"E76.left"),sQuery(id+"F14.wireOp",EDGE,"E79"),sQuery(id+"F14.wireOp",EDGE,"E80")])],"isStart":true})});
            var sketch = newSketch(context, id + "F62", { "sketchPlane" : qUnion([Q0])});
            skCircle(sketch, "E184", {"center": v(0, 0) * mm, "radius": 18.92 * mm});
            skCircle(sketch, "E185", {"center": v(0, 0) * mm, "radius": 27.94 * mm});
            skLineSegment(sketch, "E186", {"start": v(0, 0) * mm, "end": v(-18.52, 20.92) * mm});
            skLineSegment(sketch, "E187", {"start": v(0, 0) * mm, "end": v(-20.91, 18.53) * mm});
            skLineSegment(sketch, "E188.1.0", {"start": v(0, 0) * mm, "end": v(-18.53, -20.91) * mm});
            skLineSegment(sketch, "E188.1.1", {"start": v(0, 0) * mm, "end": v(-20.92, -18.52) * mm});
            skLineSegment(sketch, "E188.2.0", {"start": v(0, 0) * mm, "end": v(20.91, -18.53) * mm});
            skLineSegment(sketch, "E188.2.1", {"start": v(0, 0) * mm, "end": v(18.52, -20.92) * mm});
            skLineSegment(sketch, "E188.3.0", {"start": v(0, 0) * mm, "end": v(18.53, 20.91) * mm});
            skLineSegment(sketch, "E188.3.1", {"start": v(0, 0) * mm, "end": v(20.92, 18.52) * mm});
            skSolve(sketch);
        }
        {
            var Q0;
            {var subQ0=sQuery(id+"F62.wireOp",EDGE,"E185");var subQ1=sQuery(id+"F62.wireOp",EDGE,"E186");var subQ2=makeQuery(id+"F62.imprint","INTERSECT",VERTEX,{"derivedFrom":[subQ1,subQ0]});Q0=makeQuery(id+"F62.imprint","IMPRINT",FACE,{"disambiguationData":[TD([[makeQuery(id+"F62.imprint","IMPRINT",EDGE,{"disambiguationData":[TD([[subQ2,-1.0]])],"derivedFrom":subQ0}),1.0]])]});}
            var Q1;
            {var subQ0=sQuery(id+"F62.wireOp",EDGE,"E184");var subQ1=sQuery(id+"F62.wireOp",EDGE,"E186");var subQ2=makeQuery(id+"F62.imprint","INTERSECT",VERTEX,{"derivedFrom":[subQ1,subQ0]});Q1=makeQuery(id+"F62.imprint","IMPRINT",FACE,{"disambiguationData":[TD([[makeQuery(id+"F62.imprint","IMPRINT",EDGE,{"disambiguationData":[TD([[subQ2,-1.0]])],"derivedFrom":subQ0}),-1.0]])]});}
            var Q2;
            {var subQ0=sQuery(id+"F62.wireOp",EDGE,"E185");var subQ1=sQuery(id+"F62.wireOp",EDGE,"E188.3.0");var subQ2=makeQuery(id+"F62.imprint","INTERSECT",VERTEX,{"derivedFrom":[subQ1,subQ0]});Q2=makeQuery(id+"F62.imprint","IMPRINT",FACE,{"disambiguationData":[TD([[makeQuery(id+"F62.imprint","IMPRINT",EDGE,{"disambiguationData":[TD([[subQ2,1.0]])],"derivedFrom":subQ1}),-1.0]])]});}
            var Q3;
            {var subQ0=sQuery(id+"F62.wireOp",EDGE,"E185");var subQ1=sQuery(id+"F62.wireOp",EDGE,"E188.1.0");var subQ2=makeQuery(id+"F62.imprint","INTERSECT",VERTEX,{"derivedFrom":[subQ1,subQ0]});Q3=makeQuery(id+"F62.imprint","IMPRINT",FACE,{"disambiguationData":[TD([[makeQuery(id+"F62.imprint","IMPRINT",EDGE,{"disambiguationData":[TD([[subQ2,1.0]])],"derivedFrom":subQ1}),-1.0]])]});}
            var Q4;
            {var subQ0=sQuery(id+"F62.wireOp",EDGE,"E185");var subQ1=sQuery(id+"F62.wireOp",EDGE,"E188.2.0");var subQ2=makeQuery(id+"F62.imprint","INTERSECT",VERTEX,{"derivedFrom":[subQ1,subQ0]});Q4=makeQuery(id+"F62.imprint","IMPRINT",FACE,{"disambiguationData":[TD([[makeQuery(id+"F62.imprint","IMPRINT",EDGE,{"disambiguationData":[TD([[subQ2,1.0]])],"derivedFrom":subQ1}),-1.0]])]});}
            extrude(context, id + "F63", {"entities" : qUnion([Q0, Q1, Q2, Q3, Q4]), "depth" : 7.62 * mm, "offsetDistance" : 25.4 * mm});
        }
        {
            var Q0;
            {var subQ0=sQuery(id+"F62.wireOp",EDGE,"E185");Q0=makeQuery(id+"F63.opExtrude","CAP_EDGE",EDGE,{"disambiguationData":[OSD([subQ0]),TDD([makeQuery(id+"F62.imprint","IMPRINT",EDGE,{"disambiguationData":[TD([[makeQuery(id+"F62.imprint","INTERSECT",VERTEX,{"derivedFrom":[sQuery(id+"F62.wireOp",EDGE,"E188.2.0"),subQ0]}),1.0]])],"derivedFrom":subQ0})])],"isStart":false});}
            var Q1;
            {var subQ0=sQuery(id+"F62.wireOp",EDGE,"E185");Q1=makeQuery(id+"F63.opExtrude","CAP_EDGE",EDGE,{"disambiguationData":[OSD([subQ0]),TDD([makeQuery(id+"F62.imprint","IMPRINT",EDGE,{"disambiguationData":[TD([[makeQuery(id+"F62.imprint","INTERSECT",VERTEX,{"derivedFrom":[sQuery(id+"F62.wireOp",EDGE,"E188.1.0"),subQ0]}),1.0]])],"derivedFrom":subQ0})])],"isStart":false});}
            var Q2;
            {var subQ0=sQuery(id+"F62.wireOp",EDGE,"E185");Q2=makeQuery(id+"F63.opExtrude","CAP_EDGE",EDGE,{"disambiguationData":[OSD([subQ0]),TDD([makeQuery(id+"F62.imprint","IMPRINT",EDGE,{"disambiguationData":[TD([[makeQuery(id+"F62.imprint","INTERSECT",VERTEX,{"derivedFrom":[sQuery(id+"F62.wireOp",EDGE,"E188.3.0"),subQ0]}),1.0]])],"derivedFrom":subQ0})])],"isStart":false});}
            var Q3;
            {var subQ0=sQuery(id+"F62.wireOp",EDGE,"E185");Q3=makeQuery(id+"F63.opExtrude","CAP_EDGE",EDGE,{"disambiguationData":[OSD([subQ0]),TDD([makeQuery(id+"F62.imprint","IMPRINT",EDGE,{"disambiguationData":[TD([[makeQuery(id+"F62.imprint","INTERSECT",VERTEX,{"derivedFrom":[sQuery(id+"F62.wireOp",EDGE,"E186"),subQ0]}),-1.0]])],"derivedFrom":subQ0})])],"isStart":false});}
            chamfer(context, id + "F64", {"entities" : qUnion([Q0, Q1, Q2, Q3]), "chamferType" : ChamferType.OFFSET_ANGLE, "width" : 1.78 * mm, "oppositeDirection" : false, "angle" : 70 * degree, "tangentPropagation" : true});
        }
        {
            var Q0;
            {var subQ0=sQuery(id+"F62.wireOp",EDGE,"E185");var subQ1=sQuery(id+"F62.wireOp",EDGE,"E188.3.1");var subQ2=sQuery(id+"F62.wireOp",EDGE,"E188.3.0");Q0=makeQuery(id+"F64.opChamfer","BLEND_EDGE",EDGE,{"blendedFrom":[makeQuery(id+"F63.opExtrude","CAP_EDGE",EDGE,{"disambiguationData":[OSD([subQ0]),TDD([makeQuery(id+"F62.imprint","IMPRINT",EDGE,{"disambiguationData":[TD([[makeQuery(id+"F62.imprint","INTERSECT",VERTEX,{"derivedFrom":[subQ2,subQ0]}),1.0]])],"derivedFrom":subQ0})])],"isStart":false}),makeQuery(id+"F63.opExtrude","CAP_FACE",FACE,{"disambiguationData":[OSD([subQ2,subQ1,sQuery(id+"F62.wireOp",EDGE,"E184"),subQ0])],"isStart":false})],"blendedInto":[makeQuery(id+"F63.opExtrude","CAP_FACE",FACE,{"disambiguationData":[OSD([subQ2,subQ1,sQuery(id+"F62.wireOp",EDGE,"E184"),subQ0])],"isStart":false})]});}
            var Q1;
            {var subQ0=sQuery(id+"F62.wireOp",EDGE,"E185");var subQ1=sQuery(id+"F62.wireOp",EDGE,"E188.2.1");var subQ2=sQuery(id+"F62.wireOp",EDGE,"E188.2.0");Q1=makeQuery(id+"F64.opChamfer","BLEND_EDGE",EDGE,{"blendedFrom":[makeQuery(id+"F63.opExtrude","CAP_EDGE",EDGE,{"disambiguationData":[OSD([subQ0]),TDD([makeQuery(id+"F62.imprint","IMPRINT",EDGE,{"disambiguationData":[TD([[makeQuery(id+"F62.imprint","INTERSECT",VERTEX,{"derivedFrom":[subQ2,subQ0]}),1.0]])],"derivedFrom":subQ0})])],"isStart":false}),makeQuery(id+"F63.opExtrude","CAP_FACE",FACE,{"disambiguationData":[OSD([subQ2,subQ1,sQuery(id+"F62.wireOp",EDGE,"E184"),subQ0])],"isStart":false})],"blendedInto":[makeQuery(id+"F63.opExtrude","CAP_FACE",FACE,{"disambiguationData":[OSD([subQ2,subQ1,sQuery(id+"F62.wireOp",EDGE,"E184"),subQ0])],"isStart":false})]});}
            var Q2;
            {var subQ0=sQuery(id+"F62.wireOp",EDGE,"E184");Q2=makeQuery(id+"F63.opExtrude","CAP_EDGE",EDGE,{"disambiguationData":[OSD([subQ0]),TDD([makeQuery(id+"F62.imprint","IMPRINT",EDGE,{"disambiguationData":[TD([[makeQuery(id+"F62.imprint","INTERSECT",VERTEX,{"derivedFrom":[sQuery(id+"F62.wireOp",EDGE,"E188.3.0"),subQ0]}),1.0]])],"derivedFrom":subQ0})])],"isStart":false});}
            var Q3;
            {var subQ0=sQuery(id+"F62.wireOp",EDGE,"E184");Q3=makeQuery(id+"F63.opExtrude","CAP_EDGE",EDGE,{"disambiguationData":[OSD([subQ0]),TDD([makeQuery(id+"F62.imprint","IMPRINT",EDGE,{"disambiguationData":[TD([[makeQuery(id+"F62.imprint","INTERSECT",VERTEX,{"derivedFrom":[sQuery(id+"F62.wireOp",EDGE,"E188.2.0"),subQ0]}),1.0]])],"derivedFrom":subQ0})])],"isStart":false});}
            var Q4;
            {var subQ0=sQuery(id+"F62.wireOp",EDGE,"E184");Q4=makeQuery(id+"F63.opExtrude","CAP_EDGE",EDGE,{"disambiguationData":[OSD([subQ0]),TDD([makeQuery(id+"F62.imprint","IMPRINT",EDGE,{"disambiguationData":[TD([[makeQuery(id+"F62.imprint","INTERSECT",VERTEX,{"derivedFrom":[sQuery(id+"F62.wireOp",EDGE,"E186"),subQ0]}),-1.0]])],"derivedFrom":subQ0})])],"isStart":false});}
            var Q5;
            {var subQ0=sQuery(id+"F62.wireOp",EDGE,"E185");var subQ1=sQuery(id+"F62.wireOp",EDGE,"E187");var subQ2=sQuery(id+"F62.wireOp",EDGE,"E186");Q5=makeQuery(id+"F64.opChamfer","BLEND_EDGE",EDGE,{"blendedFrom":[makeQuery(id+"F63.opExtrude","CAP_EDGE",EDGE,{"disambiguationData":[OSD([subQ0]),TDD([makeQuery(id+"F62.imprint","IMPRINT",EDGE,{"disambiguationData":[TD([[makeQuery(id+"F62.imprint","INTERSECT",VERTEX,{"derivedFrom":[subQ2,subQ0]}),-1.0]])],"derivedFrom":subQ0})])],"isStart":false}),makeQuery(id+"F63.opExtrude","CAP_FACE",FACE,{"disambiguationData":[OSD([subQ2,subQ1,sQuery(id+"F62.wireOp",EDGE,"E184"),subQ0])],"isStart":false})],"blendedInto":[makeQuery(id+"F63.opExtrude","CAP_FACE",FACE,{"disambiguationData":[OSD([subQ2,subQ1,sQuery(id+"F62.wireOp",EDGE,"E184"),subQ0])],"isStart":false})]});}
            var Q6;
            {var subQ0=sQuery(id+"F62.wireOp",EDGE,"E185");var subQ1=sQuery(id+"F62.wireOp",EDGE,"E188.1.1");var subQ2=sQuery(id+"F62.wireOp",EDGE,"E188.1.0");Q6=makeQuery(id+"F64.opChamfer","BLEND_EDGE",EDGE,{"blendedFrom":[makeQuery(id+"F63.opExtrude","CAP_EDGE",EDGE,{"disambiguationData":[OSD([subQ0]),TDD([makeQuery(id+"F62.imprint","IMPRINT",EDGE,{"disambiguationData":[TD([[makeQuery(id+"F62.imprint","INTERSECT",VERTEX,{"derivedFrom":[subQ2,subQ0]}),1.0]])],"derivedFrom":subQ0})])],"isStart":false}),makeQuery(id+"F63.opExtrude","CAP_FACE",FACE,{"disambiguationData":[OSD([subQ2,subQ1,sQuery(id+"F62.wireOp",EDGE,"E184"),subQ0])],"isStart":false})],"blendedInto":[makeQuery(id+"F63.opExtrude","CAP_FACE",FACE,{"disambiguationData":[OSD([subQ2,subQ1,sQuery(id+"F62.wireOp",EDGE,"E184"),subQ0])],"isStart":false})]});}
            var Q7;
            {var subQ0=sQuery(id+"F62.wireOp",EDGE,"E184");Q7=makeQuery(id+"F63.opExtrude","CAP_EDGE",EDGE,{"disambiguationData":[OSD([subQ0]),TDD([makeQuery(id+"F62.imprint","IMPRINT",EDGE,{"disambiguationData":[TD([[makeQuery(id+"F62.imprint","INTERSECT",VERTEX,{"derivedFrom":[sQuery(id+"F62.wireOp",EDGE,"E188.1.0"),subQ0]}),1.0]])],"derivedFrom":subQ0})])],"isStart":false});}
            fillet(context, id + "F65", {"entities" : qUnion([Q0, Q1, Q2, Q3, Q4, Q5, Q6, Q7]), "radius" : 2.54 * mm, "tangentPropagation" : true, "allowEdgeOverflow" : false});
        }
        {
            var Q0;
            Q0=makeQuery(id+"F63.opExtrude","SWEPT_EDGE",EDGE,{"disambiguationData":[OSD([sQuery(id+"F62.wireOp",EDGE,"E188.2.1"),sQuery(id+"F62.wireOp",EDGE,"E185")])]});
            var Q1;
            Q1=makeQuery(id+"F63.opExtrude","CAP_EDGE",EDGE,{"disambiguationData":[OSD([sQuery(id+"F62.wireOp",EDGE,"E188.2.1")])],"isStart":false});
            var Q2;
            Q2=makeQuery(id+"F63.opExtrude","SWEPT_EDGE",EDGE,{"disambiguationData":[OSD([sQuery(id+"F62.wireOp",EDGE,"E188.2.0"),sQuery(id+"F62.wireOp",EDGE,"E185")])]});
            var Q3;
            Q3=makeQuery(id+"F63.opExtrude","CAP_EDGE",EDGE,{"disambiguationData":[OSD([sQuery(id+"F62.wireOp",EDGE,"E188.2.0")])],"isStart":false});
            var Q4;
            Q4=makeQuery(id+"F63.opExtrude","CAP_EDGE",EDGE,{"disambiguationData":[OSD([sQuery(id+"F62.wireOp",EDGE,"E188.1.0")])],"isStart":false});
            var Q5;
            Q5=makeQuery(id+"F63.opExtrude","CAP_EDGE",EDGE,{"disambiguationData":[OSD([sQuery(id+"F62.wireOp",EDGE,"E188.1.1")])],"isStart":false});
            var Q6;
            Q6=makeQuery(id+"F63.opExtrude","SWEPT_EDGE",EDGE,{"disambiguationData":[OSD([sQuery(id+"F62.wireOp",EDGE,"E188.1.0"),sQuery(id+"F62.wireOp",EDGE,"E185")])]});
            var Q7;
            Q7=makeQuery(id+"F63.opExtrude","SWEPT_EDGE",EDGE,{"disambiguationData":[OSD([sQuery(id+"F62.wireOp",EDGE,"E188.1.1"),sQuery(id+"F62.wireOp",EDGE,"E185")])]});
            var Q8;
            Q8=makeQuery(id+"F63.opExtrude","CAP_EDGE",EDGE,{"disambiguationData":[OSD([sQuery(id+"F62.wireOp",EDGE,"E187")])],"isStart":false});
            var Q9;
            Q9=makeQuery(id+"F63.opExtrude","CAP_EDGE",EDGE,{"disambiguationData":[OSD([sQuery(id+"F62.wireOp",EDGE,"E186")])],"isStart":false});
            var Q10;
            Q10=makeQuery(id+"F63.opExtrude","SWEPT_EDGE",EDGE,{"disambiguationData":[OSD([sQuery(id+"F62.wireOp",EDGE,"E187"),sQuery(id+"F62.wireOp",EDGE,"E185")])]});
            var Q11;
            Q11=makeQuery(id+"F63.opExtrude","SWEPT_EDGE",EDGE,{"disambiguationData":[OSD([sQuery(id+"F62.wireOp",EDGE,"E186"),sQuery(id+"F62.wireOp",EDGE,"E185")])]});
            var Q12;
            Q12=makeQuery(id+"F63.opExtrude","SWEPT_EDGE",EDGE,{"disambiguationData":[OSD([sQuery(id+"F62.wireOp",EDGE,"E188.3.0"),sQuery(id+"F62.wireOp",EDGE,"E185")])]});
            var Q13;
            Q13=makeQuery(id+"F63.opExtrude","CAP_EDGE",EDGE,{"disambiguationData":[OSD([sQuery(id+"F62.wireOp",EDGE,"E188.3.0")])],"isStart":false});
            var Q14;
            Q14=makeQuery(id+"F63.opExtrude","CAP_EDGE",EDGE,{"disambiguationData":[OSD([sQuery(id+"F62.wireOp",EDGE,"E188.3.1")])],"isStart":false});
            var Q15;
            Q15=makeQuery(id+"F63.opExtrude","SWEPT_EDGE",EDGE,{"disambiguationData":[OSD([sQuery(id+"F62.wireOp",EDGE,"E188.3.1"),sQuery(id+"F62.wireOp",EDGE,"E185")])]});
            var Q16;
            {var subQ0=sQuery(id+"F62.wireOp",EDGE,"E185");Q16=makeQuery(id+"F63.opExtrude","CAP_EDGE",EDGE,{"disambiguationData":[OSD([subQ0]),TDD([makeQuery(id+"F62.imprint","IMPRINT",EDGE,{"disambiguationData":[TD([[makeQuery(id+"F62.imprint","INTERSECT",VERTEX,{"derivedFrom":[sQuery(id+"F62.wireOp",EDGE,"E188.1.0"),subQ0]}),1.0]])],"derivedFrom":subQ0})])],"isStart":true});}
            var Q17;
            {var subQ0=sQuery(id+"F62.wireOp",EDGE,"E185");Q17=makeQuery(id+"F63.opExtrude","CAP_EDGE",EDGE,{"disambiguationData":[OSD([subQ0]),TDD([makeQuery(id+"F62.imprint","IMPRINT",EDGE,{"disambiguationData":[TD([[makeQuery(id+"F62.imprint","INTERSECT",VERTEX,{"derivedFrom":[sQuery(id+"F62.wireOp",EDGE,"E188.3.0"),subQ0]}),1.0]])],"derivedFrom":subQ0})])],"isStart":true});}
            var Q18;
            {var subQ0=sQuery(id+"F62.wireOp",EDGE,"E185");Q18=makeQuery(id+"F63.opExtrude","CAP_EDGE",EDGE,{"disambiguationData":[OSD([subQ0]),TDD([makeQuery(id+"F62.imprint","IMPRINT",EDGE,{"disambiguationData":[TD([[makeQuery(id+"F62.imprint","INTERSECT",VERTEX,{"derivedFrom":[sQuery(id+"F62.wireOp",EDGE,"E188.2.0"),subQ0]}),1.0]])],"derivedFrom":subQ0})])],"isStart":true});}
            var Q19;
            {var subQ0=sQuery(id+"F62.wireOp",EDGE,"E185");Q19=makeQuery(id+"F63.opExtrude","CAP_EDGE",EDGE,{"disambiguationData":[OSD([subQ0]),TDD([makeQuery(id+"F62.imprint","IMPRINT",EDGE,{"disambiguationData":[TD([[makeQuery(id+"F62.imprint","INTERSECT",VERTEX,{"derivedFrom":[sQuery(id+"F62.wireOp",EDGE,"E186"),subQ0]}),-1.0]])],"derivedFrom":subQ0})])],"isStart":true});}
            fillet(context, id + "F66", {"entities" : qUnion([Q0, Q1, Q2, Q3, Q4, Q5, Q6, Q7, Q8, Q9, Q10, Q11, Q12, Q13, Q14, Q15, Q16, Q17, Q18, Q19]), "radius" : 1.27 * mm, "tangentPropagation" : true, "allowEdgeOverflow" : false});
        }
        {
            var Q0;
            Q0=makeQuery(id+"F61.boolean.opBoolean","INTERSECT",EDGE,{"derivedFrom":[makeQuery(id+"F59.boolean.opBoolean","COPY",FACE,{"derivedFrom":makeQuery(id+"F59.opExtrude","SWEPT_FACE",FACE,{"disambiguationData":[OSD([sQuery(id+"F14.wireOp",EDGE,"E80")])]})}),makeQuery(id+"F61.opExtrude","SWEPT_FACE",FACE,{"disambiguationData":[OSD([sQuery(id+"F60.wireOp",EDGE,"E183")])]})]});
            var Q1;
            Q1=makeQuery(id+"F61.boolean.opBoolean","INTERSECT",EDGE,{"derivedFrom":[makeQuery(id+"F59.boolean.opBoolean","COPY",FACE,{"derivedFrom":makeQuery(id+"F59.opExtrude","SWEPT_FACE",FACE,{"disambiguationData":[OSD([sQuery(id+"F14.wireOp",EDGE,"E79")])]})}),makeQuery(id+"F61.opExtrude","SWEPT_FACE",FACE,{"disambiguationData":[OSD([sQuery(id+"F60.wireOp",EDGE,"E183")])]})]});
            var Q2;
            Q2=makeQuery(id+"F61.boolean.opBoolean","INTERSECT",EDGE,{"derivedFrom":[makeQuery(id+"F59.boolean.opBoolean","COPY",FACE,{"derivedFrom":makeQuery(id+"F59.opExtrude","SWEPT_FACE",FACE,{"disambiguationData":[OSD([sQuery(id+"F14.wireOp",EDGE,"E78")])]})}),makeQuery(id+"F61.opExtrude","SWEPT_FACE",FACE,{"disambiguationData":[OSD([sQuery(id+"F60.wireOp",EDGE,"E183")])]})]});
            var Q3;
            Q3=makeQuery(id+"F61.boolean.opBoolean","INTERSECT",EDGE,{"derivedFrom":[makeQuery(id+"F59.boolean.opBoolean","COPY",FACE,{"derivedFrom":makeQuery(id+"F59.opExtrude","SWEPT_FACE",FACE,{"disambiguationData":[OSD([sQuery(id+"F14.wireOp",EDGE,"E77")])]})}),makeQuery(id+"F61.opExtrude","SWEPT_FACE",FACE,{"disambiguationData":[OSD([sQuery(id+"F60.wireOp",EDGE,"E183")])]})]});
            var Q4;
            Q4=makeQuery(id+"F61.boolean.opBoolean","INTERSECT",EDGE,{"derivedFrom":[makeQuery(id+"F59.boolean.opBoolean","COPY",FACE,{"derivedFrom":makeQuery(id+"F59.opExtrude","SWEPT_FACE",FACE,{"disambiguationData":[OSD([sQuery(id+"F14.wireOp",EDGE,"E82")])]})}),makeQuery(id+"F61.opExtrude","SWEPT_FACE",FACE,{"disambiguationData":[OSD([sQuery(id+"F60.wireOp",EDGE,"E183")])]})]});
            var Q5;
            Q5=makeQuery(id+"F61.boolean.opBoolean","INTERSECT",EDGE,{"derivedFrom":[makeQuery(id+"F59.boolean.opBoolean","COPY",FACE,{"derivedFrom":makeQuery(id+"F59.opExtrude","SWEPT_FACE",FACE,{"disambiguationData":[OSD([sQuery(id+"F14.wireOp",EDGE,"E81")])]})}),makeQuery(id+"F61.opExtrude","SWEPT_FACE",FACE,{"disambiguationData":[OSD([sQuery(id+"F60.wireOp",EDGE,"E183")])]})]});
            var Q6;
            Q6=makeQuery(id+"F61.boolean.opBoolean","INTERSECT",EDGE,{"derivedFrom":[makeQuery(id+"F59.boolean.opBoolean","COPY",FACE,{"derivedFrom":makeQuery(id+"F59.opExtrude","SWEPT_FACE",FACE,{"disambiguationData":[OSD([sQuery(id+"F14.wireOp",EDGE,"E84")])]})}),makeQuery(id+"F61.opExtrude","SWEPT_FACE",FACE,{"disambiguationData":[OSD([sQuery(id+"F60.wireOp",EDGE,"E183")])]})]});
            var Q7;
            Q7=makeQuery(id+"F61.boolean.opBoolean","INTERSECT",EDGE,{"derivedFrom":[makeQuery(id+"F59.boolean.opBoolean","COPY",FACE,{"derivedFrom":makeQuery(id+"F59.opExtrude","SWEPT_FACE",FACE,{"disambiguationData":[OSD([sQuery(id+"F14.wireOp",EDGE,"E83")])]})}),makeQuery(id+"F61.opExtrude","SWEPT_FACE",FACE,{"disambiguationData":[OSD([sQuery(id+"F60.wireOp",EDGE,"E183")])]})]});
            fillet(context, id + "F67", {"entities" : qUnion([Q0, Q1, Q2, Q3, Q4, Q5, Q6, Q7]), "radius" : 0.89 * mm, "tangentPropagation" : true, "allowEdgeOverflow" : false});
        }
        {
            var Q0;
            {var subQ1=makeQuery(id+"F53.opExtrude","CAP_EDGE",EDGE,{"disambiguationData":[OSD([sQuery(id+"F52.wireOp",EDGE,"E173")])],"isStart":false});var subQ17=sQuery(id+"F54.wireOp",EDGE,"E174");var subQ32=makeQuery(id+"F54.imprint","INTERSECT",VERTEX,{"disambiguationData":[OD(0.0)],"derivedFrom":[subQ1,subQ17]});Q0=makeQuery(id+"F54.imprint","IMPRINT",FACE,{"disambiguationData":[TD([[makeQuery(id+"F54.imprint","IMPRINT",EDGE,{"disambiguationData":[TD([[subQ32,-1.0]])],"derivedFrom":subQ17}),-1.0]])]});}
            var sketch = newSketch(context, id + "F68", { "sketchPlane" : qUnion([Q0])});
            skCircle(sketch, "E189", {"center": v(0, 0) * mm, "radius": 13.97 * mm});
            skLineSegment(sketch, "E190", {"start": v(0, 13.97) * mm, "end": v(0, -13.97) * mm});
            skSolve(sketch);
        }
        {
            var Q0;
            {var subQ0=sQuery(id+"F68.wireOp",EDGE,"E190");Q0=makeQuery(id+"F68.imprint","IMPRINT",FACE,{"disambiguationData":[TD([[makeQuery(id+"F68.imprint","IMPRINT",EDGE,{"derivedFrom":subQ0}),1.0]])]});}
            var Q1;
            Q1=sQuery(id+"F68.wireOp",EDGE,"E190");
            revolve(context, id + "F69", {"surfaceOperationType" : NewSurfaceOperationType.NEW, "entities" : qUnion([Q0]), "axis" : qUnion([Q1]), "revolveType" : RevolveType.FULL});
        }
        {
            var Q0;
            {var subQ1=makeQuery(id+"F53.opExtrude","CAP_EDGE",EDGE,{"disambiguationData":[OSD([sQuery(id+"F52.wireOp",EDGE,"E173")])],"isStart":false});var subQ17=sQuery(id+"F54.wireOp",EDGE,"E174");var subQ32=makeQuery(id+"F54.imprint","INTERSECT",VERTEX,{"disambiguationData":[OD(0.0)],"derivedFrom":[subQ1,subQ17]});Q0=makeQuery(id+"F54.imprint","IMPRINT",FACE,{"disambiguationData":[TD([[makeQuery(id+"F54.imprint","IMPRINT",EDGE,{"disambiguationData":[TD([[subQ32,-1.0]])],"derivedFrom":subQ17}),-1.0]])]});}
            extrude(context, id + "F70", {"entities" : qUnion([Q0]), "operationType" : NewBodyOperationType.REMOVE, "oppositeDirection" : true, "depth" : 24.64 * mm, "offsetDistance" : 25.4 * mm});
        }
        {
            var Q0;
            {var subQ0=sQuery(id+"F2.wireOp",EDGE,"E1.left");var subQ1=sQuery(id+"F2.wireOp",EDGE,"E1.bottom");var subQ2=makeQuery(id+"F3.opExtrude","CAP_FACE",FACE,{"disambiguationData":[OSD([subQ1,sQuery(id+"F2.wireOp",EDGE,"E1.top"),subQ0,sQuery(id+"F2.wireOp",EDGE,"E1.right")])],"isStart":false});Q0=makeQuery(id+"F9.boolean.opBoolean","SPLIT",EDGE,{"disambiguationData":[TD([makeQuery(id+"F9.opExtrude","SWEPT_FACE",FACE,{"disambiguationData":[OSD([sQuery(id+"F8.wireOp",EDGE,"E35")])]})])],"derivedFrom":makeQuery(id+"F4.opChamfer","BLEND_EDGE",EDGE,{"blendedFrom":[makeQuery(id+"F3.opExtrude","CAP_EDGE",EDGE,{"disambiguationData":[OSD([subQ0])],"isStart":false}),subQ2],"blendedInto":[subQ2]})});}
            var Q1;
            {var subQ0=sQuery(id+"F2.wireOp",EDGE,"E1.left");var subQ1=sQuery(id+"F2.wireOp",EDGE,"E1.top");var subQ2=makeQuery(id+"F3.opExtrude","CAP_FACE",FACE,{"disambiguationData":[OSD([sQuery(id+"F2.wireOp",EDGE,"E1.bottom"),subQ1,subQ0,sQuery(id+"F2.wireOp",EDGE,"E1.right")])],"isStart":false});Q1=makeQuery(id+"F11.boolean.opBoolean","SPLIT",EDGE,{"disambiguationData":[TD([makeQuery(id+"F11.opExtrude","SWEPT_FACE",FACE,{"disambiguationData":[OSD([sQuery(id+"F10.wireOp",EDGE,"E53")])]})])],"derivedFrom":makeQuery(id+"F4.opChamfer","BLEND_EDGE",EDGE,{"blendedFrom":[makeQuery(id+"F3.opExtrude","CAP_EDGE",EDGE,{"disambiguationData":[OSD([subQ1])],"isStart":false}),subQ2],"blendedInto":[subQ2]})});}
            var Q2;
            {var subQ0=sQuery(id+"F2.wireOp",EDGE,"E1.right");var subQ1=sQuery(id+"F2.wireOp",EDGE,"E1.top");var subQ2=makeQuery(id+"F3.opExtrude","CAP_FACE",FACE,{"disambiguationData":[OSD([sQuery(id+"F2.wireOp",EDGE,"E1.bottom"),subQ1,sQuery(id+"F2.wireOp",EDGE,"E1.left"),subQ0])],"isStart":false});Q2=makeQuery(id+"F13.boolean.opBoolean","SPLIT",EDGE,{"disambiguationData":[TD([makeQuery(id+"F13.opExtrude","SWEPT_FACE",FACE,{"disambiguationData":[OSD([sQuery(id+"F12.wireOp",EDGE,"E71")])]})])],"derivedFrom":makeQuery(id+"F4.opChamfer","BLEND_EDGE",EDGE,{"blendedFrom":[makeQuery(id+"F3.opExtrude","CAP_EDGE",EDGE,{"disambiguationData":[OSD([subQ0])],"isStart":false}),subQ2],"blendedInto":[subQ2]})});}
            var Q3;
            {var subQ0=sQuery(id+"F2.wireOp",EDGE,"E1.right");var subQ1=sQuery(id+"F2.wireOp",EDGE,"E1.bottom");var subQ2=makeQuery(id+"F3.opExtrude","CAP_FACE",FACE,{"disambiguationData":[OSD([subQ1,sQuery(id+"F2.wireOp",EDGE,"E1.top"),sQuery(id+"F2.wireOp",EDGE,"E1.left"),subQ0])],"isStart":false});Q3=makeQuery(id+"F7.boolean.opBoolean","SPLIT",EDGE,{"disambiguationData":[TD([makeQuery(id+"F7.opExtrude","SWEPT_FACE",FACE,{"disambiguationData":[OSD([sQuery(id+"F6.wireOp",EDGE,"E17")])]})])],"derivedFrom":makeQuery(id+"F4.opChamfer","BLEND_EDGE",EDGE,{"blendedFrom":[makeQuery(id+"F3.opExtrude","CAP_EDGE",EDGE,{"disambiguationData":[OSD([subQ1])],"isStart":false}),subQ2],"blendedInto":[subQ2]})});}
            fillet(context, id + "F71", {"entities" : qUnion([Q0, Q1, Q2, Q3]), "radius" : 5.08 * mm, "tangentPropagation" : true, "allowEdgeOverflow" : false});
        }
        {
            var Q0;
            Q0=makeQuery(id+"F24.boolean.opBoolean","INTERSECT",EDGE,{"derivedFrom":[makeQuery(id+"F16.opExtrude","CAP_FACE",FACE,{"disambiguationData":[OSD([sQuery(id+"F15.wireOp",EDGE,"E85.bottom"),sQuery(id+"F15.wireOp",EDGE,"E85.top"),sQuery(id+"F15.wireOp",EDGE,"E85.left"),sQuery(id+"F15.wireOp",EDGE,"E85.right")])],"isStart":true}),makeQuery(id+"F24.opExtrude","SWEPT_FACE",FACE,{"disambiguationData":[OSD([sQuery(id+"F23.wireOp",EDGE,"E120.left")])]})]});
            var Q1;
            Q1=makeQuery(id+"F24.boolean.opBoolean","INTERSECT",EDGE,{"derivedFrom":[makeQuery(id+"F16.opExtrude","CAP_FACE",FACE,{"disambiguationData":[OSD([sQuery(id+"F15.wireOp",EDGE,"E85.bottom"),sQuery(id+"F15.wireOp",EDGE,"E85.top"),sQuery(id+"F15.wireOp",EDGE,"E85.left"),sQuery(id+"F15.wireOp",EDGE,"E85.right")])],"isStart":true}),makeQuery(id+"F24.opExtrude","SWEPT_FACE",FACE,{"disambiguationData":[OSD([sQuery(id+"F23.wireOp",EDGE,"E120.top")])]})]});
            var Q2;
            Q2=makeQuery(id+"F24.boolean.opBoolean","INTERSECT",EDGE,{"derivedFrom":[makeQuery(id+"F16.opExtrude","CAP_FACE",FACE,{"disambiguationData":[OSD([sQuery(id+"F15.wireOp",EDGE,"E85.bottom"),sQuery(id+"F15.wireOp",EDGE,"E85.top"),sQuery(id+"F15.wireOp",EDGE,"E85.left"),sQuery(id+"F15.wireOp",EDGE,"E85.right")])],"isStart":true}),makeQuery(id+"F24.opExtrude","SWEPT_FACE",FACE,{"disambiguationData":[OSD([sQuery(id+"F23.wireOp",EDGE,"E120.right")])]})]});
            var Q3;
            Q3=makeQuery(id+"F24.boolean.opBoolean","INTERSECT",EDGE,{"derivedFrom":[makeQuery(id+"F16.opExtrude","CAP_FACE",FACE,{"disambiguationData":[OSD([sQuery(id+"F15.wireOp",EDGE,"E85.bottom"),sQuery(id+"F15.wireOp",EDGE,"E85.top"),sQuery(id+"F15.wireOp",EDGE,"E85.left"),sQuery(id+"F15.wireOp",EDGE,"E85.right")])],"isStart":true}),makeQuery(id+"F24.opExtrude","SWEPT_FACE",FACE,{"disambiguationData":[OSD([sQuery(id+"F23.wireOp",EDGE,"E120.bottom")])]})]});
            var Q4;
            {var subQ0=sQuery(id+"F2.wireOp",EDGE,"E1.right");Q4=makeQuery(id+"F5.opChamfer","BLEND_EDGE",EDGE,{"blendedFrom":[makeQuery(id+"F4.opChamfer","BLEND_EDGE",EDGE,{"blendedFrom":[makeQuery(id+"F3.opExtrude","CAP_EDGE",EDGE,{"disambiguationData":[OSD([sQuery(id+"F2.wireOp",EDGE,"E1.top")])],"isStart":false}),makeQuery(id+"F3.opExtrude","CAP_EDGE",EDGE,{"disambiguationData":[OSD([subQ0])],"isStart":false})],"blendedInto":[]}),makeQuery(id+"F4.opChamfer","BLEND_FACE",FACE,{"disambiguationData":[OSD([subQ0])]})],"blendedInto":[makeQuery(id+"F4.opChamfer","BLEND_FACE",FACE,{"disambiguationData":[OSD([subQ0])]})]});}
            var Q5;
            {var subQ0=sQuery(id+"F2.wireOp",EDGE,"E1.right");Q5=makeQuery(id+"F5.opChamfer","BLEND_EDGE",EDGE,{"blendedFrom":[makeQuery(id+"F4.opChamfer","BLEND_EDGE",EDGE,{"blendedFrom":[makeQuery(id+"F3.opExtrude","CAP_EDGE",EDGE,{"disambiguationData":[OSD([sQuery(id+"F2.wireOp",EDGE,"E1.bottom")])],"isStart":false}),makeQuery(id+"F3.opExtrude","CAP_EDGE",EDGE,{"disambiguationData":[OSD([subQ0])],"isStart":false})],"blendedInto":[]}),makeQuery(id+"F4.opChamfer","BLEND_FACE",FACE,{"disambiguationData":[OSD([subQ0])]})],"blendedInto":[makeQuery(id+"F4.opChamfer","BLEND_FACE",FACE,{"disambiguationData":[OSD([subQ0])]})]});}
            var Q6;
            {var subQ0=sQuery(id+"F2.wireOp",EDGE,"E1.bottom");Q6=makeQuery(id+"F5.opChamfer","BLEND_EDGE",EDGE,{"blendedFrom":[makeQuery(id+"F4.opChamfer","BLEND_EDGE",EDGE,{"blendedFrom":[makeQuery(id+"F3.opExtrude","CAP_EDGE",EDGE,{"disambiguationData":[OSD([subQ0])],"isStart":false}),makeQuery(id+"F3.opExtrude","CAP_EDGE",EDGE,{"disambiguationData":[OSD([sQuery(id+"F2.wireOp",EDGE,"E1.right")])],"isStart":false})],"blendedInto":[]}),makeQuery(id+"F4.opChamfer","BLEND_FACE",FACE,{"disambiguationData":[OSD([subQ0])]})],"blendedInto":[makeQuery(id+"F4.opChamfer","BLEND_FACE",FACE,{"disambiguationData":[OSD([subQ0])]})]});}
            var Q7;
            {var subQ0=sQuery(id+"F2.wireOp",EDGE,"E1.bottom");Q7=makeQuery(id+"F5.opChamfer","BLEND_EDGE",EDGE,{"blendedFrom":[makeQuery(id+"F4.opChamfer","BLEND_EDGE",EDGE,{"blendedFrom":[makeQuery(id+"F3.opExtrude","CAP_EDGE",EDGE,{"disambiguationData":[OSD([subQ0])],"isStart":false}),makeQuery(id+"F3.opExtrude","CAP_EDGE",EDGE,{"disambiguationData":[OSD([sQuery(id+"F2.wireOp",EDGE,"E1.left")])],"isStart":false})],"blendedInto":[]}),makeQuery(id+"F4.opChamfer","BLEND_FACE",FACE,{"disambiguationData":[OSD([subQ0])]})],"blendedInto":[makeQuery(id+"F4.opChamfer","BLEND_FACE",FACE,{"disambiguationData":[OSD([subQ0])]})]});}
            var Q8;
            {var subQ0=sQuery(id+"F2.wireOp",EDGE,"E1.left");Q8=makeQuery(id+"F5.opChamfer","BLEND_EDGE",EDGE,{"blendedFrom":[makeQuery(id+"F4.opChamfer","BLEND_EDGE",EDGE,{"blendedFrom":[makeQuery(id+"F3.opExtrude","CAP_EDGE",EDGE,{"disambiguationData":[OSD([sQuery(id+"F2.wireOp",EDGE,"E1.bottom")])],"isStart":false}),makeQuery(id+"F3.opExtrude","CAP_EDGE",EDGE,{"disambiguationData":[OSD([subQ0])],"isStart":false})],"blendedInto":[]}),makeQuery(id+"F4.opChamfer","BLEND_FACE",FACE,{"disambiguationData":[OSD([subQ0])]})],"blendedInto":[makeQuery(id+"F4.opChamfer","BLEND_FACE",FACE,{"disambiguationData":[OSD([subQ0])]})]});}
            var Q9;
            {var subQ0=sQuery(id+"F2.wireOp",EDGE,"E1.left");Q9=makeQuery(id+"F5.opChamfer","BLEND_EDGE",EDGE,{"blendedFrom":[makeQuery(id+"F4.opChamfer","BLEND_EDGE",EDGE,{"blendedFrom":[makeQuery(id+"F3.opExtrude","CAP_EDGE",EDGE,{"disambiguationData":[OSD([sQuery(id+"F2.wireOp",EDGE,"E1.top")])],"isStart":false}),makeQuery(id+"F3.opExtrude","CAP_EDGE",EDGE,{"disambiguationData":[OSD([subQ0])],"isStart":false})],"blendedInto":[]}),makeQuery(id+"F4.opChamfer","BLEND_FACE",FACE,{"disambiguationData":[OSD([subQ0])]})],"blendedInto":[makeQuery(id+"F4.opChamfer","BLEND_FACE",FACE,{"disambiguationData":[OSD([subQ0])]})]});}
            var Q10;
            {var subQ0=sQuery(id+"F2.wireOp",EDGE,"E1.top");Q10=makeQuery(id+"F5.opChamfer","BLEND_EDGE",EDGE,{"blendedFrom":[makeQuery(id+"F4.opChamfer","BLEND_EDGE",EDGE,{"blendedFrom":[makeQuery(id+"F3.opExtrude","CAP_EDGE",EDGE,{"disambiguationData":[OSD([subQ0])],"isStart":false}),makeQuery(id+"F3.opExtrude","CAP_EDGE",EDGE,{"disambiguationData":[OSD([sQuery(id+"F2.wireOp",EDGE,"E1.left")])],"isStart":false})],"blendedInto":[]}),makeQuery(id+"F4.opChamfer","BLEND_FACE",FACE,{"disambiguationData":[OSD([subQ0])]})],"blendedInto":[makeQuery(id+"F4.opChamfer","BLEND_FACE",FACE,{"disambiguationData":[OSD([subQ0])]})]});}
            var Q11;
            {var subQ0=sQuery(id+"F2.wireOp",EDGE,"E1.top");Q11=makeQuery(id+"F5.opChamfer","BLEND_EDGE",EDGE,{"blendedFrom":[makeQuery(id+"F4.opChamfer","BLEND_EDGE",EDGE,{"blendedFrom":[makeQuery(id+"F3.opExtrude","CAP_EDGE",EDGE,{"disambiguationData":[OSD([subQ0])],"isStart":false}),makeQuery(id+"F3.opExtrude","CAP_EDGE",EDGE,{"disambiguationData":[OSD([sQuery(id+"F2.wireOp",EDGE,"E1.right")])],"isStart":false})],"blendedInto":[]}),makeQuery(id+"F4.opChamfer","BLEND_FACE",FACE,{"disambiguationData":[OSD([subQ0])]})],"blendedInto":[makeQuery(id+"F4.opChamfer","BLEND_FACE",FACE,{"disambiguationData":[OSD([subQ0])]})]});}
            var Q12;
            {var subQ0=sQuery(id+"F2.wireOp",EDGE,"E1.top");Q12=makeQuery(id+"F5.opChamfer","BLEND_EDGE",EDGE,{"blendedFrom":[makeQuery(id+"F4.opChamfer","BLEND_EDGE",EDGE,{"blendedFrom":[makeQuery(id+"F3.opExtrude","CAP_EDGE",EDGE,{"disambiguationData":[OSD([subQ0])],"isStart":false}),makeQuery(id+"F3.opExtrude","CAP_EDGE",EDGE,{"disambiguationData":[OSD([sQuery(id+"F2.wireOp",EDGE,"E1.right")])],"isStart":false})],"blendedInto":[]}),makeQuery(id+"F3.opExtrude","SWEPT_FACE",FACE,{"disambiguationData":[OSD([subQ0])]})],"blendedInto":[makeQuery(id+"F3.opExtrude","SWEPT_FACE",FACE,{"disambiguationData":[OSD([subQ0])]})]});}
            var Q13;
            {var subQ0=sQuery(id+"F2.wireOp",EDGE,"E1.right");Q13=makeQuery(id+"F5.opChamfer","BLEND_EDGE",EDGE,{"blendedFrom":[makeQuery(id+"F4.opChamfer","BLEND_EDGE",EDGE,{"blendedFrom":[makeQuery(id+"F3.opExtrude","CAP_EDGE",EDGE,{"disambiguationData":[OSD([sQuery(id+"F2.wireOp",EDGE,"E1.top")])],"isStart":false}),makeQuery(id+"F3.opExtrude","CAP_EDGE",EDGE,{"disambiguationData":[OSD([subQ0])],"isStart":false})],"blendedInto":[]}),makeQuery(id+"F3.opExtrude","SWEPT_FACE",FACE,{"disambiguationData":[OSD([subQ0])]})],"blendedInto":[makeQuery(id+"F3.opExtrude","SWEPT_FACE",FACE,{"disambiguationData":[OSD([subQ0])]})]});}
            var Q14;
            {var subQ0=sQuery(id+"F2.wireOp",EDGE,"E1.right");Q14=makeQuery(id+"F5.opChamfer","BLEND_EDGE",EDGE,{"blendedFrom":[makeQuery(id+"F4.opChamfer","BLEND_EDGE",EDGE,{"blendedFrom":[makeQuery(id+"F3.opExtrude","CAP_EDGE",EDGE,{"disambiguationData":[OSD([sQuery(id+"F2.wireOp",EDGE,"E1.bottom")])],"isStart":false}),makeQuery(id+"F3.opExtrude","CAP_EDGE",EDGE,{"disambiguationData":[OSD([subQ0])],"isStart":false})],"blendedInto":[]}),makeQuery(id+"F3.opExtrude","SWEPT_FACE",FACE,{"disambiguationData":[OSD([subQ0])]})],"blendedInto":[makeQuery(id+"F3.opExtrude","SWEPT_FACE",FACE,{"disambiguationData":[OSD([subQ0])]})]});}
            var Q15;
            {var subQ0=sQuery(id+"F2.wireOp",EDGE,"E1.bottom");Q15=makeQuery(id+"F5.opChamfer","BLEND_EDGE",EDGE,{"blendedFrom":[makeQuery(id+"F4.opChamfer","BLEND_EDGE",EDGE,{"blendedFrom":[makeQuery(id+"F3.opExtrude","CAP_EDGE",EDGE,{"disambiguationData":[OSD([subQ0])],"isStart":false}),makeQuery(id+"F3.opExtrude","CAP_EDGE",EDGE,{"disambiguationData":[OSD([sQuery(id+"F2.wireOp",EDGE,"E1.right")])],"isStart":false})],"blendedInto":[]}),makeQuery(id+"F3.opExtrude","SWEPT_FACE",FACE,{"disambiguationData":[OSD([subQ0])]})],"blendedInto":[makeQuery(id+"F3.opExtrude","SWEPT_FACE",FACE,{"disambiguationData":[OSD([subQ0])]})]});}
            var Q16;
            {var subQ0=sQuery(id+"F2.wireOp",EDGE,"E1.bottom");Q16=makeQuery(id+"F5.opChamfer","BLEND_EDGE",EDGE,{"blendedFrom":[makeQuery(id+"F4.opChamfer","BLEND_EDGE",EDGE,{"blendedFrom":[makeQuery(id+"F3.opExtrude","CAP_EDGE",EDGE,{"disambiguationData":[OSD([subQ0])],"isStart":false}),makeQuery(id+"F3.opExtrude","CAP_EDGE",EDGE,{"disambiguationData":[OSD([sQuery(id+"F2.wireOp",EDGE,"E1.left")])],"isStart":false})],"blendedInto":[]}),makeQuery(id+"F3.opExtrude","SWEPT_FACE",FACE,{"disambiguationData":[OSD([subQ0])]})],"blendedInto":[makeQuery(id+"F3.opExtrude","SWEPT_FACE",FACE,{"disambiguationData":[OSD([subQ0])]})]});}
            var Q17;
            {var subQ0=sQuery(id+"F2.wireOp",EDGE,"E1.left");Q17=makeQuery(id+"F5.opChamfer","BLEND_EDGE",EDGE,{"blendedFrom":[makeQuery(id+"F4.opChamfer","BLEND_EDGE",EDGE,{"blendedFrom":[makeQuery(id+"F3.opExtrude","CAP_EDGE",EDGE,{"disambiguationData":[OSD([sQuery(id+"F2.wireOp",EDGE,"E1.bottom")])],"isStart":false}),makeQuery(id+"F3.opExtrude","CAP_EDGE",EDGE,{"disambiguationData":[OSD([subQ0])],"isStart":false})],"blendedInto":[]}),makeQuery(id+"F3.opExtrude","SWEPT_FACE",FACE,{"disambiguationData":[OSD([subQ0])]})],"blendedInto":[makeQuery(id+"F3.opExtrude","SWEPT_FACE",FACE,{"disambiguationData":[OSD([subQ0])]})]});}
            var Q18;
            {var subQ0=sQuery(id+"F2.wireOp",EDGE,"E1.left");Q18=makeQuery(id+"F5.opChamfer","BLEND_EDGE",EDGE,{"blendedFrom":[makeQuery(id+"F4.opChamfer","BLEND_EDGE",EDGE,{"blendedFrom":[makeQuery(id+"F3.opExtrude","CAP_EDGE",EDGE,{"disambiguationData":[OSD([sQuery(id+"F2.wireOp",EDGE,"E1.top")])],"isStart":false}),makeQuery(id+"F3.opExtrude","CAP_EDGE",EDGE,{"disambiguationData":[OSD([subQ0])],"isStart":false})],"blendedInto":[]}),makeQuery(id+"F3.opExtrude","SWEPT_FACE",FACE,{"disambiguationData":[OSD([subQ0])]})],"blendedInto":[makeQuery(id+"F3.opExtrude","SWEPT_FACE",FACE,{"disambiguationData":[OSD([subQ0])]})]});}
            var Q19;
            {var subQ0=sQuery(id+"F2.wireOp",EDGE,"E1.top");Q19=makeQuery(id+"F5.opChamfer","BLEND_EDGE",EDGE,{"blendedFrom":[makeQuery(id+"F4.opChamfer","BLEND_EDGE",EDGE,{"blendedFrom":[makeQuery(id+"F3.opExtrude","CAP_EDGE",EDGE,{"disambiguationData":[OSD([subQ0])],"isStart":false}),makeQuery(id+"F3.opExtrude","CAP_EDGE",EDGE,{"disambiguationData":[OSD([sQuery(id+"F2.wireOp",EDGE,"E1.left")])],"isStart":false})],"blendedInto":[]}),makeQuery(id+"F3.opExtrude","SWEPT_FACE",FACE,{"disambiguationData":[OSD([subQ0])]})],"blendedInto":[makeQuery(id+"F3.opExtrude","SWEPT_FACE",FACE,{"disambiguationData":[OSD([subQ0])]})]});}
            fillet(context, id + "F72", {"entities" : qUnion([Q0, Q1, Q2, Q3, Q4, Q5, Q6, Q7, Q8, Q9, Q10, Q11, Q12, Q13, Q14, Q15, Q16, Q17, Q18, Q19]), "radius" : 2.54 * mm, "tangentPropagation" : true, "allowEdgeOverflow" : false});
        }
        {
            var Q0;
            Q0=makeQuery(id+"F25.opChamfer","BLEND_EDGE",EDGE,{"blendedFrom":[makeQuery(id+"F24.boolean.opBoolean","COPY",EDGE,{"derivedFrom":makeQuery(id+"F24.opExtrude","SWEPT_EDGE",EDGE,{"disambiguationData":[OSD([sQuery(id+"F23.wireOp",EDGE,"E120.bottom"),sQuery(id+"F23.wireOp",EDGE,"E120.left")])]})}),makeQuery(id+"F16.opExtrude","CAP_FACE",FACE,{"disambiguationData":[OSD([sQuery(id+"F15.wireOp",EDGE,"E85.bottom"),sQuery(id+"F15.wireOp",EDGE,"E85.top"),sQuery(id+"F15.wireOp",EDGE,"E85.left"),sQuery(id+"F15.wireOp",EDGE,"E85.right")])],"isStart":false})],"blendedInto":[makeQuery(id+"F16.opExtrude","CAP_FACE",FACE,{"disambiguationData":[OSD([sQuery(id+"F15.wireOp",EDGE,"E85.bottom"),sQuery(id+"F15.wireOp",EDGE,"E85.top"),sQuery(id+"F15.wireOp",EDGE,"E85.left"),sQuery(id+"F15.wireOp",EDGE,"E85.right")])],"isStart":false})]});
            var Q1;
            Q1=makeQuery(id+"F25.opChamfer","BLEND_EDGE",EDGE,{"blendedFrom":[makeQuery(id+"F24.boolean.opBoolean","COPY",EDGE,{"derivedFrom":makeQuery(id+"F24.opExtrude","SWEPT_EDGE",EDGE,{"disambiguationData":[OSD([sQuery(id+"F23.wireOp",EDGE,"E120.bottom"),sQuery(id+"F23.wireOp",EDGE,"E120.right")])]})}),makeQuery(id+"F16.opExtrude","CAP_FACE",FACE,{"disambiguationData":[OSD([sQuery(id+"F15.wireOp",EDGE,"E85.bottom"),sQuery(id+"F15.wireOp",EDGE,"E85.top"),sQuery(id+"F15.wireOp",EDGE,"E85.left"),sQuery(id+"F15.wireOp",EDGE,"E85.right")])],"isStart":false})],"blendedInto":[makeQuery(id+"F16.opExtrude","CAP_FACE",FACE,{"disambiguationData":[OSD([sQuery(id+"F15.wireOp",EDGE,"E85.bottom"),sQuery(id+"F15.wireOp",EDGE,"E85.top"),sQuery(id+"F15.wireOp",EDGE,"E85.left"),sQuery(id+"F15.wireOp",EDGE,"E85.right")])],"isStart":false})]});
            var Q2;
            Q2=makeQuery(id+"F25.opChamfer","BLEND_EDGE",EDGE,{"blendedFrom":[makeQuery(id+"F24.boolean.opBoolean","COPY",EDGE,{"derivedFrom":makeQuery(id+"F24.opExtrude","SWEPT_EDGE",EDGE,{"disambiguationData":[OSD([sQuery(id+"F23.wireOp",EDGE,"E120.top"),sQuery(id+"F23.wireOp",EDGE,"E120.right")])]})}),makeQuery(id+"F16.opExtrude","CAP_FACE",FACE,{"disambiguationData":[OSD([sQuery(id+"F15.wireOp",EDGE,"E85.bottom"),sQuery(id+"F15.wireOp",EDGE,"E85.top"),sQuery(id+"F15.wireOp",EDGE,"E85.left"),sQuery(id+"F15.wireOp",EDGE,"E85.right")])],"isStart":false})],"blendedInto":[makeQuery(id+"F16.opExtrude","CAP_FACE",FACE,{"disambiguationData":[OSD([sQuery(id+"F15.wireOp",EDGE,"E85.bottom"),sQuery(id+"F15.wireOp",EDGE,"E85.top"),sQuery(id+"F15.wireOp",EDGE,"E85.left"),sQuery(id+"F15.wireOp",EDGE,"E85.right")])],"isStart":false})]});
            var Q3;
            Q3=makeQuery(id+"F25.opChamfer","BLEND_EDGE",EDGE,{"blendedFrom":[makeQuery(id+"F24.boolean.opBoolean","COPY",EDGE,{"derivedFrom":makeQuery(id+"F24.opExtrude","SWEPT_EDGE",EDGE,{"disambiguationData":[OSD([sQuery(id+"F23.wireOp",EDGE,"E120.top"),sQuery(id+"F23.wireOp",EDGE,"E120.left")])]})}),makeQuery(id+"F16.opExtrude","CAP_FACE",FACE,{"disambiguationData":[OSD([sQuery(id+"F15.wireOp",EDGE,"E85.bottom"),sQuery(id+"F15.wireOp",EDGE,"E85.top"),sQuery(id+"F15.wireOp",EDGE,"E85.left"),sQuery(id+"F15.wireOp",EDGE,"E85.right")])],"isStart":false})],"blendedInto":[makeQuery(id+"F16.opExtrude","CAP_FACE",FACE,{"disambiguationData":[OSD([sQuery(id+"F15.wireOp",EDGE,"E85.bottom"),sQuery(id+"F15.wireOp",EDGE,"E85.top"),sQuery(id+"F15.wireOp",EDGE,"E85.left"),sQuery(id+"F15.wireOp",EDGE,"E85.right")])],"isStart":false})]});
            fillet(context, id + "F73", {"entities" : qUnion([Q0, Q1, Q2, Q3]), "radius" : 2.92 * mm, "tangentPropagation" : true, "allowEdgeOverflow" : false});
        }
        {
            var Q0;
            Q0=makeQuery(id+"F9.boolean.opBoolean","COPY",EDGE,{"derivedFrom":makeQuery(id+"F9.opExtrude","CAP_EDGE",EDGE,{"disambiguationData":[OSD([sQuery(id+"F8.wireOp",EDGE,"E20"),sQuery(id+"F8.wireOp",EDGE,"E31")])],"isStart":true})});
            var Q1;
            Q1=makeQuery(id+"F9.boolean.opBoolean","COPY",EDGE,{"derivedFrom":makeQuery(id+"F9.opExtrude","CAP_EDGE",EDGE,{"disambiguationData":[OSD([sQuery(id+"F8.wireOp",EDGE,"E35")])],"isStart":true})});
            var Q2;
            Q2=makeQuery(id+"F9.boolean.opBoolean","COPY",EDGE,{"derivedFrom":makeQuery(id+"F9.opExtrude","SWEPT_EDGE",EDGE,{"disambiguationData":[OSD([sQuery(id+"F8.wireOp",EDGE,"E20"),sQuery(id+"F8.wireOp",EDGE,"E21.right"),sQuery(id+"F8.wireOp",EDGE,"E35")])]})});
            var Q3;
            Q3=makeQuery(id+"F9.boolean.opBoolean","COPY",EDGE,{"derivedFrom":makeQuery(id+"F9.opExtrude","CAP_EDGE",EDGE,{"disambiguationData":[OSD([sQuery(id+"F8.wireOp",EDGE,"E36")])],"isStart":true})});
            var Q4;
            Q4=makeQuery(id+"F9.boolean.opBoolean","COPY",EDGE,{"derivedFrom":makeQuery(id+"F9.opExtrude","CAP_EDGE",EDGE,{"disambiguationData":[OSD([sQuery(id+"F8.wireOp",EDGE,"E20"),sQuery(id+"F8.wireOp",EDGE,"E33")])],"isStart":true})});
            var Q5;
            Q5=makeQuery(id+"F9.boolean.opBoolean","COPY",EDGE,{"derivedFrom":makeQuery(id+"F9.opExtrude","SWEPT_EDGE",EDGE,{"disambiguationData":[OSD([sQuery(id+"F8.wireOp",EDGE,"E20"),sQuery(id+"F8.wireOp",EDGE,"E21.left"),sQuery(id+"F8.wireOp",EDGE,"E36")])]})});
            var Q6;
            {var subQ0=sQuery(id+"F8.wireOp",EDGE,"E25");Q6=makeQuery(id+"F9.boolean.opBoolean","INTERSECT",EDGE,{"derivedFrom":[makeQuery(id+"F3.opExtrude","SWEPT_FACE",FACE,{"disambiguationData":[OSD([sQuery(id+"F2.wireOp",EDGE,"E1.left")])]}),makeQuery(id+"F9.opExtrude","SWEPT_FACE",FACE,{"disambiguationData":[OSD([subQ0]),TDD([makeQuery(id+"F8.imprint","IMPRINT",EDGE,{"disambiguationData":[TD([[makeQuery(id+"F8.imprint","INTERSECT",VERTEX,{"derivedFrom":[subQ0,sQuery(id+"F8.wireOp",EDGE,"E32")]}),1.0]])],"derivedFrom":subQ0})])]})]});}
            var Q7;
            Q7=makeQuery(id+"F9.boolean.opBoolean","INTERSECT",EDGE,{"derivedFrom":[makeQuery(id+"F3.opExtrude","SWEPT_FACE",FACE,{"disambiguationData":[OSD([sQuery(id+"F2.wireOp",EDGE,"E1.left")])]}),makeQuery(id+"F9.opExtrude","SWEPT_FACE",FACE,{"disambiguationData":[OSD([sQuery(id+"F8.wireOp",EDGE,"E29")])]})]});
            var Q8;
            Q8=makeQuery(id+"F9.boolean.opBoolean","COPY",EDGE,{"derivedFrom":makeQuery(id+"F9.opExtrude","SWEPT_EDGE",EDGE,{"disambiguationData":[OSD([sQuery(id+"F8.wireOp",EDGE,"E25"),sQuery(id+"F8.wireOp",EDGE,"E27.bottom"),sQuery(id+"F8.wireOp",EDGE,"E27.right"),sQuery(id+"F8.wireOp",EDGE,"E29")])]})});
            var Q9;
            Q9=makeQuery(id+"F9.boolean.opBoolean","INTERSECT",EDGE,{"derivedFrom":[makeQuery(id+"F3.opExtrude","SWEPT_FACE",FACE,{"disambiguationData":[OSD([sQuery(id+"F2.wireOp",EDGE,"E1.left")])]}),makeQuery(id+"F9.opExtrude","SWEPT_FACE",FACE,{"disambiguationData":[OSD([sQuery(id+"F8.wireOp",EDGE,"E28")])]})]});
            var Q10;
            Q10=makeQuery(id+"F9.boolean.opBoolean","COPY",EDGE,{"derivedFrom":makeQuery(id+"F9.opExtrude","SWEPT_EDGE",EDGE,{"disambiguationData":[OSD([sQuery(id+"F8.wireOp",EDGE,"E25"),sQuery(id+"F8.wireOp",EDGE,"E27.bottom"),sQuery(id+"F8.wireOp",EDGE,"E27.left"),sQuery(id+"F8.wireOp",EDGE,"E28")])]})});
            var Q11;
            {var subQ0=sQuery(id+"F8.wireOp",EDGE,"E25");Q11=makeQuery(id+"F9.boolean.opBoolean","INTERSECT",EDGE,{"derivedFrom":[makeQuery(id+"F3.opExtrude","SWEPT_FACE",FACE,{"disambiguationData":[OSD([sQuery(id+"F2.wireOp",EDGE,"E1.left")])]}),makeQuery(id+"F9.opExtrude","SWEPT_FACE",FACE,{"disambiguationData":[OSD([subQ0]),TDD([makeQuery(id+"F8.imprint","IMPRINT",EDGE,{"disambiguationData":[TD([[makeQuery(id+"F8.imprint","INTERSECT",VERTEX,{"derivedFrom":[subQ0,sQuery(id+"F8.wireOp",EDGE,"E34")]}),-1.0]])],"derivedFrom":subQ0})])]})]});}
            var Q12;
            {var subQ0=sQuery(id+"F10.wireOp",EDGE,"E43");Q12=makeQuery(id+"F11.boolean.opBoolean","INTERSECT",EDGE,{"derivedFrom":[makeQuery(id+"F3.opExtrude","SWEPT_FACE",FACE,{"disambiguationData":[OSD([sQuery(id+"F2.wireOp",EDGE,"E1.top")])]}),makeQuery(id+"F11.opExtrude","SWEPT_FACE",FACE,{"disambiguationData":[OSD([subQ0]),TDD([makeQuery(id+"F10.imprint","IMPRINT",EDGE,{"disambiguationData":[TD([[makeQuery(id+"F10.imprint","INTERSECT",VERTEX,{"derivedFrom":[subQ0,sQuery(id+"F10.wireOp",EDGE,"E50")]}),1.0]])],"derivedFrom":subQ0})])]})]});}
            var Q13;
            Q13=makeQuery(id+"F11.boolean.opBoolean","COPY",EDGE,{"derivedFrom":makeQuery(id+"F11.opExtrude","SWEPT_EDGE",EDGE,{"disambiguationData":[OSD([sQuery(id+"F10.wireOp",EDGE,"E43"),sQuery(id+"F10.wireOp",EDGE,"E45.bottom"),sQuery(id+"F10.wireOp",EDGE,"E45.right"),sQuery(id+"F10.wireOp",EDGE,"E47")])]})});
            var Q14;
            Q14=makeQuery(id+"F11.boolean.opBoolean","COPY",EDGE,{"derivedFrom":makeQuery(id+"F11.opExtrude","SWEPT_EDGE",EDGE,{"disambiguationData":[OSD([sQuery(id+"F10.wireOp",EDGE,"E43"),sQuery(id+"F10.wireOp",EDGE,"E45.bottom"),sQuery(id+"F10.wireOp",EDGE,"E45.left"),sQuery(id+"F10.wireOp",EDGE,"E46")])]})});
            var Q15;
            Q15=makeQuery(id+"F11.boolean.opBoolean","INTERSECT",EDGE,{"derivedFrom":[makeQuery(id+"F3.opExtrude","SWEPT_FACE",FACE,{"disambiguationData":[OSD([sQuery(id+"F2.wireOp",EDGE,"E1.top")])]}),makeQuery(id+"F11.opExtrude","SWEPT_FACE",FACE,{"disambiguationData":[OSD([sQuery(id+"F10.wireOp",EDGE,"E46")])]})]});
            var Q16;
            Q16=makeQuery(id+"F11.boolean.opBoolean","INTERSECT",EDGE,{"derivedFrom":[makeQuery(id+"F3.opExtrude","SWEPT_FACE",FACE,{"disambiguationData":[OSD([sQuery(id+"F2.wireOp",EDGE,"E1.top")])]}),makeQuery(id+"F11.opExtrude","SWEPT_FACE",FACE,{"disambiguationData":[OSD([sQuery(id+"F10.wireOp",EDGE,"E47")])]})]});
            var Q17;
            {var subQ0=sQuery(id+"F10.wireOp",EDGE,"E43");Q17=makeQuery(id+"F11.boolean.opBoolean","INTERSECT",EDGE,{"derivedFrom":[makeQuery(id+"F3.opExtrude","SWEPT_FACE",FACE,{"disambiguationData":[OSD([sQuery(id+"F2.wireOp",EDGE,"E1.top")])]}),makeQuery(id+"F11.opExtrude","SWEPT_FACE",FACE,{"disambiguationData":[OSD([subQ0]),TDD([makeQuery(id+"F10.imprint","IMPRINT",EDGE,{"disambiguationData":[TD([[makeQuery(id+"F10.imprint","INTERSECT",VERTEX,{"derivedFrom":[subQ0,sQuery(id+"F10.wireOp",EDGE,"E52")]}),-1.0]])],"derivedFrom":subQ0})])]})]});}
            var Q18;
            {var subQ0=sQuery(id+"F6.wireOp",EDGE,"E7");Q18=makeQuery(id+"F7.boolean.opBoolean","INTERSECT",EDGE,{"derivedFrom":[makeQuery(id+"F3.opExtrude","SWEPT_FACE",FACE,{"disambiguationData":[OSD([sQuery(id+"F2.wireOp",EDGE,"E1.bottom")])]}),makeQuery(id+"F7.opExtrude","SWEPT_FACE",FACE,{"disambiguationData":[OSD([subQ0]),TDD([makeQuery(id+"F6.imprint","IMPRINT",EDGE,{"disambiguationData":[TD([[makeQuery(id+"F6.imprint","INTERSECT",VERTEX,{"derivedFrom":[subQ0,sQuery(id+"F6.wireOp",EDGE,"E16")]}),-1.0]])],"derivedFrom":subQ0})])]})]});}
            var Q19;
            Q19=makeQuery(id+"F7.boolean.opBoolean","INTERSECT",EDGE,{"derivedFrom":[makeQuery(id+"F3.opExtrude","SWEPT_FACE",FACE,{"disambiguationData":[OSD([sQuery(id+"F2.wireOp",EDGE,"E1.bottom")])]}),makeQuery(id+"F7.opExtrude","SWEPT_FACE",FACE,{"disambiguationData":[OSD([sQuery(id+"F6.wireOp",EDGE,"E10")])]})]});
            var Q20;
            Q20=makeQuery(id+"F7.boolean.opBoolean","INTERSECT",EDGE,{"derivedFrom":[makeQuery(id+"F3.opExtrude","SWEPT_FACE",FACE,{"disambiguationData":[OSD([sQuery(id+"F2.wireOp",EDGE,"E1.bottom")])]}),makeQuery(id+"F7.opExtrude","SWEPT_FACE",FACE,{"disambiguationData":[OSD([sQuery(id+"F6.wireOp",EDGE,"E11")])]})]});
            var Q21;
            Q21=makeQuery(id+"F7.boolean.opBoolean","COPY",EDGE,{"derivedFrom":makeQuery(id+"F7.opExtrude","SWEPT_EDGE",EDGE,{"disambiguationData":[OSD([sQuery(id+"F6.wireOp",EDGE,"E7"),sQuery(id+"F6.wireOp",EDGE,"E9.bottom"),sQuery(id+"F6.wireOp",EDGE,"E9.left"),sQuery(id+"F6.wireOp",EDGE,"E10")])]})});
            var Q22;
            {var subQ0=sQuery(id+"F6.wireOp",EDGE,"E7");Q22=makeQuery(id+"F7.boolean.opBoolean","INTERSECT",EDGE,{"derivedFrom":[makeQuery(id+"F3.opExtrude","SWEPT_FACE",FACE,{"disambiguationData":[OSD([sQuery(id+"F2.wireOp",EDGE,"E1.bottom")])]}),makeQuery(id+"F7.opExtrude","SWEPT_FACE",FACE,{"disambiguationData":[OSD([subQ0]),TDD([makeQuery(id+"F6.imprint","IMPRINT",EDGE,{"disambiguationData":[TD([[makeQuery(id+"F6.imprint","INTERSECT",VERTEX,{"derivedFrom":[subQ0,sQuery(id+"F6.wireOp",EDGE,"E14")]}),1.0]])],"derivedFrom":subQ0})])]})]});}
            var Q23;
            Q23=makeQuery(id+"F7.boolean.opBoolean","COPY",EDGE,{"derivedFrom":makeQuery(id+"F7.opExtrude","SWEPT_EDGE",EDGE,{"disambiguationData":[OSD([sQuery(id+"F6.wireOp",EDGE,"E7"),sQuery(id+"F6.wireOp",EDGE,"E9.bottom"),sQuery(id+"F6.wireOp",EDGE,"E9.right"),sQuery(id+"F6.wireOp",EDGE,"E11")])]})});
            var Q24;
            {var subQ0=sQuery(id+"F12.wireOp",EDGE,"E61");Q24=makeQuery(id+"F13.boolean.opBoolean","INTERSECT",EDGE,{"derivedFrom":[makeQuery(id+"F3.opExtrude","SWEPT_FACE",FACE,{"disambiguationData":[OSD([sQuery(id+"F2.wireOp",EDGE,"E1.right")])]}),makeQuery(id+"F13.opExtrude","SWEPT_FACE",FACE,{"disambiguationData":[OSD([subQ0]),TDD([makeQuery(id+"F12.imprint","IMPRINT",EDGE,{"disambiguationData":[TD([[makeQuery(id+"F12.imprint","INTERSECT",VERTEX,{"derivedFrom":[subQ0,sQuery(id+"F12.wireOp",EDGE,"E70")]}),-1.0]])],"derivedFrom":subQ0})])]})]});}
            var Q25;
            {var subQ0=sQuery(id+"F12.wireOp",EDGE,"E61");Q25=makeQuery(id+"F13.boolean.opBoolean","INTERSECT",EDGE,{"derivedFrom":[makeQuery(id+"F3.opExtrude","SWEPT_FACE",FACE,{"disambiguationData":[OSD([sQuery(id+"F2.wireOp",EDGE,"E1.right")])]}),makeQuery(id+"F13.opExtrude","SWEPT_FACE",FACE,{"disambiguationData":[OSD([subQ0]),TDD([makeQuery(id+"F12.imprint","IMPRINT",EDGE,{"disambiguationData":[TD([[makeQuery(id+"F12.imprint","INTERSECT",VERTEX,{"derivedFrom":[subQ0,sQuery(id+"F12.wireOp",EDGE,"E68")]}),1.0]])],"derivedFrom":subQ0})])]})]});}
            var Q26;
            Q26=makeQuery(id+"F13.boolean.opBoolean","COPY",EDGE,{"derivedFrom":makeQuery(id+"F13.opExtrude","SWEPT_EDGE",EDGE,{"disambiguationData":[OSD([sQuery(id+"F12.wireOp",EDGE,"E61"),sQuery(id+"F12.wireOp",EDGE,"E63.bottom"),sQuery(id+"F12.wireOp",EDGE,"E63.right"),sQuery(id+"F12.wireOp",EDGE,"E65")])]})});
            var Q27;
            Q27=makeQuery(id+"F13.boolean.opBoolean","INTERSECT",EDGE,{"derivedFrom":[makeQuery(id+"F3.opExtrude","SWEPT_FACE",FACE,{"disambiguationData":[OSD([sQuery(id+"F2.wireOp",EDGE,"E1.right")])]}),makeQuery(id+"F13.opExtrude","SWEPT_FACE",FACE,{"disambiguationData":[OSD([sQuery(id+"F12.wireOp",EDGE,"E65")])]})]});
            var Q28;
            Q28=makeQuery(id+"F13.boolean.opBoolean","INTERSECT",EDGE,{"derivedFrom":[makeQuery(id+"F3.opExtrude","SWEPT_FACE",FACE,{"disambiguationData":[OSD([sQuery(id+"F2.wireOp",EDGE,"E1.right")])]}),makeQuery(id+"F13.opExtrude","SWEPT_FACE",FACE,{"disambiguationData":[OSD([sQuery(id+"F12.wireOp",EDGE,"E64")])]})]});
            var Q29;
            Q29=makeQuery(id+"F13.boolean.opBoolean","COPY",EDGE,{"derivedFrom":makeQuery(id+"F13.opExtrude","SWEPT_EDGE",EDGE,{"disambiguationData":[OSD([sQuery(id+"F12.wireOp",EDGE,"E61"),sQuery(id+"F12.wireOp",EDGE,"E63.bottom"),sQuery(id+"F12.wireOp",EDGE,"E63.left"),sQuery(id+"F12.wireOp",EDGE,"E64")])]})});
            var Q30;
            Q30=makeQuery(id+"F11.boolean.opBoolean","COPY",EDGE,{"derivedFrom":makeQuery(id+"F11.opExtrude","CAP_EDGE",EDGE,{"disambiguationData":[OSD([sQuery(id+"F10.wireOp",EDGE,"E38"),sQuery(id+"F10.wireOp",EDGE,"E49")])],"isStart":true})});
            var Q31;
            Q31=makeQuery(id+"F11.boolean.opBoolean","COPY",EDGE,{"derivedFrom":makeQuery(id+"F11.opExtrude","CAP_EDGE",EDGE,{"disambiguationData":[OSD([sQuery(id+"F10.wireOp",EDGE,"E53")])],"isStart":true})});
            var Q32;
            Q32=makeQuery(id+"F11.boolean.opBoolean","COPY",EDGE,{"derivedFrom":makeQuery(id+"F11.opExtrude","SWEPT_EDGE",EDGE,{"disambiguationData":[OSD([sQuery(id+"F10.wireOp",EDGE,"E38"),sQuery(id+"F10.wireOp",EDGE,"E39.right"),sQuery(id+"F10.wireOp",EDGE,"E53")])]})});
            var Q33;
            Q33=makeQuery(id+"F11.boolean.opBoolean","COPY",EDGE,{"derivedFrom":makeQuery(id+"F11.opExtrude","CAP_EDGE",EDGE,{"disambiguationData":[OSD([sQuery(id+"F10.wireOp",EDGE,"E54")])],"isStart":true})});
            var Q34;
            Q34=makeQuery(id+"F11.boolean.opBoolean","COPY",EDGE,{"derivedFrom":makeQuery(id+"F11.opExtrude","SWEPT_EDGE",EDGE,{"disambiguationData":[OSD([sQuery(id+"F10.wireOp",EDGE,"E38"),sQuery(id+"F10.wireOp",EDGE,"E39.left"),sQuery(id+"F10.wireOp",EDGE,"E54")])]})});
            var Q35;
            Q35=makeQuery(id+"F11.boolean.opBoolean","COPY",EDGE,{"derivedFrom":makeQuery(id+"F11.opExtrude","CAP_EDGE",EDGE,{"disambiguationData":[OSD([sQuery(id+"F10.wireOp",EDGE,"E38"),sQuery(id+"F10.wireOp",EDGE,"E51")])],"isStart":true})});
            var Q36;
            Q36=makeQuery(id+"F13.boolean.opBoolean","COPY",EDGE,{"derivedFrom":makeQuery(id+"F13.opExtrude","SWEPT_EDGE",EDGE,{"disambiguationData":[OSD([sQuery(id+"F12.wireOp",EDGE,"E56"),sQuery(id+"F12.wireOp",EDGE,"E57.left"),sQuery(id+"F12.wireOp",EDGE,"E72")])]})});
            var Q37;
            Q37=makeQuery(id+"F13.boolean.opBoolean","COPY",EDGE,{"derivedFrom":makeQuery(id+"F13.opExtrude","SWEPT_EDGE",EDGE,{"disambiguationData":[OSD([sQuery(id+"F12.wireOp",EDGE,"E56"),sQuery(id+"F12.wireOp",EDGE,"E57.right"),sQuery(id+"F12.wireOp",EDGE,"E71")])]})});
            var Q38;
            Q38=makeQuery(id+"F13.boolean.opBoolean","COPY",EDGE,{"derivedFrom":makeQuery(id+"F13.opExtrude","CAP_EDGE",EDGE,{"disambiguationData":[OSD([sQuery(id+"F12.wireOp",EDGE,"E56"),sQuery(id+"F12.wireOp",EDGE,"E67")])],"isStart":true})});
            var Q39;
            Q39=makeQuery(id+"F13.boolean.opBoolean","COPY",EDGE,{"derivedFrom":makeQuery(id+"F13.opExtrude","CAP_EDGE",EDGE,{"disambiguationData":[OSD([sQuery(id+"F12.wireOp",EDGE,"E71")])],"isStart":true})});
            var Q40;
            Q40=makeQuery(id+"F13.boolean.opBoolean","COPY",EDGE,{"derivedFrom":makeQuery(id+"F13.opExtrude","CAP_EDGE",EDGE,{"disambiguationData":[OSD([sQuery(id+"F12.wireOp",EDGE,"E72")])],"isStart":true})});
            var Q41;
            Q41=makeQuery(id+"F13.boolean.opBoolean","COPY",EDGE,{"derivedFrom":makeQuery(id+"F13.opExtrude","CAP_EDGE",EDGE,{"disambiguationData":[OSD([sQuery(id+"F12.wireOp",EDGE,"E56"),sQuery(id+"F12.wireOp",EDGE,"E69")])],"isStart":true})});
            var Q42;
            Q42=makeQuery(id+"F7.boolean.opBoolean","COPY",EDGE,{"derivedFrom":makeQuery(id+"F7.opExtrude","CAP_EDGE",EDGE,{"disambiguationData":[OSD([sQuery(id+"F6.wireOp",EDGE,"E17")])],"isStart":true})});
            var Q43;
            Q43=makeQuery(id+"F7.boolean.opBoolean","COPY",EDGE,{"derivedFrom":makeQuery(id+"F7.opExtrude","CAP_EDGE",EDGE,{"disambiguationData":[OSD([sQuery(id+"F6.wireOp",EDGE,"E2"),sQuery(id+"F6.wireOp",EDGE,"E13")])],"isStart":true})});
            var Q44;
            Q44=makeQuery(id+"F7.boolean.opBoolean","COPY",EDGE,{"derivedFrom":makeQuery(id+"F7.opExtrude","SWEPT_EDGE",EDGE,{"disambiguationData":[OSD([sQuery(id+"F6.wireOp",EDGE,"E2"),sQuery(id+"F6.wireOp",EDGE,"E3.right"),sQuery(id+"F6.wireOp",EDGE,"E17")])]})});
            var Q45;
            Q45=makeQuery(id+"F7.boolean.opBoolean","COPY",EDGE,{"derivedFrom":makeQuery(id+"F7.opExtrude","CAP_EDGE",EDGE,{"disambiguationData":[OSD([sQuery(id+"F6.wireOp",EDGE,"E18")])],"isStart":true})});
            var Q46;
            Q46=makeQuery(id+"F7.boolean.opBoolean","COPY",EDGE,{"derivedFrom":makeQuery(id+"F7.opExtrude","CAP_EDGE",EDGE,{"disambiguationData":[OSD([sQuery(id+"F6.wireOp",EDGE,"E2"),sQuery(id+"F6.wireOp",EDGE,"E15")])],"isStart":true})});
            var Q47;
            Q47=makeQuery(id+"F7.boolean.opBoolean","COPY",EDGE,{"derivedFrom":makeQuery(id+"F7.opExtrude","SWEPT_EDGE",EDGE,{"disambiguationData":[OSD([sQuery(id+"F6.wireOp",EDGE,"E2"),sQuery(id+"F6.wireOp",EDGE,"E3.left"),sQuery(id+"F6.wireOp",EDGE,"E18")])]})});
            fillet(context, id + "F74", {"entities" : qUnion([Q0, Q1, Q2, Q3, Q4, Q5, Q6, Q7, Q8, Q9, Q10, Q11, Q12, Q13, Q14, Q15, Q16, Q17, Q18, Q19, Q20, Q21, Q22, Q23, Q24, Q25, Q26, Q27, Q28, Q29, Q30, Q31, Q32, Q33, Q34, Q35, Q36, Q37, Q38, Q39, Q40, Q41, Q42, Q43, Q44, Q45, Q46, Q47]), "radius" : 1.27 * mm, "tangentPropagation" : true, "allowEdgeOverflow" : false});
        }
        {
            var Q0;
            {var subQ1=makeQuery(id+"F53.opExtrude","CAP_EDGE",EDGE,{"disambiguationData":[OSD([sQuery(id+"F52.wireOp",EDGE,"E173")])],"isStart":false});var subQ17=sQuery(id+"F54.wireOp",EDGE,"E174");var subQ32=makeQuery(id+"F54.imprint","INTERSECT",VERTEX,{"disambiguationData":[OD(0.0)],"derivedFrom":[subQ1,subQ17]});Q0=makeQuery(id+"F54.imprint","IMPRINT",FACE,{"disambiguationData":[TD([[makeQuery(id+"F54.imprint","IMPRINT",EDGE,{"disambiguationData":[TD([[subQ32,-1.0]])],"derivedFrom":subQ17}),-1.0]])]});}
            var sketch = newSketch(context, id + "F75", { "sketchPlane" : qUnion([Q0])});
            skCircle(sketch, "E191", {"center": v(0, 0) * mm, "radius": 14.26 * mm});
            skSolve(sketch);
        }
        {
            var Q0;
            Q0 = qSketchRegion(id + "F75", true);
            extrude(context, id + "F76", {"entities" : qUnion([Q0]), "operationType" : NewBodyOperationType.REMOVE, "depth" : 15.24 * mm, "offsetDistance" : 25.4 * mm, "hasSecondDirection" : true, "secondDirectionOppositeDirection" : false, "secondDirectionDepth" : 5.08 * mm});
        }
        {
            var Q0;
            Q0=makeQuery(id+"F76.boolean.opBoolean","COPY",FACE,{"derivedFrom":makeQuery(id+"F76.opExtrude","CAP_FACE",FACE,{"disambiguationData":[OSD([sQuery(id+"F75.wireOp",EDGE,"E191")])],"isStart":true})});
            var sketch = newSketch(context, id + "F77", { "sketchPlane" : qUnion([Q0])});
            skCircle(sketch, "E192", {"center": v(0, 0) * mm, "radius": 11.43 * mm});
            skLineSegment(sketch, "E193", {"start": v(0, 11.43) * mm, "end": v(0, -11.43) * mm});
            skSolve(sketch);
        }
        {
            var Q0;
            {var subQ0=sQuery(id+"F77.wireOp",EDGE,"E193");Q0=makeQuery(id+"F77.imprint","IMPRINT",FACE,{"disambiguationData":[TD([[makeQuery(id+"F77.imprint","IMPRINT",EDGE,{"derivedFrom":subQ0}),1.0]])]});}
            var Q1;
            Q1=sQuery(id+"F77.wireOp",EDGE,"E193");
            revolve(context, id + "F78", {"operationType" : NewBodyOperationType.REMOVE, "surfaceOperationType" : NewSurfaceOperationType.NEW, "entities" : qUnion([Q0]), "axis" : qUnion([Q1]), "revolveType" : RevolveType.FULL, "oppositeDirection" : true});
        }
    });
